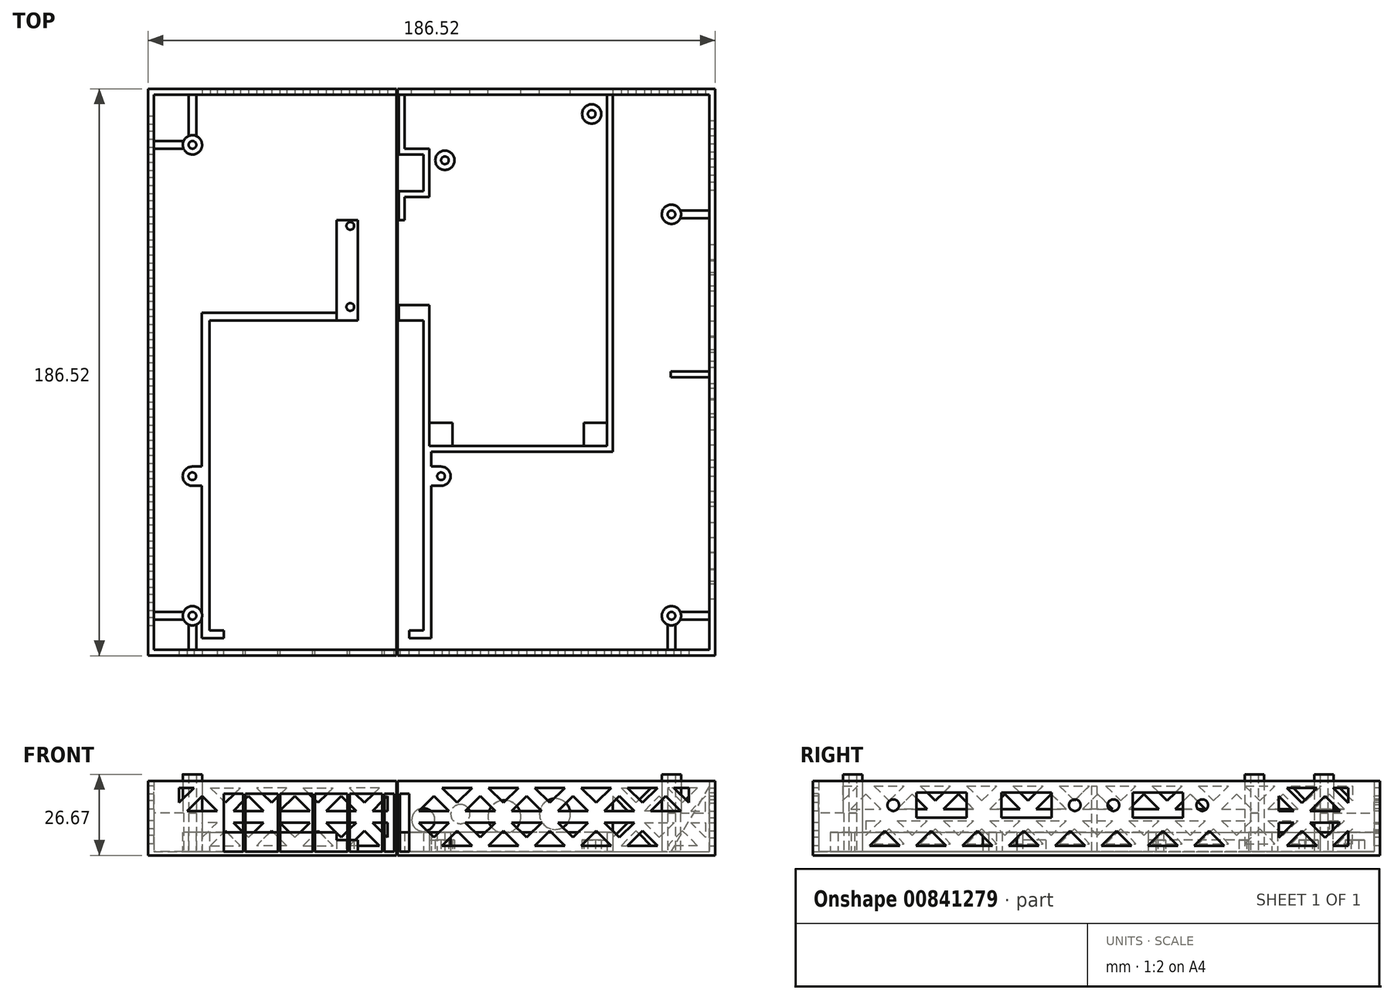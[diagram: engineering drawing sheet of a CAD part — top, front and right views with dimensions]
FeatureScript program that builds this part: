
annotation { "Feature Type Name" : "Feature", "Feature Type Description" : "" }
export const myFeature = defineFeature(function(context is Context, id is Id, definition is map)
    precondition{}
    {
        {
            var Q0;
            Q0=qCreatedBy(makeId("Top.planeOp"),FACE);
            var sketch = newSketch(context, id + "F0", { "sketchPlane" : qUnion([Q0])});
            skLineSegment(sketch, "E0.bottom", {"start": v(-6.35, 10.16) * mm, "end": v(163.65, 10.16) * mm});
            skLineSegment(sketch, "E0.top", {"start": v(-6.35, -159.84) * mm, "end": v(163.65, -159.84) * mm});
            skLineSegment(sketch, "E0.left", {"start": v(-6.35, 10.16) * mm, "end": v(-6.35, -159.84) * mm});
            skLineSegment(sketch, "E0.right", {"start": v(163.65, 10.16) * mm, "end": v(163.65, -159.84) * mm});
            skPoint(sketch, "E1", {"position": v(0, -154.94) * mm});
            skPoint(sketch, "E2", {"position": v(157.48, -22.86) * mm});
            skPoint(sketch, "E3", {"position": v(157.48, -154.94) * mm});
            skCircle(sketch, "E4", {"center": v(0, -154.94) * mm, "radius": 3.18 * mm});
            skCircle(sketch, "E5", {"center": v(0, 0) * mm, "radius": 3.18 * mm});
            skCircle(sketch, "E6", {"center": v(157.48, -22.86) * mm, "radius": 3.18 * mm});
            skCircle(sketch, "E7", {"center": v(157.48, -154.94) * mm, "radius": 3.18 * mm});
            skSolve(sketch);
        }
        {
            var Q0;
            Q0=qCreatedBy(makeId("Top.planeOp"),FACE);
            var sketch = newSketch(context, id + "F1", { "sketchPlane" : qUnion([Q0])});
            skLineSegment(sketch, "E8.0", {"start": v(-12.7, 16.51) * mm, "end": v(170, 16.51) * mm});
            skLineSegment(sketch, "E8.1", {"start": v(-12.7, 16.51) * mm, "end": v(-12.7, -166.2) * mm});
            skLineSegment(sketch, "E8.2", {"start": v(-12.7, -166.2) * mm, "end": v(170, -166.2) * mm});
            skLineSegment(sketch, "E8.3", {"start": v(170, 16.51) * mm, "end": v(170, -166.2) * mm});
            skLineSegment(sketch, "E9.0", {"start": v(-14.6, 18.42) * mm, "end": v(171.9, 18.42) * mm});
            skLineSegment(sketch, "E9.1", {"start": v(-14.6, 18.42) * mm, "end": v(-14.6, -168.1) * mm});
            skLineSegment(sketch, "E9.2", {"start": v(-14.6, -168.1) * mm, "end": v(171.9, -168.1) * mm});
            skLineSegment(sketch, "E9.3", {"start": v(171.9, 18.42) * mm, "end": v(171.9, -168.1) * mm});
            skSolve(sketch);
        }
        {
            var Q0;
            Q0 = qSketchRegion(id + "F1", true);
            extrude(context, id + "F2", {"entities" : qUnion([Q0]), "depth" : 86.36 * mm, "offsetDistance" : 25.4 * mm});
        }
        {
            var Q0;
            Q0=qCreatedBy(makeId("Top.planeOp"),FACE);
            var sketch = newSketch(context, id + "F3", { "sketchPlane" : qUnion([Q0])});
            skLineSegment(sketch, "E10.bottom", {"start": v(135.08, -97.79) * mm, "end": v(135.08, 15.24) * mm, "construction": true});
            skLineSegment(sketch, "E10.top", {"start": v(79.2, -18.41) * mm, "end": v(79.2, 0) * mm, "construction": true});
            skLineSegment(sketch, "E10.left", {"start": v(135.08, 15.24) * mm, "end": v(79.2, 15.24) * mm, "construction": true});
            skLineSegment(sketch, "E10.right", {"start": v(135.08, -97.79) * mm, "end": v(79.2, -97.79) * mm, "construction": true});
            skCircle(sketch, "E11", {"center": v(131.27, 10.16) * mm, "radius": 1.27 * mm});
            skCircle(sketch, "E12", {"center": v(131.27, 10.16) * mm, "radius": 3.18 * mm});
            skLineSegment(sketch, "E13", {"start": v(79.2, 15.24) * mm, "end": v(71.07, 15.24) * mm, "construction": true});
            skLineSegment(sketch, "E14", {"start": v(71.07, 15.24) * mm, "end": v(71.07, 0) * mm, "construction": true});
            skLineSegment(sketch, "E15", {"start": v(71.07, 0) * mm, "end": v(79.2, 0) * mm, "construction": true});
            skLineSegment(sketch, "E16", {"start": v(79.2, -18.41) * mm, "end": v(71.07, -18.41) * mm, "construction": true});
            skLineSegment(sketch, "E17", {"start": v(71.07, -18.41) * mm, "end": v(71.07, -50.16) * mm, "construction": true});
            skLineSegment(sketch, "E18", {"start": v(71.07, -50.16) * mm, "end": v(79.2, -50.16) * mm, "construction": true});
            skCircle(sketch, "E19", {"center": v(83, -5.08) * mm, "radius": 3.18 * mm});
            skCircle(sketch, "E20", {"center": v(83, -5.08) * mm, "radius": 1.27 * mm});
            skLineSegment(sketch, "E21.trimOffspring", {"start": v(79.2, -97.79) * mm, "end": v(79.2, -50.16) * mm, "construction": true});
            skLineSegment(sketch, "E22.0", {"start": v(77.93, -17.14) * mm, "end": v(77.93, -1.27) * mm});
            skLineSegment(sketch, "E22.1", {"start": v(77.93, -17.14) * mm, "end": v(69.8, -17.14) * mm});
            skLineSegment(sketch, "E22.4", {"start": v(77.93, -99.06) * mm, "end": v(77.93, -52.7) * mm});
            skLineSegment(sketch, "E22.5", {"start": v(69.8, -1.27) * mm, "end": v(77.93, -1.27) * mm});
            skLineSegment(sketch, "E22.6", {"start": v(69.8, 16.51) * mm, "end": v(69.8, -1.27) * mm});
            skLineSegment(sketch, "E22.8", {"start": v(136.35, 16.51) * mm, "end": v(69.8, 16.51) * mm});
            skLineSegment(sketch, "E22.9", {"start": v(136.35, -99.06) * mm, "end": v(136.35, 16.51) * mm});
            skLineSegment(sketch, "E22.10", {"start": v(136.35, -99.06) * mm, "end": v(77.93, -99.06) * mm});
            skLineSegment(sketch, "E23.bottom", {"start": v(77.93, -99.06) * mm, "end": v(77.93, -91.44) * mm});
            skLineSegment(sketch, "E23.top", {"start": v(85.55, -99.06) * mm, "end": v(85.55, -91.44) * mm});
            skLineSegment(sketch, "E23.left", {"start": v(77.93, -99.06) * mm, "end": v(85.55, -99.06) * mm});
            skLineSegment(sketch, "E23.right", {"start": v(77.93, -91.44) * mm, "end": v(85.55, -91.44) * mm});
            skLineSegment(sketch, "E24.bottom", {"start": v(136.35, -99.06) * mm, "end": v(136.35, -91.44) * mm});
            skLineSegment(sketch, "E24.top", {"start": v(128.73, -99.06) * mm, "end": v(128.73, -91.44) * mm});
            skLineSegment(sketch, "E24.left", {"start": v(136.35, -99.06) * mm, "end": v(128.73, -99.06) * mm});
            skLineSegment(sketch, "E24.right", {"start": v(136.35, -91.44) * mm, "end": v(128.73, -91.44) * mm});
            skLineSegment(sketch, "E25.0", {"start": v(138.25, -100.96) * mm, "end": v(76.02, -100.96) * mm});
            skLineSegment(sketch, "E25.1", {"start": v(138.25, -100.96) * mm, "end": v(138.25, 18.42) * mm});
            skLineSegment(sketch, "E25.2", {"start": v(76.02, -100.96) * mm, "end": v(76.02, -57.78) * mm});
            skLineSegment(sketch, "E25.3", {"start": v(138.25, 18.42) * mm, "end": v(67.9, 18.42) * mm});
            skLineSegment(sketch, "E25.4", {"start": v(67.9, 18.42) * mm, "end": v(67.9, -3.17) * mm});
            skLineSegment(sketch, "E25.5", {"start": v(67.9, -3.17) * mm, "end": v(76.02, -3.17) * mm});
            skLineSegment(sketch, "E25.7", {"start": v(67.9, -15.24) * mm, "end": v(67.9, -24.76) * mm});
            skLineSegment(sketch, "E25.8", {"start": v(76.02, -15.24) * mm, "end": v(67.9, -15.24) * mm});
            skLineSegment(sketch, "E25.9", {"start": v(76.02, -15.24) * mm, "end": v(76.02, -3.17) * mm});
            skLineSegment(sketch, "E26", {"start": v(76.02, -57.78) * mm, "end": v(47.45, -57.78) * mm});
            skLineSegment(sketch, "E27", {"start": v(69.8, -17.14) * mm, "end": v(69.8, -27.94) * mm});
            skCircle(sketch, "E28", {"center": v(51.9, -53.34) * mm, "radius": 1.27 * mm});
            skLineSegment(sketch, "E29", {"start": v(54.43, -52.7) * mm, "end": v(54.43, -27.94) * mm});
            skLineSegment(sketch, "E30", {"start": v(54.43, -52.7) * mm, "end": v(77.93, -52.7) * mm});
            skLineSegment(sketch, "E31", {"start": v(54.43, -27.94) * mm, "end": v(69.8, -27.94) * mm});
            skCircle(sketch, "E32", {"center": v(51.9, -26.67) * mm, "radius": 1.27 * mm});
            skLineSegment(sketch, "E33", {"start": v(47.45, -57.78) * mm, "end": v(47.45, -24.76) * mm});
            skLineSegment(sketch, "E34", {"start": v(47.45, -24.76) * mm, "end": v(67.9, -24.76) * mm});
            skLineSegment(sketch, "E35", {"start": v(54.43, -52.7) * mm, "end": v(54.43, -57.78) * mm});
            skLineSegment(sketch, "E36", {"start": v(54.43, -27.94) * mm, "end": v(54.43, -24.76) * mm});
            skLineSegment(sketch, "E37", {"start": v(136.35, 16.51) * mm, "end": v(138.25, 16.51) * mm});
            skLineSegment(sketch, "E38", {"start": v(69.8, 16.51) * mm, "end": v(67.9, 16.51) * mm});
            skLineSegment(sketch, "E39", {"start": v(67.9, -52.7) * mm, "end": v(67.9, -57.78) * mm});
            skLineSegment(sketch, "E40", {"start": v(67.9, -24.76) * mm, "end": v(69.8, -24.76) * mm});
            skSolve(sketch);
        }
        {
            var Q0;
            Q0=qCreatedBy(makeId("Top.planeOp"),FACE);
            var sketch = newSketch(context, id + "F4", { "sketchPlane" : qUnion([Q0])});
            skLineSegment(sketch, "E41.bottom", {"start": v(5.66, -57.78) * mm, "end": v(76.02, -57.78) * mm});
            skLineSegment(sketch, "E41.top", {"start": v(5.66, -159.84) * mm, "end": v(76.02, -159.84) * mm});
            skLineSegment(sketch, "E41.left", {"start": v(5.66, -57.78) * mm, "end": v(5.66, -159.84) * mm});
            skLineSegment(sketch, "E41.right", {"start": v(76.02, -57.78) * mm, "end": v(76.02, -159.84) * mm});
            skLineSegment(sketch, "E42.0", {"start": v(3.12, -55.24) * mm, "end": v(47.45, -55.24) * mm});
            skLineSegment(sketch, "E42.1", {"start": v(3.12, -55.24) * mm, "end": v(3.12, -105.86) * mm});
            skLineSegment(sketch, "E42.2", {"start": v(3.12, -162.38) * mm, "end": v(10.36, -162.38) * mm});
            skLineSegment(sketch, "E42.3", {"start": v(78.56, -100.96) * mm, "end": v(78.56, -105.86) * mm});
            skLineSegment(sketch, "E43", {"start": v(47.45, -55.24) * mm, "end": v(47.45, -57.78) * mm});
            skLineSegment(sketch, "E44", {"start": v(76.02, -100.96) * mm, "end": v(78.56, -100.96) * mm});
            skLineSegment(sketch, "E45", {"start": v(10.36, -162.38) * mm, "end": v(10.36, -159.84) * mm});
            skLineSegment(sketch, "E46", {"start": v(40.84, -162.38) * mm, "end": v(40.84, -159.84) * mm, "construction": true});
            skLineSegment(sketch, "E47.MirrorCS", {"start": v(71.32, -162.38) * mm, "end": v(71.32, -159.84) * mm});
            skLineSegment(sketch, "E48.trimOffspring", {"start": v(71.32, -162.38) * mm, "end": v(78.56, -162.38) * mm});
            skArc(sketch, "E49", {"start": v(81.74, -112.21) * mm, "mid": v(84.91, -109.04) * mm, "end": v(81.74, -105.86) * mm});
            skLineSegment(sketch, "E50", {"start": v(81.74, -105.86) * mm, "end": v(81.74, -112.21) * mm, "construction": true});
            skLineSegment(sketch, "E51", {"start": v(81.74, -112.21) * mm, "end": v(78.56, -112.21) * mm});
            skLineSegment(sketch, "E52", {"start": v(81.74, -105.86) * mm, "end": v(78.56, -105.86) * mm});
            skLineSegment(sketch, "E53.trimOffspring", {"start": v(78.56, -112.21) * mm, "end": v(78.56, -162.38) * mm});
            skLineSegment(sketch, "E54.MirrorCS", {"start": v(-0.05, -105.86) * mm, "end": v(3.12, -105.86) * mm});
            skLineSegment(sketch, "E55.MirrorCS", {"start": v(-0.05, -112.21) * mm, "end": v(3.12, -112.21) * mm});
            skArc(sketch, "E56.MirrorCS", {"start": v(-0.05, -112.21) * mm, "mid": v(-3.23, -109.04) * mm, "end": v(-0.05, -105.86) * mm});
            skLineSegment(sketch, "E57.trimOffspring", {"start": v(3.12, -112.21) * mm, "end": v(3.12, -162.38) * mm});
            skCircle(sketch, "E58", {"center": v(81.74, -109.04) * mm, "radius": 1.27 * mm});
            skCircle(sketch, "E59", {"center": v(-0.05, -109.04) * mm, "radius": 1.27 * mm});
            skSolve(sketch);
        }
        {
            var Q0;
            Q0=qCreatedBy(makeId("Top.planeOp"),FACE);
            var sketch = newSketch(context, id + "F5", { "sketchPlane" : qUnion([Q0])});
            skLineSegment(sketch, "E60.bottom", {"start": v(-14.6, 18.42) * mm, "end": v(171.9, 18.42) * mm});
            skLineSegment(sketch, "E60.top", {"start": v(-14.6, -168.1) * mm, "end": v(171.9, -168.1) * mm});
            skLineSegment(sketch, "E60.left", {"start": v(-14.6, 18.42) * mm, "end": v(-14.6, -168.1) * mm});
            skLineSegment(sketch, "E60.right", {"start": v(171.9, 18.42) * mm, "end": v(171.9, -168.1) * mm});
            skSolve(sketch);
        }
        {
            var Q0;
            Q0 = qSketchRegion(id + "F5", true);
            extrude(context, id + "F6", {"entities" : qUnion([Q0]), "operationType" : NewBodyOperationType.ADD, "oppositeDirection" : true, "depth" : 1.27 * mm, "offsetDistance" : 25.4 * mm});
        }
        {
            var Q0;
            Q0=qCreatedBy(makeId("Top.planeOp"),FACE);
            var sketch = newSketch(context, id + "F7", { "sketchPlane" : qUnion([Q0])});
            skLineSegment(sketch, "E61.bottom", {"start": v(77.93, -91.44) * mm, "end": v(85.55, -91.44) * mm});
            skLineSegment(sketch, "E61.top", {"start": v(77.93, -99.06) * mm, "end": v(85.55, -99.06) * mm});
            skLineSegment(sketch, "E61.left", {"start": v(77.93, -91.44) * mm, "end": v(77.93, -99.06) * mm});
            skLineSegment(sketch, "E61.right", {"start": v(85.55, -91.44) * mm, "end": v(85.55, -99.06) * mm});
            skLineSegment(sketch, "E62.bottom", {"start": v(128.73, -91.44) * mm, "end": v(136.35, -91.44) * mm});
            skLineSegment(sketch, "E62.top", {"start": v(128.73, -99.06) * mm, "end": v(136.35, -99.06) * mm});
            skLineSegment(sketch, "E62.left", {"start": v(128.73, -91.44) * mm, "end": v(128.73, -99.06) * mm});
            skLineSegment(sketch, "E62.right", {"start": v(136.35, -91.44) * mm, "end": v(136.35, -99.06) * mm});
            skCircle(sketch, "E63.0", {"center": v(83, -5.08) * mm, "radius": 3.18 * mm});
            skCircle(sketch, "E63.1", {"center": v(131.27, 10.16) * mm, "radius": 3.18 * mm});
            skCircle(sketch, "E64.0", {"center": v(83, -5.08) * mm, "radius": 1.27 * mm});
            skCircle(sketch, "E64.1", {"center": v(131.27, 10.16) * mm, "radius": 1.27 * mm});
            skLineSegment(sketch, "E65.bottom", {"start": v(47.45, -24.76) * mm, "end": v(54.43, -24.76) * mm});
            skLineSegment(sketch, "E65.top", {"start": v(47.45, -57.78) * mm, "end": v(54.43, -57.78) * mm});
            skLineSegment(sketch, "E65.left", {"start": v(47.45, -24.76) * mm, "end": v(47.45, -57.78) * mm});
            skLineSegment(sketch, "E65.right", {"start": v(54.43, -24.76) * mm, "end": v(54.43, -57.78) * mm});
            skCircle(sketch, "E66.1", {"center": v(51.9, -26.67) * mm, "radius": 1.27 * mm});
            skCircle(sketch, "E66.2", {"center": v(51.9, -53.34) * mm, "radius": 1.27 * mm});
            skSolve(sketch);
        }
        {
            var Q0;
            Q0 = qSketchRegion(id + "F7", true);
            extrude(context, id + "F8", {"entities" : qUnion([Q0]), "operationType" : NewBodyOperationType.ADD, "depth" : 3.8 * mm, "offsetDistance" : 25.4 * mm});
        }
        {
            var Q0;
            Q0=qCreatedBy(makeId("Top.planeOp"),FACE);
            var sketch = newSketch(context, id + "F9", { "sketchPlane" : qUnion([Q0])});
            skLineSegment(sketch, "E67.0", {"start": v(67.9, -15.24) * mm, "end": v(67.9, -24.76) * mm});
            skLineSegment(sketch, "E67.1", {"start": v(67.9, -24.76) * mm, "end": v(69.8, -24.76) * mm});
            skLineSegment(sketch, "E67.2", {"start": v(69.8, -17.14) * mm, "end": v(69.8, -24.76) * mm});
            skLineSegment(sketch, "E67.3", {"start": v(76.02, -15.24) * mm, "end": v(67.9, -15.24) * mm});
            skLineSegment(sketch, "E67.4", {"start": v(77.93, -17.14) * mm, "end": v(69.8, -17.14) * mm});
            skLineSegment(sketch, "E67.5", {"start": v(77.93, -17.14) * mm, "end": v(77.93, -1.27) * mm});
            skLineSegment(sketch, "E67.6", {"start": v(76.02, -15.24) * mm, "end": v(76.02, -3.17) * mm});
            skLineSegment(sketch, "E67.7", {"start": v(69.8, -1.27) * mm, "end": v(77.93, -1.27) * mm});
            skLineSegment(sketch, "E67.8", {"start": v(67.9, -3.17) * mm, "end": v(76.02, -3.17) * mm});
            skLineSegment(sketch, "E67.9", {"start": v(67.9, 16.51) * mm, "end": v(67.9, -3.17) * mm});
            skLineSegment(sketch, "E67.10", {"start": v(69.8, 16.51) * mm, "end": v(69.8, -1.27) * mm});
            skLineSegment(sketch, "E67.13", {"start": v(136.35, -99.06) * mm, "end": v(136.35, 16.51) * mm});
            skLineSegment(sketch, "E67.14", {"start": v(138.25, -100.96) * mm, "end": v(138.25, 16.51) * mm});
            skLineSegment(sketch, "E67.15", {"start": v(136.35, -99.06) * mm, "end": v(77.93, -99.06) * mm});
            skLineSegment(sketch, "E67.16", {"start": v(138.25, -100.96) * mm, "end": v(78.56, -100.96) * mm});
            skLineSegment(sketch, "E67.17", {"start": v(78.56, -100.96) * mm, "end": v(78.56, -105.86) * mm});
            skLineSegment(sketch, "E67.18", {"start": v(81.74, -105.86) * mm, "end": v(78.56, -105.86) * mm});
            skArc(sketch, "E67.19", {"start": v(81.74, -112.21) * mm, "mid": v(84.91, -109.04) * mm, "end": v(81.74, -105.86) * mm});
            skLineSegment(sketch, "E67.20.1", {"start": v(76.02, -100.96) * mm, "end": v(76.02, -159.84) * mm});
            skLineSegment(sketch, "E67.20.2", {"start": v(76.02, -159.84) * mm, "end": v(71.32, -159.84) * mm});
            skLineSegment(sketch, "E67.20.3", {"start": v(71.32, -159.84) * mm, "end": v(71.32, -162.38) * mm});
            skLineSegment(sketch, "E67.20.4", {"start": v(71.32, -162.38) * mm, "end": v(78.56, -162.38) * mm});
            skLineSegment(sketch, "E67.20.5", {"start": v(78.56, -162.38) * mm, "end": v(78.56, -112.21) * mm});
            skLineSegment(sketch, "E67.20.6", {"start": v(78.56, -112.21) * mm, "end": v(81.74, -112.21) * mm});
            skArc(sketch, "E67.20.7", {"start": v(81.74, -112.21) * mm, "mid": v(84.91, -109.04) * mm, "end": v(81.74, -105.86) * mm});
            skLineSegment(sketch, "E67.20.8", {"start": v(81.74, -105.86) * mm, "end": v(78.56, -105.86) * mm});
            skLineSegment(sketch, "E67.20.9", {"start": v(78.56, -105.86) * mm, "end": v(78.56, -100.96) * mm});
            skLineSegment(sketch, "E67.21.0", {"start": v(47.45, -57.78) * mm, "end": v(47.45, -55.24) * mm});
            skLineSegment(sketch, "E67.21.1", {"start": v(47.45, -55.24) * mm, "end": v(3.12, -55.24) * mm});
            skLineSegment(sketch, "E67.21.2", {"start": v(3.12, -55.24) * mm, "end": v(3.12, -105.86) * mm});
            skLineSegment(sketch, "E67.21.3", {"start": v(3.12, -105.86) * mm, "end": v(-0.05, -105.86) * mm});
            skArc(sketch, "E67.21.4", {"start": v(-0.05, -105.86) * mm, "mid": v(-3.23, -109.04) * mm, "end": v(-0.05, -112.21) * mm});
            skLineSegment(sketch, "E67.21.5", {"start": v(-0.05, -112.21) * mm, "end": v(3.12, -112.21) * mm});
            skLineSegment(sketch, "E67.21.6", {"start": v(3.12, -112.21) * mm, "end": v(3.12, -162.38) * mm});
            skLineSegment(sketch, "E67.21.7", {"start": v(3.12, -162.38) * mm, "end": v(10.36, -162.38) * mm});
            skLineSegment(sketch, "E67.21.8", {"start": v(10.36, -162.38) * mm, "end": v(10.36, -159.84) * mm});
            skLineSegment(sketch, "E67.21.9", {"start": v(10.36, -159.84) * mm, "end": v(5.66, -159.84) * mm});
            skLineSegment(sketch, "E67.21.10", {"start": v(5.66, -159.84) * mm, "end": v(5.66, -57.78) * mm});
            skLineSegment(sketch, "E67.21.11", {"start": v(5.66, -57.78) * mm, "end": v(47.45, -57.78) * mm});
            skLineSegment(sketch, "E67.22", {"start": v(76.02, -100.96) * mm, "end": v(76.02, -57.78) * mm});
            skLineSegment(sketch, "E67.23", {"start": v(77.93, -99.06) * mm, "end": v(77.93, -52.7) * mm});
            skLineSegment(sketch, "E67.24", {"start": v(67.9, -52.7) * mm, "end": v(77.93, -52.7) * mm});
            skLineSegment(sketch, "E67.25", {"start": v(67.9, -52.7) * mm, "end": v(67.9, -57.78) * mm});
            skLineSegment(sketch, "E67.26", {"start": v(76.02, -57.78) * mm, "end": v(67.9, -57.78) * mm});
            skPoint(sketch, "E68.orphan", {"position": v(69.8, -27.94) * mm});
            skPoint(sketch, "E69.orphan", {"position": v(54.43, -52.7) * mm});
            skPoint(sketch, "E70.orphan", {"position": v(47.45, -57.78) * mm});
            skPoint(sketch, "E71.orphan", {"position": v(76.02, -100.96) * mm});
            skLineSegment(sketch, "E72.0", {"start": v(67.9, 16.51) * mm, "end": v(69.8, 16.51) * mm});
            skPoint(sketch, "E73.orphan", {"position": v(-12.7, 16.51) * mm});
            skPoint(sketch, "E74.orphan", {"position": v(170, 16.51) * mm});
            skPoint(sketch, "E75.orphan", {"position": v(138.25, 18.42) * mm});
            skPoint(sketch, "E76.orphan", {"position": v(67.9, 18.42) * mm});
            skLineSegment(sketch, "E77.trimOffspring", {"start": v(136.35, 16.51) * mm, "end": v(138.25, 16.51) * mm});
            skCircle(sketch, "E78.0", {"center": v(-0.05, -109.04) * mm, "radius": 1.27 * mm});
            skCircle(sketch, "E78.1", {"center": v(81.74, -109.04) * mm, "radius": 1.27 * mm});
            skSolve(sketch);
        }
        {
            var Q0;
            Q0 = qSketchRegion(id + "F9", true);
            extrude(context, id + "F10", {"entities" : qUnion([Q0]), "operationType" : NewBodyOperationType.ADD, "depth" : 6.35 * mm, "offsetDistance" : 25.4 * mm});
        }
        {
            var Q0;
            Q0=makeQuery(id+"F6.boolean.opBoolean","MERGE",FACE,{"derivedFrom":[makeQuery(id+"F2.opExtrude","SWEPT_FACE",FACE,{"disambiguationData":[OSD([sQuery(id+"F1.wireOp",EDGE,"E9.0")])]}),makeQuery(id+"F6.opExtrude","SWEPT_FACE",FACE,{"disambiguationData":[OSD([sQuery(id+"F5.wireOp",EDGE,"E60.bottom")])]})]});
            var sketch = newSketch(context, id + "F11", { "sketchPlane" : qUnion([Q0])});
            skCircle(sketch, "E79", {"center": v(-119.2, 12.32) * mm, "radius": 5.08 * mm});
            skCircle(sketch, "E80", {"center": v(-102.56, 11.43) * mm, "radius": 5.4 * mm});
            skCircle(sketch, "E81", {"center": v(-88.09, 12.32) * mm, "radius": 3.18 * mm});
            skCircle(sketch, "E82", {"center": v(-75.9, 10.41) * mm, "radius": 3.81 * mm});
            skLineSegment(sketch, "E83", {"start": v(-54.43, 3.81) * mm, "end": v(-135.08, 3.81) * mm, "construction": true});
            skLineSegment(sketch, "E84", {"start": v(-135.08, 3.81) * mm, "end": v(-135.08, 0) * mm, "construction": true});
            skSolve(sketch);
        }
        {
            var Q0;
            Q0 = qSketchRegion(id + "F11", true);
            extrude(context, id + "F12", {"entities" : qUnion([Q0]), "operationType" : NewBodyOperationType.REMOVE, "endBound" : BoundingType.UP_TO_NEXT, "oppositeDirection" : true, "depth" : 25.4 * mm, "offsetDistance" : 25.4 * mm});
        }
        {
            var Q0;
            Q0=makeQuery(id+"F2.opExtrude","SWEPT_FACE",FACE,{"disambiguationData":[OSD([sQuery(id+"F1.wireOp",EDGE,"E8.2")])]});
            var sketch = newSketch(context, id + "F13", { "sketchPlane" : qUnion([Q0])});
            skLineSegment(sketch, "E85.0", {"start": v(-10.36, 6.35) * mm, "end": v(-10.36, 0) * mm});
            skLineSegment(sketch, "E85.1", {"start": v(-71.32, 6.35) * mm, "end": v(-71.32, 0) * mm});
            skLineSegment(sketch, "E86", {"start": v(-10.36, 6.35) * mm, "end": v(-71.32, 6.35) * mm, "construction": true});
            skLineSegment(sketch, "E87", {"start": v(-10.36, 0) * mm, "end": v(-71.32, 0) * mm});
            skLineSegment(sketch, "E88", {"start": v(-10.36, 6.35) * mm, "end": v(-10.36, 19.05) * mm});
            skLineSegment(sketch, "E89", {"start": v(-10.36, 19.05) * mm, "end": v(-71.32, 19.05) * mm});
            skLineSegment(sketch, "E90", {"start": v(-71.32, 19.05) * mm, "end": v(-71.32, 6.35) * mm});
            skLineSegment(sketch, "E91", {"start": v(-16.71, 19.05) * mm, "end": v(-16.71, 0) * mm});
            skLineSegment(sketch, "E92", {"start": v(-17.47, 19.05) * mm, "end": v(-17.47, 0) * mm});
            skLineSegment(sketch, "E93.1.0.0", {"start": v(-28.14, 19.05) * mm, "end": v(-28.14, 0) * mm});
            skLineSegment(sketch, "E93.1.0.1", {"start": v(-28.9, 19.05) * mm, "end": v(-28.9, 0) * mm});
            skLineSegment(sketch, "E93.2.0.0", {"start": v(-39.57, 19.05) * mm, "end": v(-39.57, 0) * mm});
            skLineSegment(sketch, "E93.2.0.1", {"start": v(-40.33, 19.05) * mm, "end": v(-40.33, 0) * mm});
            skLineSegment(sketch, "E93.3.0.0", {"start": v(-51, 19.05) * mm, "end": v(-51, 0) * mm});
            skLineSegment(sketch, "E93.3.0.1", {"start": v(-51.76, 19.05) * mm, "end": v(-51.76, 0) * mm});
            skLineSegment(sketch, "E93.4.0.0", {"start": v(-62.43, 19.05) * mm, "end": v(-62.43, 0) * mm});
            skLineSegment(sketch, "E93.4.0.1", {"start": v(-63.2, 19.05) * mm, "end": v(-63.2, 0) * mm});
            skLineSegment(sketch, "E93.direction1", {"start": v(-17.47, 0) * mm, "end": v(-28.9, 0) * mm, "construction": true});
            skSolve(sketch);
        }
        {
            var Q0;
            {var subQ4=sQuery(id+"F13.wireOp",EDGE,"E85.0");Q0=makeQuery(id+"F13.imprint","IMPRINT",FACE,{"disambiguationData":[TD([[makeQuery(id+"F13.imprint","IMPRINT",EDGE,{"derivedFrom":subQ4}),-1.0]])]});}
            var Q1;
            {var subQ0=sQuery(id+"F13.wireOp",EDGE,"E92");Q1=makeQuery(id+"F13.imprint","IMPRINT",FACE,{"disambiguationData":[TD([[makeQuery(id+"F13.imprint","IMPRINT",EDGE,{"derivedFrom":subQ0}),-1.0]])]});}
            var Q2;
            {var subQ0=sQuery(id+"F13.wireOp",EDGE,"E93.1.0.1");Q2=makeQuery(id+"F13.imprint","IMPRINT",FACE,{"disambiguationData":[TD([[makeQuery(id+"F13.imprint","IMPRINT",EDGE,{"derivedFrom":subQ0}),-1.0]])]});}
            var Q3;
            {var subQ0=sQuery(id+"F13.wireOp",EDGE,"E93.2.0.1");Q3=makeQuery(id+"F13.imprint","IMPRINT",FACE,{"disambiguationData":[TD([[makeQuery(id+"F13.imprint","IMPRINT",EDGE,{"derivedFrom":subQ0}),-1.0]])]});}
            var Q4;
            {var subQ0=sQuery(id+"F13.wireOp",EDGE,"E93.3.0.1");Q4=makeQuery(id+"F13.imprint","IMPRINT",FACE,{"disambiguationData":[TD([[makeQuery(id+"F13.imprint","IMPRINT",EDGE,{"derivedFrom":subQ0}),-1.0]])]});}
            var Q5;
            {var subQ4=sQuery(id+"F13.wireOp",EDGE,"E85.1");Q5=makeQuery(id+"F13.imprint","IMPRINT",FACE,{"disambiguationData":[TD([[makeQuery(id+"F13.imprint","IMPRINT",EDGE,{"derivedFrom":subQ4}),1.0]])]});}
            extrude(context, id + "F14", {"entities" : qUnion([Q0, Q1, Q2, Q3, Q4, Q5]), "operationType" : NewBodyOperationType.REMOVE, "oppositeDirection" : true, "depth" : 2.54 * mm, "offsetDistance" : 25.4 * mm});
        }
        {
            var Q0;
            Q0=makeQuery(id+"F6.boolean.opBoolean","MERGE",FACE,{"derivedFrom":[makeQuery(id+"F2.opExtrude","SWEPT_FACE",FACE,{"disambiguationData":[OSD([sQuery(id+"F1.wireOp",EDGE,"E9.3")])]}),makeQuery(id+"F6.opExtrude","SWEPT_FACE",FACE,{"disambiguationData":[OSD([sQuery(id+"F5.wireOp",EDGE,"E60.right")])]})]});
            var sketch = newSketch(context, id + "F15", { "sketchPlane" : qUnion([Q0])});
            skLineSegment(sketch, "E94.bottom", {"start": v(-149.86, 8.9) * mm, "end": v(-25.4, 8.9) * mm, "construction": true});
            skLineSegment(sketch, "E94.top", {"start": v(-149.86, 21.59) * mm, "end": v(-25.4, 21.59) * mm, "construction": true});
            skLineSegment(sketch, "E94.left", {"start": v(-149.86, 8.9) * mm, "end": v(-149.86, 21.6) * mm, "construction": true});
            skLineSegment(sketch, "E94.right", {"start": v(-25.4, 8.9) * mm, "end": v(-25.4, 21.59) * mm, "construction": true});
            skLineSegment(sketch, "E95", {"start": v(-111.76, 21.6) * mm, "end": v(-111.76, 8.9) * mm, "construction": true});
            skLineSegment(sketch, "E96.bottom", {"start": v(-117.47, 19.37) * mm, "end": v(-133.98, 19.37) * mm});
            skLineSegment(sketch, "E96.top", {"start": v(-117.47, 11.11) * mm, "end": v(-133.98, 11.11) * mm});
            skLineSegment(sketch, "E96.left", {"start": v(-117.47, 19.37) * mm, "end": v(-117.47, 11.11) * mm});
            skLineSegment(sketch, "E96.right", {"start": v(-133.98, 19.37) * mm, "end": v(-133.98, 11.11) * mm});
            skPoint(sketch, "E96.middle", {"position": v(-125.73, 15.24) * mm});
            skPoint(sketch, "E97", {"position": v(-111.76, 15.24) * mm});
            skCircle(sketch, "E98", {"center": v(-141.6, 15.24) * mm, "radius": 1.9 * mm});
            skPoint(sketch, "E98.centerSnap0", {"position": v(-133.98, 15.24) * mm});
            skLineSegment(sketch, "E99.MirrorCS", {"start": v(-106.04, 19.37) * mm, "end": v(-106.04, 11.11) * mm});
            skLineSegment(sketch, "E100.MirrorCS", {"start": v(-106.04, 19.37) * mm, "end": v(-89.53, 19.37) * mm});
            skLineSegment(sketch, "E101.MirrorCS", {"start": v(-89.53, 19.37) * mm, "end": v(-89.53, 11.11) * mm});
            skPoint(sketch, "E102.MirrorP", {"position": v(-89.53, 15.24) * mm});
            skCircle(sketch, "E103.MirrorC", {"center": v(-81.91, 15.24) * mm, "radius": 1.9 * mm});
            skPoint(sketch, "E104.MirrorP", {"position": v(-97.79, 15.24) * mm});
            skLineSegment(sketch, "E105.MirrorCS", {"start": v(-106.04, 11.11) * mm, "end": v(-89.53, 11.11) * mm});
            skLineSegment(sketch, "E106", {"start": v(-54.6, 21.6) * mm, "end": v(-54.6, 8.9) * mm, "construction": true});
            skLineSegment(sketch, "E107.bottom", {"start": v(-46.35, 19.37) * mm, "end": v(-62.86, 19.37) * mm});
            skLineSegment(sketch, "E107.top", {"start": v(-46.35, 11.11) * mm, "end": v(-62.86, 11.11) * mm});
            skLineSegment(sketch, "E107.left", {"start": v(-46.35, 19.37) * mm, "end": v(-46.35, 11.11) * mm});
            skLineSegment(sketch, "E107.right", {"start": v(-62.86, 19.37) * mm, "end": v(-62.86, 11.11) * mm});
            skPoint(sketch, "E107.middle", {"position": v(-54.6, 15.24) * mm});
            skCircle(sketch, "E108", {"center": v(-69.22, 15.24) * mm, "radius": 1.9 * mm});
            skCircle(sketch, "E109.MirrorC", {"center": v(-40, 15.24) * mm, "radius": 1.9 * mm});
            skLineSegment(sketch, "E110", {"start": v(-75.56, 21.59) * mm, "end": v(-75.56, 8.9) * mm, "construction": true});
            skSolve(sketch);
        }
        {
            var Q0;
            Q0 = qSketchRegion(id + "F15", true);
            extrude(context, id + "F16", {"entities" : qUnion([Q0]), "operationType" : NewBodyOperationType.REMOVE, "endBound" : BoundingType.UP_TO_NEXT, "oppositeDirection" : true, "depth" : 25.4 * mm, "offsetDistance" : 25.4 * mm});
        }
        {
            var Q0;
            Q0=sQuery(id+"F15.wireOp",EDGE,"E110");
            cPoint(context, id + "F17", {"entities" : qUnion([Q0]), "parameter" : 0.5});
        }
        {
            var Q0;
            Q0=qCreatedBy(makeId("Front.planeOp"),FACE);
            var Q1;
            Q1 = qCreatedBy(id + "F17" ,VERTEX);
            cPlane(context, id + "F18", {"entities" : qUnion([Q0, Q1]), "cplaneType" : CPlaneType.PLANE_POINT, "offset" : 25.4 * mm, "width" : 152.4 * mm, "height" : 152.4 * mm});
        }
        {
            var Q0;
            Q0=qCreatedBy(id+"F18.planeOp",FACE);
            var sketch = newSketch(context, id + "F19", { "sketchPlane" : qUnion([Q0])});
            skLineSegment(sketch, "E111", {"start": v(170, 21.6) * mm, "end": v(157.3, 0) * mm});
            skLineSegment(sketch, "E112", {"start": v(157.3, 0) * mm, "end": v(170, 0) * mm});
            skLineSegment(sketch, "E113", {"start": v(170, 0) * mm, "end": v(170, 21.59) * mm});
            skSolve(sketch);
        }
        {
            var Q0;
            Q0 = qSketchRegion(id + "F19", true);
            extrude(context, id + "F20", {"entities" : qUnion([Q0]), "operationType" : NewBodyOperationType.ADD, "endBound" : BoundingType.SYMMETRIC, "depth" : 1.9 * mm, "offsetDistance" : 25.4 * mm});
        }
        {
            var Q0;
            Q0=qCreatedBy(makeId("Top.planeOp"),FACE);
            var sketch = newSketch(context, id + "F21", { "sketchPlane" : qUnion([Q0])});
            skCircle(sketch, "E114.0", {"center": v(0, 0) * mm, "radius": 3.18 * mm});
            skCircle(sketch, "E114.1", {"center": v(157.48, -22.86) * mm, "radius": 3.18 * mm});
            skCircle(sketch, "E114.2", {"center": v(157.48, -154.94) * mm, "radius": 3.18 * mm});
            skCircle(sketch, "E114.3", {"center": v(0, -154.94) * mm, "radius": 3.18 * mm});
            skCircle(sketch, "E115", {"center": v(0, 0) * mm, "radius": 1.27 * mm});
            skCircle(sketch, "E116", {"center": v(157.48, -22.86) * mm, "radius": 1.27 * mm});
            skCircle(sketch, "E117", {"center": v(157.48, -154.94) * mm, "radius": 1.27 * mm});
            skCircle(sketch, "E118", {"center": v(0, -154.94) * mm, "radius": 1.27 * mm});
            skLineSegment(sketch, "E119", {"start": v(160.39, -153.67) * mm, "end": v(170, -153.67) * mm});
            skLineSegment(sketch, "E120.0", {"start": v(170, -21.59) * mm, "end": v(170, -24.13) * mm});
            skLineSegment(sketch, "E120.1", {"start": v(-1.27, -166.2) * mm, "end": v(1.27, -166.2) * mm});
            skLineSegment(sketch, "E120.2", {"start": v(-1.27, 16.51) * mm, "end": v(1.27, 16.51) * mm});
            skLineSegment(sketch, "E120.3", {"start": v(-12.7, 1.27) * mm, "end": v(-12.7, -1.27) * mm});
            skLineSegment(sketch, "E121", {"start": v(156.21, -157.85) * mm, "end": v(156.21, -166.2) * mm});
            skLineSegment(sketch, "E122", {"start": v(158.75, -157.85) * mm, "end": v(158.75, -166.2) * mm});
            skPoint(sketch, "E123.orphan", {"position": v(157.48, -153.67) * mm});
            skLineSegment(sketch, "E124.trimOffspring", {"start": v(160.39, -156.2) * mm, "end": v(170, -156.2) * mm});
            skPoint(sketch, "E125.start.orphan", {"position": v(157.48, -156.2) * mm});
            skPoint(sketch, "E126.orphan", {"position": v(158.75, -154.94) * mm});
            skPoint(sketch, "E127.orphan", {"position": v(156.21, -154.94) * mm});
            skLineSegment(sketch, "E128", {"start": v(-2.9, -153.67) * mm, "end": v(-12.7, -153.67) * mm});
            skLineSegment(sketch, "E129", {"start": v(1.27, -157.85) * mm, "end": v(1.27, -166.2) * mm});
            skPoint(sketch, "E130.orphan", {"position": v(0, -153.67) * mm});
            skLineSegment(sketch, "E131.trimOffspring", {"start": v(-2.9, -156.2) * mm, "end": v(-12.7, -156.2) * mm});
            skLineSegment(sketch, "E132.trimOffspring", {"start": v(-1.27, -157.85) * mm, "end": v(-1.27, -166.2) * mm});
            skPoint(sketch, "E133.start.orphan", {"position": v(0, -156.2) * mm});
            skPoint(sketch, "E134.start.orphan", {"position": v(-1.27, -154.94) * mm});
            skPoint(sketch, "E135.orphan", {"position": v(1.27, -154.94) * mm});
            skLineSegment(sketch, "E136", {"start": v(1.27, 2.9) * mm, "end": v(1.27, 16.51) * mm});
            skLineSegment(sketch, "E137", {"start": v(-1.27, 2.9) * mm, "end": v(-1.27, 16.51) * mm});
            skLineSegment(sketch, "E138", {"start": v(-2.9, -1.27) * mm, "end": v(-12.7, -1.27) * mm});
            skLineSegment(sketch, "E139", {"start": v(-2.9, 1.27) * mm, "end": v(-12.7, 1.27) * mm});
            skPoint(sketch, "E140.orphan", {"position": v(0, 1.27) * mm});
            skPoint(sketch, "E141.orphan", {"position": v(-1.27, 0) * mm});
            skPoint(sketch, "E142.orphan", {"position": v(1.27, 0) * mm});
            skPoint(sketch, "E143.orphan", {"position": v(0, -1.27) * mm});
            skLineSegment(sketch, "E144", {"start": v(160.39, -21.59) * mm, "end": v(170, -21.59) * mm});
            skLineSegment(sketch, "E145", {"start": v(160.39, -24.13) * mm, "end": v(170, -24.13) * mm});
            skPoint(sketch, "E146.orphan", {"position": v(157.48, -21.59) * mm});
            skPoint(sketch, "E147.orphan", {"position": v(157.48, -24.13) * mm});
            skPoint(sketch, "E148.orphan", {"position": v(-12.7, 16.51) * mm});
            skLineSegment(sketch, "E149.trimOffspring", {"start": v(-12.7, -153.67) * mm, "end": v(-12.7, -156.2) * mm});
            skPoint(sketch, "E150.orphan", {"position": v(-12.7, -166.2) * mm});
            skLineSegment(sketch, "E151.trimOffspring", {"start": v(156.21, -166.2) * mm, "end": v(158.75, -166.2) * mm});
            skPoint(sketch, "E152.orphan", {"position": v(170, -166.2) * mm});
            skLineSegment(sketch, "E153.trimOffspring", {"start": v(170, -153.67) * mm, "end": v(170, -156.2) * mm});
            skPoint(sketch, "E154.orphan", {"position": v(170, 16.51) * mm});
            skSolve(sketch);
        }
        {
            var Q0;
            Q0=makeQuery(id+"F21.imprint","IMPRINT",FACE,{"disambiguationData":[TD([[makeQuery(id+"F21.imprint","IMPRINT",EDGE,{"derivedFrom":sQuery(id+"F21.wireOp",EDGE,"E120.2")}),-1.0]])]});
            var Q1;
            Q1=makeQuery(id+"F21.imprint","IMPRINT",FACE,{"disambiguationData":[TD([[makeQuery(id+"F21.imprint","IMPRINT",EDGE,{"derivedFrom":sQuery(id+"F21.wireOp",EDGE,"E120.3")}),1.0]])]});
            var Q2;
            Q2=makeQuery(id+"F21.imprint","IMPRINT",FACE,{"disambiguationData":[TD([[makeQuery(id+"F21.imprint","IMPRINT",EDGE,{"derivedFrom":sQuery(id+"F21.wireOp",EDGE,"E115")}),1.0]])]});
            var Q3;
            Q3=makeQuery(id+"F21.imprint","IMPRINT",FACE,{"disambiguationData":[TD([[makeQuery(id+"F21.imprint","IMPRINT",EDGE,{"derivedFrom":sQuery(id+"F21.wireOp",EDGE,"E116")}),1.0]])]});
            var Q4;
            Q4=makeQuery(id+"F21.imprint","IMPRINT",FACE,{"disambiguationData":[TD([[makeQuery(id+"F21.imprint","IMPRINT",EDGE,{"derivedFrom":sQuery(id+"F21.wireOp",EDGE,"E120.0")}),-1.0]])]});
            var Q5;
            Q5=makeQuery(id+"F21.imprint","IMPRINT",FACE,{"disambiguationData":[TD([[makeQuery(id+"F21.imprint","IMPRINT",EDGE,{"derivedFrom":sQuery(id+"F21.wireOp",EDGE,"E117")}),1.0]])]});
            var Q6;
            {var subQ0=sQuery(id+"F21.wireOp",EDGE,"E119");Q6=makeQuery(id+"F21.imprint","IMPRINT",FACE,{"disambiguationData":[TD([[makeQuery(id+"F21.imprint","IMPRINT",EDGE,{"derivedFrom":subQ0}),-1.0]])]});}
            var Q7;
            {var subQ0=sQuery(id+"F21.wireOp",EDGE,"E121");Q7=makeQuery(id+"F21.imprint","IMPRINT",FACE,{"disambiguationData":[TD([[makeQuery(id+"F21.imprint","IMPRINT",EDGE,{"derivedFrom":subQ0}),1.0]])]});}
            var Q8;
            {var subQ0=sQuery(id+"F21.wireOp",EDGE,"E128");Q8=makeQuery(id+"F21.imprint","IMPRINT",FACE,{"disambiguationData":[TD([[makeQuery(id+"F21.imprint","IMPRINT",EDGE,{"derivedFrom":subQ0}),1.0]])]});}
            var Q9;
            Q9=makeQuery(id+"F21.imprint","IMPRINT",FACE,{"disambiguationData":[TD([[makeQuery(id+"F21.imprint","IMPRINT",EDGE,{"derivedFrom":sQuery(id+"F21.wireOp",EDGE,"E118")}),1.0]])]});
            var Q10;
            Q10=makeQuery(id+"F21.imprint","IMPRINT",FACE,{"disambiguationData":[TD([[makeQuery(id+"F21.imprint","IMPRINT",EDGE,{"derivedFrom":sQuery(id+"F21.wireOp",EDGE,"E120.1")}),1.0]])]});
            extrude(context, id + "F22", {"entities" : qUnion([Q0, Q1, Q2, Q3, Q4, Q5, Q6, Q7, Q8, Q9, Q10]), "operationType" : NewBodyOperationType.ADD, "depth" : 12.7 * mm, "offsetDistance" : 25.4 * mm});
        }
        {
            var Q0;
            Q0=makeQuery(id+"F21.imprint","IMPRINT",FACE,{"disambiguationData":[TD([[makeQuery(id+"F21.imprint","IMPRINT",EDGE,{"derivedFrom":sQuery(id+"F21.wireOp",EDGE,"E115")}),-1.0]])]});
            var Q1;
            Q1=makeQuery(id+"F21.imprint","IMPRINT",FACE,{"disambiguationData":[TD([[makeQuery(id+"F21.imprint","IMPRINT",EDGE,{"derivedFrom":sQuery(id+"F21.wireOp",EDGE,"E116")}),-1.0]])]});
            var Q2;
            Q2=makeQuery(id+"F21.imprint","IMPRINT",FACE,{"disambiguationData":[TD([[makeQuery(id+"F21.imprint","IMPRINT",EDGE,{"derivedFrom":sQuery(id+"F21.wireOp",EDGE,"E118")}),-1.0]])]});
            var Q3;
            Q3=makeQuery(id+"F21.imprint","IMPRINT",FACE,{"disambiguationData":[TD([[makeQuery(id+"F21.imprint","IMPRINT",EDGE,{"derivedFrom":sQuery(id+"F21.wireOp",EDGE,"E117")}),-1.0]])]});
            extrude(context, id + "F23", {"entities" : qUnion([Q0, Q1, Q2, Q3]), "operationType" : NewBodyOperationType.ADD, "depth" : 25.4 * mm, "offsetDistance" : 25.4 * mm});
        }
        {
            var Q0;
            Q0=qCreatedBy(makeId("Front.planeOp"),FACE);
            var sketch = newSketch(context, id + "F24", { "sketchPlane" : qUnion([Q0])});
            skLineSegment(sketch, "E155.bottom", {"start": v(166.9, 68.25) * mm, "end": v(7.52, 68.25) * mm});
            skLineSegment(sketch, "E155.top", {"start": v(166.9, 23.16) * mm, "end": v(7.52, 23.16) * mm});
            skLineSegment(sketch, "E155.left", {"start": v(166.9, 68.25) * mm, "end": v(166.9, 23.16) * mm});
            skLineSegment(sketch, "E155.right", {"start": v(7.52, 68.25) * mm, "end": v(7.52, 23.16) * mm});
            skLineSegment(sketch, "E156", {"start": v(156.74, 68.25) * mm, "end": v(156.74, 23.16) * mm});
            skLineSegment(sketch, "E157", {"start": v(155.98, 68.25) * mm, "end": v(155.98, 23.16) * mm});
            skLineSegment(sketch, "E158.1.0.0", {"start": v(144.04, 68.25) * mm, "end": v(144.04, 23.16) * mm});
            skLineSegment(sketch, "E158.1.0.1", {"start": v(143.28, 68.25) * mm, "end": v(143.28, 23.16) * mm});
            skLineSegment(sketch, "E158.2.0.0", {"start": v(131.34, 68.25) * mm, "end": v(131.34, 23.16) * mm});
            skLineSegment(sketch, "E158.2.0.1", {"start": v(130.58, 68.25) * mm, "end": v(130.58, 23.16) * mm});
            skLineSegment(sketch, "E158.3.0.0", {"start": v(118.64, 68.25) * mm, "end": v(118.64, 23.16) * mm});
            skLineSegment(sketch, "E158.3.0.1", {"start": v(117.88, 68.25) * mm, "end": v(117.88, 23.16) * mm});
            skLineSegment(sketch, "E158.4.0.0", {"start": v(105.94, 68.25) * mm, "end": v(105.94, 23.16) * mm});
            skLineSegment(sketch, "E158.4.0.1", {"start": v(105.18, 68.25) * mm, "end": v(105.18, 23.16) * mm});
            skLineSegment(sketch, "E158.5.0.0", {"start": v(93.24, 68.25) * mm, "end": v(93.24, 23.16) * mm});
            skLineSegment(sketch, "E158.5.0.1", {"start": v(92.48, 68.25) * mm, "end": v(92.48, 23.16) * mm});
            skLineSegment(sketch, "E158.6.0.0", {"start": v(80.54, 68.25) * mm, "end": v(80.54, 23.16) * mm});
            skLineSegment(sketch, "E158.6.0.1", {"start": v(79.78, 68.25) * mm, "end": v(79.78, 23.16) * mm});
            skLineSegment(sketch, "E158.7.0.0", {"start": v(67.84, 68.25) * mm, "end": v(67.84, 23.16) * mm});
            skLineSegment(sketch, "E158.7.0.1", {"start": v(67.08, 68.25) * mm, "end": v(67.08, 23.16) * mm});
            skLineSegment(sketch, "E158.8.0.0", {"start": v(55.14, 68.25) * mm, "end": v(55.14, 23.16) * mm});
            skLineSegment(sketch, "E158.8.0.1", {"start": v(54.38, 68.25) * mm, "end": v(54.38, 23.16) * mm});
            skLineSegment(sketch, "E158.9.0.0", {"start": v(42.44, 68.25) * mm, "end": v(42.44, 23.16) * mm});
            skLineSegment(sketch, "E158.9.0.1", {"start": v(41.68, 68.25) * mm, "end": v(41.68, 23.16) * mm});
            skLineSegment(sketch, "E158.10.0.0", {"start": v(29.74, 68.25) * mm, "end": v(29.74, 23.16) * mm});
            skLineSegment(sketch, "E158.10.0.1", {"start": v(28.98, 68.25) * mm, "end": v(28.98, 23.16) * mm});
            skLineSegment(sketch, "E158.11.0.0", {"start": v(17.04, 68.25) * mm, "end": v(17.04, 23.16) * mm});
            skLineSegment(sketch, "E158.11.0.1", {"start": v(16.28, 68.25) * mm, "end": v(16.28, 23.16) * mm});
            skLineSegment(sketch, "E158.direction1", {"start": v(156.74, 23.16) * mm, "end": v(144.04, 23.16) * mm, "construction": true});
            skSolve(sketch);
        }
        {
            var Q0;
            {var subQ0=sQuery(id+"F24.wireOp",EDGE,"E155.right");Q0=makeQuery(id+"F24.imprint","IMPRINT",FACE,{"disambiguationData":[TD([[makeQuery(id+"F24.imprint","IMPRINT",EDGE,{"derivedFrom":subQ0}),1.0]])]});}
            var Q1;
            {var subQ0=sQuery(id+"F24.wireOp",EDGE,"E158.10.0.1");Q1=makeQuery(id+"F24.imprint","IMPRINT",FACE,{"disambiguationData":[TD([[makeQuery(id+"F24.imprint","IMPRINT",EDGE,{"derivedFrom":subQ0}),-1.0]])]});}
            var Q2;
            {var subQ0=sQuery(id+"F24.wireOp",EDGE,"E158.9.0.1");Q2=makeQuery(id+"F24.imprint","IMPRINT",FACE,{"disambiguationData":[TD([[makeQuery(id+"F24.imprint","IMPRINT",EDGE,{"derivedFrom":subQ0}),-1.0]])]});}
            var Q3;
            {var subQ0=sQuery(id+"F24.wireOp",EDGE,"E158.8.0.1");Q3=makeQuery(id+"F24.imprint","IMPRINT",FACE,{"disambiguationData":[TD([[makeQuery(id+"F24.imprint","IMPRINT",EDGE,{"derivedFrom":subQ0}),-1.0]])]});}
            var Q4;
            {var subQ0=sQuery(id+"F24.wireOp",EDGE,"E158.7.0.1");Q4=makeQuery(id+"F24.imprint","IMPRINT",FACE,{"disambiguationData":[TD([[makeQuery(id+"F24.imprint","IMPRINT",EDGE,{"derivedFrom":subQ0}),-1.0]])]});}
            var Q5;
            {var subQ0=sQuery(id+"F24.wireOp",EDGE,"E158.6.0.1");Q5=makeQuery(id+"F24.imprint","IMPRINT",FACE,{"disambiguationData":[TD([[makeQuery(id+"F24.imprint","IMPRINT",EDGE,{"derivedFrom":subQ0}),-1.0]])]});}
            var Q6;
            {var subQ0=sQuery(id+"F24.wireOp",EDGE,"E158.5.0.1");Q6=makeQuery(id+"F24.imprint","IMPRINT",FACE,{"disambiguationData":[TD([[makeQuery(id+"F24.imprint","IMPRINT",EDGE,{"derivedFrom":subQ0}),-1.0]])]});}
            var Q7;
            {var subQ0=sQuery(id+"F24.wireOp",EDGE,"E158.4.0.1");Q7=makeQuery(id+"F24.imprint","IMPRINT",FACE,{"disambiguationData":[TD([[makeQuery(id+"F24.imprint","IMPRINT",EDGE,{"derivedFrom":subQ0}),-1.0]])]});}
            var Q8;
            {var subQ0=sQuery(id+"F24.wireOp",EDGE,"E158.3.0.1");Q8=makeQuery(id+"F24.imprint","IMPRINT",FACE,{"disambiguationData":[TD([[makeQuery(id+"F24.imprint","IMPRINT",EDGE,{"derivedFrom":subQ0}),-1.0]])]});}
            var Q9;
            {var subQ0=sQuery(id+"F24.wireOp",EDGE,"E158.2.0.1");Q9=makeQuery(id+"F24.imprint","IMPRINT",FACE,{"disambiguationData":[TD([[makeQuery(id+"F24.imprint","IMPRINT",EDGE,{"derivedFrom":subQ0}),-1.0]])]});}
            var Q10;
            {var subQ0=sQuery(id+"F24.wireOp",EDGE,"E158.1.0.1");Q10=makeQuery(id+"F24.imprint","IMPRINT",FACE,{"disambiguationData":[TD([[makeQuery(id+"F24.imprint","IMPRINT",EDGE,{"derivedFrom":subQ0}),-1.0]])]});}
            var Q11;
            {var subQ0=sQuery(id+"F24.wireOp",EDGE,"E157");Q11=makeQuery(id+"F24.imprint","IMPRINT",FACE,{"disambiguationData":[TD([[makeQuery(id+"F24.imprint","IMPRINT",EDGE,{"derivedFrom":subQ0}),-1.0]])]});}
            var Q12;
            {var subQ0=sQuery(id+"F24.wireOp",EDGE,"E155.left");Q12=makeQuery(id+"F24.imprint","IMPRINT",FACE,{"disambiguationData":[TD([[makeQuery(id+"F24.imprint","IMPRINT",EDGE,{"derivedFrom":subQ0}),-1.0]])]});}
            extrude(context, id + "F25", {"entities" : qUnion([Q0, Q1, Q2, Q3, Q4, Q5, Q6, Q7, Q8, Q9, Q10, Q11, Q12]), "operationType" : NewBodyOperationType.REMOVE, "oppositeDirection" : true, "depth" : 25.4 * mm, "offsetDistance" : 25.4 * mm});
        }
        {
            var Q0;
            Q0=makeQuery(id+"F2.opExtrude","SWEPT_FACE",FACE,{"disambiguationData":[OSD([sQuery(id+"F1.wireOp",EDGE,"E8.0")])]});
            var sketch = newSketch(context, id + "F26", { "sketchPlane" : qUnion([Q0])});
            skLineSegment(sketch, "E159", {"start": v(3.18, 1.9) * mm, "end": v(3.18, 9.52) * mm, "construction": true});
            skLineSegment(sketch, "E160", {"start": v(18.42, 9.52) * mm, "end": v(13.49, 9.52) * mm});
            skLineSegment(sketch, "E161", {"start": v(3.17, 1.9) * mm, "end": v(10.8, 9.53) * mm, "construction": true});
            skLineSegment(sketch, "E162", {"start": v(10.8, 9.52) * mm, "end": v(18.42, 1.9) * mm, "construction": true});
            skLineSegment(sketch, "E163", {"start": v(3.18, 1.9) * mm, "end": v(18.42, 1.9) * mm, "construction": true});
            skLineSegment(sketch, "E164.0", {"start": v(10.8, 6.83) * mm, "end": v(15.72, 1.9) * mm});
            skLineSegment(sketch, "E164.1", {"start": v(5.87, 1.9) * mm, "end": v(10.8, 6.83) * mm});
            skLineSegment(sketch, "E165.0", {"start": v(13.49, 9.53) * mm, "end": v(18.42, 4.6) * mm});
            skLineSegment(sketch, "E165.1", {"start": v(3.18, 4.6) * mm, "end": v(8.1, 9.53) * mm});
            skLineSegment(sketch, "E166.trimOffspring", {"start": v(8.1, 9.52) * mm, "end": v(3.17, 9.52) * mm});
            skLineSegment(sketch, "E167", {"start": v(8.1, 9.52) * mm, "end": v(13.49, 9.53) * mm, "construction": true});
            skLineSegment(sketch, "E168", {"start": v(18.42, 1.9) * mm, "end": v(18.42, 4.6) * mm, "construction": true});
            skLineSegment(sketch, "E169", {"start": v(18.42, 4.6) * mm, "end": v(18.42, 9.52) * mm, "construction": true});
            skLineSegment(sketch, "E170", {"start": v(10.8, 9.52) * mm, "end": v(10.8, 1.9) * mm, "construction": true});
            skLineSegment(sketch, "E171", {"start": v(3.17, 11.43) * mm, "end": v(18.42, 11.43) * mm, "construction": true});
            skLineSegment(sketch, "E172", {"start": v(3.18, 0) * mm, "end": v(18.42, 0) * mm, "construction": true});
            skLineSegment(sketch, "E173", {"start": v(18.42, 11.43) * mm, "end": v(18.42, 9.52) * mm, "construction": true});
            skLineSegment(sketch, "E174", {"start": v(18.42, 0) * mm, "end": v(18.42, 1.9) * mm, "construction": true});
            skLineSegment(sketch, "E175", {"start": v(13.26, 4.37) * mm, "end": v(14.6, 5.71) * mm, "construction": true});
            skLineSegment(sketch, "E176", {"start": v(5.87, 1.9) * mm, "end": v(15.72, 1.9) * mm});
            skLineSegment(sketch, "E177", {"start": v(3.18, 4.6) * mm, "end": v(3.18, 9.52) * mm});
            skLineSegment(sketch, "E178.MirrorCS", {"start": v(33.66, 4.6) * mm, "end": v(33.66, 9.52) * mm, "construction": true});
            skLineSegment(sketch, "E179.MirrorCS", {"start": v(28.73, 9.52) * mm, "end": v(33.66, 9.52) * mm});
            skLineSegment(sketch, "E180.MirrorCS", {"start": v(33.66, 4.6) * mm, "end": v(28.73, 9.53) * mm});
            skLineSegment(sketch, "E181.MirrorCS", {"start": v(30.96, 1.9) * mm, "end": v(21.1, 1.9) * mm});
            skLineSegment(sketch, "E182.MirrorCS", {"start": v(30.96, 1.9) * mm, "end": v(26.04, 6.83) * mm});
            skLineSegment(sketch, "E183.MirrorCS", {"start": v(26.04, 6.83) * mm, "end": v(21.1, 1.9) * mm});
            skLineSegment(sketch, "E184.MirrorCS", {"start": v(18.42, 9.52) * mm, "end": v(23.34, 9.52) * mm});
            skLineSegment(sketch, "E185.MirrorCS", {"start": v(23.34, 9.53) * mm, "end": v(18.41, 4.6) * mm});
            skLineSegment(sketch, "E186.MirrorCS", {"start": v(38.58, 9.53) * mm, "end": v(33.66, 9.52) * mm});
            skLineSegment(sketch, "E187.MirrorCS", {"start": v(33.65, 4.6) * mm, "end": v(38.58, 9.53) * mm});
            skLineSegment(sketch, "E188.MirrorCS", {"start": v(36.35, 1.9) * mm, "end": v(46.2, 1.9) * mm});
            skLineSegment(sketch, "E189.MirrorCS", {"start": v(36.35, 1.9) * mm, "end": v(41.27, 6.83) * mm});
            skLineSegment(sketch, "E190.MirrorCS", {"start": v(41.28, 6.83) * mm, "end": v(46.2, 1.9) * mm});
            skLineSegment(sketch, "E191.MirrorCS", {"start": v(43.97, 9.53) * mm, "end": v(48.9, 4.6) * mm});
            skLineSegment(sketch, "E192.MirrorCS", {"start": v(48.9, 9.53) * mm, "end": v(43.97, 9.53) * mm});
            skLineSegment(sketch, "E193", {"start": v(48.9, 9.53) * mm, "end": v(48.9, 4.6) * mm, "construction": true});
            skLineSegment(sketch, "E194.MirrorCS", {"start": v(3.18, 18.26) * mm, "end": v(3.18, 13.34) * mm});
            skLineSegment(sketch, "E195.MirrorCS", {"start": v(8.1, 13.34) * mm, "end": v(3.17, 13.34) * mm});
            skLineSegment(sketch, "E196.MirrorCS", {"start": v(3.17, 18.26) * mm, "end": v(8.1, 13.33) * mm});
            skLineSegment(sketch, "E197.MirrorCS", {"start": v(5.87, 20.95) * mm, "end": v(10.8, 16.03) * mm});
            skLineSegment(sketch, "E198.MirrorCS", {"start": v(10.8, 16.03) * mm, "end": v(15.72, 20.96) * mm});
            skLineSegment(sketch, "E199.MirrorCS", {"start": v(5.87, 20.95) * mm, "end": v(15.72, 20.96) * mm});
            skLineSegment(sketch, "E200.MirrorCS", {"start": v(13.49, 13.33) * mm, "end": v(18.41, 18.26) * mm});
            skLineSegment(sketch, "E201.MirrorCS", {"start": v(18.41, 13.34) * mm, "end": v(13.49, 13.34) * mm});
            skLineSegment(sketch, "E202.MirrorCS", {"start": v(18.41, 13.34) * mm, "end": v(23.34, 13.34) * mm});
            skLineSegment(sketch, "E203.MirrorCS", {"start": v(23.34, 13.33) * mm, "end": v(18.41, 18.26) * mm});
            skLineSegment(sketch, "E204.MirrorCS", {"start": v(26.04, 16.03) * mm, "end": v(21.1, 20.95) * mm});
            skLineSegment(sketch, "E205.MirrorCS", {"start": v(30.96, 20.96) * mm, "end": v(21.1, 20.96) * mm});
            skLineSegment(sketch, "E206.MirrorCS", {"start": v(30.96, 20.95) * mm, "end": v(26.04, 16.03) * mm});
            skLineSegment(sketch, "E207.MirrorCS", {"start": v(33.66, 18.26) * mm, "end": v(28.73, 13.33) * mm});
            skLineSegment(sketch, "E208.MirrorCS", {"start": v(28.73, 13.34) * mm, "end": v(33.66, 13.34) * mm});
            skLineSegment(sketch, "E209.MirrorCS", {"start": v(38.58, 13.34) * mm, "end": v(33.66, 13.34) * mm});
            skLineSegment(sketch, "E210.MirrorCS", {"start": v(33.65, 18.26) * mm, "end": v(38.58, 13.33) * mm});
            skLineSegment(sketch, "E211.MirrorCS", {"start": v(41.28, 16.03) * mm, "end": v(46.2, 20.95) * mm});
            skLineSegment(sketch, "E212.MirrorCS", {"start": v(36.35, 20.95) * mm, "end": v(41.27, 16.03) * mm});
            skLineSegment(sketch, "E213.MirrorCS", {"start": v(36.35, 20.96) * mm, "end": v(46.2, 20.96) * mm});
            skLineSegment(sketch, "E214.MirrorCS", {"start": v(43.97, 13.33) * mm, "end": v(48.9, 18.26) * mm});
            skLineSegment(sketch, "E215.MirrorCS", {"start": v(48.9, 13.34) * mm, "end": v(43.97, 13.34) * mm});
            skLineSegment(sketch, "E216.MirrorCS", {"start": v(48.9, 13.33) * mm, "end": v(48.9, 18.26) * mm, "construction": true});
            skLineSegment(sketch, "E217.MirrorCS", {"start": v(53.82, 9.53) * mm, "end": v(48.9, 4.6) * mm});
            skLineSegment(sketch, "E218.MirrorCS", {"start": v(48.9, 9.53) * mm, "end": v(53.82, 9.53) * mm});
            skLineSegment(sketch, "E219.MirrorCS", {"start": v(48.9, 13.34) * mm, "end": v(53.82, 13.34) * mm});
            skLineSegment(sketch, "E220.MirrorCS", {"start": v(53.82, 13.33) * mm, "end": v(48.9, 18.26) * mm});
            skLineSegment(sketch, "E221.MirrorCS", {"start": v(56.52, 16.03) * mm, "end": v(51.59, 20.96) * mm});
            skLineSegment(sketch, "E222.MirrorCS", {"start": v(61.44, 20.96) * mm, "end": v(51.59, 20.96) * mm});
            skLineSegment(sketch, "E223.MirrorCS", {"start": v(61.44, 20.95) * mm, "end": v(56.52, 16.03) * mm});
            skLineSegment(sketch, "E224.MirrorCS", {"start": v(64.14, 18.26) * mm, "end": v(59.2, 13.33) * mm});
            skLineSegment(sketch, "E225.MirrorCS", {"start": v(59.2, 13.34) * mm, "end": v(64.14, 13.34) * mm});
            skLineSegment(sketch, "E226.MirrorCS", {"start": v(59.2, 9.53) * mm, "end": v(64.14, 9.53) * mm});
            skLineSegment(sketch, "E227.MirrorCS", {"start": v(64.14, 4.6) * mm, "end": v(59.2, 9.53) * mm});
            skLineSegment(sketch, "E228.MirrorCS", {"start": v(56.52, 6.83) * mm, "end": v(51.59, 1.9) * mm});
            skLineSegment(sketch, "E229.MirrorCS", {"start": v(61.44, 1.9) * mm, "end": v(56.52, 6.83) * mm});
            skLineSegment(sketch, "E230.MirrorCS", {"start": v(61.44, 1.9) * mm, "end": v(51.59, 1.9) * mm});
            skLineSegment(sketch, "E231", {"start": v(64.14, 18.26) * mm, "end": v(64.14, 13.34) * mm});
            skLineSegment(sketch, "E232", {"start": v(64.14, 9.53) * mm, "end": v(64.14, 4.6) * mm});
            skLineSegment(sketch, "E233", {"start": v(101.2, 0) * mm, "end": v(101.2, 18.7) * mm, "construction": true});
            skLineSegment(sketch, "E234.MirrorCS", {"start": v(153.5, 9.52) * mm, "end": v(153.5, 4.6) * mm, "construction": true});
            skLineSegment(sketch, "E235.MirrorCS", {"start": v(153.5, 13.34) * mm, "end": v(153.5, 18.26) * mm, "construction": true});
            skLineSegment(sketch, "E236.MirrorCS", {"start": v(168.73, 4.6) * mm, "end": v(168.73, 9.53) * mm, "construction": true});
            skLineSegment(sketch, "E237.MirrorCS", {"start": v(138.25, 4.6) * mm, "end": v(143.18, 9.53) * mm});
            skLineSegment(sketch, "E238.MirrorCS", {"start": v(145.87, 16.03) * mm, "end": v(150.8, 20.95) * mm});
            skLineSegment(sketch, "E239.MirrorCS", {"start": v(138.25, 18.26) * mm, "end": v(138.25, 13.33) * mm});
            skLineSegment(sketch, "E240.MirrorCS", {"start": v(168.73, 18.26) * mm, "end": v(163.8, 13.34) * mm});
            skLineSegment(sketch, "E241.MirrorCS", {"start": v(143.18, 9.53) * mm, "end": v(138.25, 9.53) * mm});
            skLineSegment(sketch, "E242.MirrorCS", {"start": v(153.5, 9.53) * mm, "end": v(148.56, 9.53) * mm});
            skLineSegment(sketch, "E243.MirrorCS", {"start": v(153.5, 13.34) * mm, "end": v(148.56, 13.34) * mm});
            skLineSegment(sketch, "E244.MirrorCS", {"start": v(138.25, 9.53) * mm, "end": v(138.25, 4.6) * mm});
            skLineSegment(sketch, "E245.MirrorCS", {"start": v(158.42, 13.34) * mm, "end": v(153.5, 18.26) * mm});
            skLineSegment(sketch, "E246.MirrorCS", {"start": v(148.56, 9.53) * mm, "end": v(153.5, 4.6) * mm});
            skLineSegment(sketch, "E247.MirrorCS", {"start": v(163.8, 9.53) * mm, "end": v(168.73, 9.53) * mm});
            skLineSegment(sketch, "E248.MirrorCS", {"start": v(163.8, 13.34) * mm, "end": v(168.73, 13.34) * mm});
            skLineSegment(sketch, "E249.MirrorCS", {"start": v(138.25, 18.26) * mm, "end": v(143.18, 13.34) * mm});
            skLineSegment(sketch, "E250.MirrorCS", {"start": v(143.18, 13.34) * mm, "end": v(138.25, 13.34) * mm});
            skLineSegment(sketch, "E251.MirrorCS", {"start": v(148.56, 13.34) * mm, "end": v(153.5, 18.26) * mm});
            skLineSegment(sketch, "E252.MirrorCS", {"start": v(153.5, 9.53) * mm, "end": v(158.42, 9.53) * mm});
            skLineSegment(sketch, "E253.MirrorCS", {"start": v(153.5, 13.34) * mm, "end": v(158.42, 13.34) * mm});
            skLineSegment(sketch, "E254.MirrorCS", {"start": v(140.94, 20.96) * mm, "end": v(145.87, 16.03) * mm});
            skLineSegment(sketch, "E255.MirrorCS", {"start": v(161.11, 16.03) * mm, "end": v(156.18, 20.96) * mm});
            skLineSegment(sketch, "E256.MirrorCS", {"start": v(161.11, 6.83) * mm, "end": v(156.18, 1.9) * mm});
            skLineSegment(sketch, "E257.MirrorCS", {"start": v(145.87, 6.83) * mm, "end": v(150.8, 1.9) * mm});
            skLineSegment(sketch, "E258.MirrorCS", {"start": v(166.04, 1.9) * mm, "end": v(156.18, 1.9) * mm});
            skLineSegment(sketch, "E259.MirrorCS", {"start": v(140.94, 1.9) * mm, "end": v(145.87, 6.83) * mm});
            skLineSegment(sketch, "E260.MirrorCS", {"start": v(140.94, 20.96) * mm, "end": v(150.8, 20.96) * mm});
            skLineSegment(sketch, "E261.MirrorCS", {"start": v(158.42, 9.53) * mm, "end": v(153.5, 4.6) * mm});
            skLineSegment(sketch, "E262.MirrorCS", {"start": v(166.04, 20.96) * mm, "end": v(156.18, 20.96) * mm});
            skLineSegment(sketch, "E263.MirrorCS", {"start": v(168.73, 4.6) * mm, "end": v(163.8, 9.53) * mm});
            skLineSegment(sketch, "E264.MirrorCS", {"start": v(140.94, 1.9) * mm, "end": v(150.8, 1.9) * mm});
            skLineSegment(sketch, "E265.MirrorCS", {"start": v(166.04, 1.9) * mm, "end": v(161.11, 6.83) * mm});
            skLineSegment(sketch, "E266.MirrorCS", {"start": v(166.04, 20.96) * mm, "end": v(161.11, 16.03) * mm});
            skLineSegment(sketch, "E267", {"start": v(161.11, 16.03) * mm, "end": v(161.11, 20.96) * mm});
            skLineSegment(sketch, "E268", {"start": v(168.73, 9.53) * mm, "end": v(168.73, 4.6) * mm});
            skLineSegment(sketch, "E269", {"start": v(168.73, 13.33) * mm, "end": v(168.73, 18.26) * mm});
            skPoint(sketch, "E270.MirrorCS.end.orphan", {"position": v(173.66, 13.33) * mm});
            skPoint(sketch, "E270.MirrorCS.start.orphan", {"position": v(168.73, 18.26) * mm});
            skPoint(sketch, "E271.MirrorCS.end.orphan", {"position": v(168.73, 9.53) * mm});
            skPoint(sketch, "E272.MirrorCS.end.orphan", {"position": v(173.66, 9.53) * mm});
            skLineSegment(sketch, "E273", {"start": v(161.11, 6.83) * mm, "end": v(161.11, 1.9) * mm});
            skSolve(sketch);
        }
        {
            var Q0;
            Q0 = qSketchRegion(id + "F26", true);
            extrude(context, id + "F27", {"entities" : qUnion([Q0]), "operationType" : NewBodyOperationType.REMOVE, "endBound" : BoundingType.UP_TO_NEXT, "oppositeDirection" : true, "depth" : 25.4 * mm, "offsetDistance" : 25.4 * mm});
        }
        {
            var Q0;
            Q0=makeQuery(id+"F6.boolean.opBoolean","MERGE",FACE,{"derivedFrom":[makeQuery(id+"F2.opExtrude","SWEPT_FACE",FACE,{"disambiguationData":[OSD([sQuery(id+"F1.wireOp",EDGE,"E9.2")])]}),makeQuery(id+"F6.opExtrude","SWEPT_FACE",FACE,{"disambiguationData":[OSD([sQuery(id+"F5.wireOp",EDGE,"E60.top")])]})]});
            var sketch = newSketch(context, id + "F28", { "sketchPlane" : qUnion([Q0])});
            skLineSegment(sketch, "E274.3", {"start": v(3.17, 18.26) * mm, "end": v(8.1, 13.33) * mm});
            skLineSegment(sketch, "E274.4", {"start": v(3.18, 18.26) * mm, "end": v(3.18, 13.33) * mm, "construction": true});
            skLineSegment(sketch, "E274.5", {"start": v(8.1, 13.34) * mm, "end": v(3.18, 13.34) * mm});
            skLineSegment(sketch, "E274.12", {"start": v(5.87, 1.9) * mm, "end": v(15.72, 1.9) * mm});
            skLineSegment(sketch, "E275.MirrorCS", {"start": v(0.48, 20.95) * mm, "end": v(-4.44, 16.03) * mm});
            skLineSegment(sketch, "E276.MirrorCS", {"start": v(-1.75, 13.34) * mm, "end": v(3.17, 13.34) * mm});
            skLineSegment(sketch, "E277.MirrorCS", {"start": v(3.18, 18.26) * mm, "end": v(-1.75, 13.33) * mm});
            skLineSegment(sketch, "E278", {"start": v(-4.44, 16.03) * mm, "end": v(-4.44, 20.95) * mm});
            skLineSegment(sketch, "E279", {"start": v(-4.44, 20.95) * mm, "end": v(0.48, 20.95) * mm});
            skLineSegment(sketch, "E280.0.1.0", {"start": v(3.17, 41.12) * mm, "end": v(8.1, 36.2) * mm});
            skLineSegment(sketch, "E280.0.1.1", {"start": v(8.1, 36.2) * mm, "end": v(3.18, 36.2) * mm});
            skLineSegment(sketch, "E280.0.1.2", {"start": v(3.18, 41.12) * mm, "end": v(-1.75, 36.2) * mm});
            skLineSegment(sketch, "E280.0.1.3", {"start": v(-1.75, 36.2) * mm, "end": v(3.18, 36.2) * mm});
            skLineSegment(sketch, "E280.0.1.4", {"start": v(-1.75, 32.38) * mm, "end": v(3.17, 32.38) * mm});
            skLineSegment(sketch, "E280.0.1.5", {"start": v(3.18, 27.46) * mm, "end": v(-1.75, 32.39) * mm});
            skLineSegment(sketch, "E280.0.1.6", {"start": v(8.1, 32.38) * mm, "end": v(3.17, 32.38) * mm});
            skLineSegment(sketch, "E280.0.1.7", {"start": v(3.18, 27.46) * mm, "end": v(8.1, 32.39) * mm});
            skLineSegment(sketch, "E280.0.1.8", {"start": v(5.87, 24.77) * mm, "end": v(10.8, 29.7) * mm});
            skLineSegment(sketch, "E280.0.1.9", {"start": v(10.8, 29.7) * mm, "end": v(15.72, 24.76) * mm});
            skLineSegment(sketch, "E280.0.1.10", {"start": v(5.87, 24.76) * mm, "end": v(15.72, 24.76) * mm});
            skLineSegment(sketch, "E280.0.1.11", {"start": v(5.87, 43.81) * mm, "end": v(10.8, 38.89) * mm});
            skLineSegment(sketch, "E280.0.1.12", {"start": v(5.87, 43.81) * mm, "end": v(15.72, 43.81) * mm});
            skLineSegment(sketch, "E280.0.1.13", {"start": v(10.8, 38.89) * mm, "end": v(15.72, 43.81) * mm});
            skLineSegment(sketch, "E280.0.2.0", {"start": v(3.17, 63.98) * mm, "end": v(8.1, 59.05) * mm});
            skLineSegment(sketch, "E280.0.2.1", {"start": v(8.1, 59.05) * mm, "end": v(3.18, 59.05) * mm});
            skLineSegment(sketch, "E280.0.2.2", {"start": v(3.17, 63.98) * mm, "end": v(-1.75, 59.05) * mm});
            skLineSegment(sketch, "E280.0.2.3", {"start": v(-1.75, 59.05) * mm, "end": v(3.18, 59.05) * mm});
            skLineSegment(sketch, "E280.0.2.4", {"start": v(-1.75, 55.24) * mm, "end": v(3.17, 55.24) * mm});
            skLineSegment(sketch, "E280.0.2.5", {"start": v(3.18, 50.32) * mm, "end": v(-1.75, 55.24) * mm});
            skLineSegment(sketch, "E280.0.2.6", {"start": v(8.1, 55.24) * mm, "end": v(3.17, 55.24) * mm});
            skLineSegment(sketch, "E280.0.2.7", {"start": v(3.18, 50.32) * mm, "end": v(8.1, 55.25) * mm});
            skLineSegment(sketch, "E280.0.2.8", {"start": v(5.87, 47.62) * mm, "end": v(10.8, 52.55) * mm});
            skLineSegment(sketch, "E280.0.2.9", {"start": v(10.8, 52.55) * mm, "end": v(15.72, 47.62) * mm});
            skLineSegment(sketch, "E280.0.2.10", {"start": v(5.87, 47.62) * mm, "end": v(15.72, 47.62) * mm});
            skLineSegment(sketch, "E280.0.2.11", {"start": v(5.87, 66.67) * mm, "end": v(10.8, 61.75) * mm});
            skLineSegment(sketch, "E280.0.2.12", {"start": v(5.87, 66.67) * mm, "end": v(15.72, 66.67) * mm});
            skLineSegment(sketch, "E280.0.2.13", {"start": v(10.8, 61.75) * mm, "end": v(15.72, 66.67) * mm});
            skLineSegment(sketch, "E280.1.1.0", {"start": v(18.41, 41.12) * mm, "end": v(23.34, 36.2) * mm});
            skLineSegment(sketch, "E280.1.1.1", {"start": v(23.34, 36.2) * mm, "end": v(18.41, 36.2) * mm});
            skLineSegment(sketch, "E280.1.1.2", {"start": v(18.41, 41.12) * mm, "end": v(13.49, 36.2) * mm});
            skLineSegment(sketch, "E280.1.1.3", {"start": v(13.49, 36.2) * mm, "end": v(18.41, 36.2) * mm});
            skLineSegment(sketch, "E280.1.1.4", {"start": v(13.49, 32.38) * mm, "end": v(18.41, 32.38) * mm});
            skLineSegment(sketch, "E280.1.1.5", {"start": v(18.41, 27.46) * mm, "end": v(13.49, 32.39) * mm});
            skLineSegment(sketch, "E280.1.1.6", {"start": v(23.34, 32.38) * mm, "end": v(18.41, 32.38) * mm});
            skLineSegment(sketch, "E280.1.1.7", {"start": v(18.41, 27.46) * mm, "end": v(23.34, 32.39) * mm});
            skLineSegment(sketch, "E280.1.1.8", {"start": v(21.1, 24.77) * mm, "end": v(26.03, 29.7) * mm});
            skLineSegment(sketch, "E280.1.1.9", {"start": v(26.03, 29.7) * mm, "end": v(30.96, 24.76) * mm});
            skLineSegment(sketch, "E280.1.1.10", {"start": v(21.1, 24.76) * mm, "end": v(30.96, 24.76) * mm});
            skLineSegment(sketch, "E280.1.1.11", {"start": v(21.1, 43.81) * mm, "end": v(26.03, 38.89) * mm});
            skLineSegment(sketch, "E280.1.1.12", {"start": v(21.1, 43.81) * mm, "end": v(30.96, 43.81) * mm});
            skLineSegment(sketch, "E280.1.1.13", {"start": v(26.03, 38.89) * mm, "end": v(30.96, 43.81) * mm});
            skLineSegment(sketch, "E280.1.2.0", {"start": v(18.41, 63.98) * mm, "end": v(23.34, 59.05) * mm});
            skLineSegment(sketch, "E280.1.2.1", {"start": v(23.34, 59.05) * mm, "end": v(18.41, 59.05) * mm});
            skLineSegment(sketch, "E280.1.2.2", {"start": v(18.41, 63.98) * mm, "end": v(13.49, 59.05) * mm});
            skLineSegment(sketch, "E280.1.2.3", {"start": v(13.49, 59.05) * mm, "end": v(18.41, 59.05) * mm});
            skLineSegment(sketch, "E280.1.2.4", {"start": v(13.49, 55.24) * mm, "end": v(18.41, 55.24) * mm});
            skLineSegment(sketch, "E280.1.2.5", {"start": v(18.41, 50.32) * mm, "end": v(13.49, 55.24) * mm});
            skLineSegment(sketch, "E280.1.2.6", {"start": v(23.34, 55.24) * mm, "end": v(18.41, 55.24) * mm});
            skLineSegment(sketch, "E280.1.2.7", {"start": v(18.41, 50.32) * mm, "end": v(23.34, 55.25) * mm});
            skLineSegment(sketch, "E280.1.2.8", {"start": v(21.1, 47.62) * mm, "end": v(26.03, 52.55) * mm});
            skLineSegment(sketch, "E280.1.2.9", {"start": v(26.03, 52.55) * mm, "end": v(30.96, 47.62) * mm});
            skLineSegment(sketch, "E280.1.2.10", {"start": v(21.1, 47.62) * mm, "end": v(30.96, 47.62) * mm});
            skLineSegment(sketch, "E280.1.2.11", {"start": v(21.1, 66.67) * mm, "end": v(26.03, 61.75) * mm});
            skLineSegment(sketch, "E280.1.2.12", {"start": v(21.1, 66.67) * mm, "end": v(30.96, 66.67) * mm});
            skLineSegment(sketch, "E280.1.2.13", {"start": v(26.03, 61.75) * mm, "end": v(30.96, 66.67) * mm});
            skLineSegment(sketch, "E280.2.1.0", {"start": v(33.65, 41.12) * mm, "end": v(38.58, 36.2) * mm});
            skLineSegment(sketch, "E280.2.1.1", {"start": v(38.58, 36.2) * mm, "end": v(33.65, 36.2) * mm});
            skLineSegment(sketch, "E280.2.1.2", {"start": v(33.65, 41.12) * mm, "end": v(28.73, 36.2) * mm});
            skLineSegment(sketch, "E280.2.1.3", {"start": v(28.73, 36.2) * mm, "end": v(33.65, 36.2) * mm});
            skLineSegment(sketch, "E280.2.1.4", {"start": v(28.73, 32.38) * mm, "end": v(33.65, 32.38) * mm});
            skLineSegment(sketch, "E280.2.1.5", {"start": v(33.65, 27.46) * mm, "end": v(28.73, 32.39) * mm});
            skLineSegment(sketch, "E280.2.1.6", {"start": v(38.58, 32.38) * mm, "end": v(33.65, 32.38) * mm});
            skLineSegment(sketch, "E280.2.1.7", {"start": v(33.65, 27.46) * mm, "end": v(38.58, 32.39) * mm});
            skLineSegment(sketch, "E280.2.1.8", {"start": v(36.35, 24.77) * mm, "end": v(41.27, 29.7) * mm});
            skLineSegment(sketch, "E280.2.1.9", {"start": v(41.27, 29.7) * mm, "end": v(46.2, 24.76) * mm});
            skLineSegment(sketch, "E280.2.1.10", {"start": v(36.35, 24.76) * mm, "end": v(46.2, 24.76) * mm});
            skLineSegment(sketch, "E280.2.1.11", {"start": v(36.35, 43.81) * mm, "end": v(41.27, 38.89) * mm});
            skLineSegment(sketch, "E280.2.1.12", {"start": v(36.35, 43.81) * mm, "end": v(46.2, 43.81) * mm});
            skLineSegment(sketch, "E280.2.1.13", {"start": v(41.27, 38.89) * mm, "end": v(46.2, 43.81) * mm});
            skLineSegment(sketch, "E280.2.2.0", {"start": v(33.65, 63.98) * mm, "end": v(38.58, 59.05) * mm});
            skLineSegment(sketch, "E280.2.2.1", {"start": v(38.58, 59.05) * mm, "end": v(33.65, 59.05) * mm});
            skLineSegment(sketch, "E280.2.2.2", {"start": v(33.65, 63.98) * mm, "end": v(28.73, 59.05) * mm});
            skLineSegment(sketch, "E280.2.2.3", {"start": v(28.73, 59.05) * mm, "end": v(33.65, 59.05) * mm});
            skLineSegment(sketch, "E280.2.2.4", {"start": v(28.73, 55.24) * mm, "end": v(33.65, 55.24) * mm});
            skLineSegment(sketch, "E280.2.2.5", {"start": v(33.65, 50.32) * mm, "end": v(28.73, 55.24) * mm});
            skLineSegment(sketch, "E280.2.2.6", {"start": v(38.58, 55.24) * mm, "end": v(33.65, 55.24) * mm});
            skLineSegment(sketch, "E280.2.2.7", {"start": v(33.65, 50.32) * mm, "end": v(38.58, 55.25) * mm});
            skLineSegment(sketch, "E280.2.2.8", {"start": v(36.35, 47.62) * mm, "end": v(41.27, 52.55) * mm});
            skLineSegment(sketch, "E280.2.2.9", {"start": v(41.27, 52.55) * mm, "end": v(46.2, 47.62) * mm});
            skLineSegment(sketch, "E280.2.2.10", {"start": v(36.35, 47.62) * mm, "end": v(46.2, 47.62) * mm});
            skLineSegment(sketch, "E280.2.2.11", {"start": v(36.35, 66.67) * mm, "end": v(41.27, 61.75) * mm});
            skLineSegment(sketch, "E280.2.2.12", {"start": v(36.35, 66.67) * mm, "end": v(46.2, 66.67) * mm});
            skLineSegment(sketch, "E280.2.2.13", {"start": v(41.27, 61.75) * mm, "end": v(46.2, 66.67) * mm});
            skLineSegment(sketch, "E280.3.1.0", {"start": v(48.9, 41.12) * mm, "end": v(53.82, 36.2) * mm});
            skLineSegment(sketch, "E280.3.1.1", {"start": v(53.82, 36.2) * mm, "end": v(48.9, 36.2) * mm});
            skLineSegment(sketch, "E280.3.1.2", {"start": v(48.9, 41.12) * mm, "end": v(43.97, 36.2) * mm});
            skLineSegment(sketch, "E280.3.1.3", {"start": v(43.97, 36.2) * mm, "end": v(48.9, 36.2) * mm});
            skLineSegment(sketch, "E280.3.1.4", {"start": v(43.97, 32.38) * mm, "end": v(48.9, 32.38) * mm});
            skLineSegment(sketch, "E280.3.1.5", {"start": v(48.9, 27.46) * mm, "end": v(43.97, 32.39) * mm});
            skLineSegment(sketch, "E280.3.1.6", {"start": v(53.82, 32.38) * mm, "end": v(48.9, 32.38) * mm});
            skLineSegment(sketch, "E280.3.1.7", {"start": v(48.9, 27.46) * mm, "end": v(53.82, 32.39) * mm});
            skLineSegment(sketch, "E280.3.1.8", {"start": v(51.59, 24.77) * mm, "end": v(56.51, 29.7) * mm});
            skLineSegment(sketch, "E280.3.1.9", {"start": v(56.51, 29.7) * mm, "end": v(61.44, 24.76) * mm});
            skLineSegment(sketch, "E280.3.1.10", {"start": v(51.59, 24.76) * mm, "end": v(61.44, 24.76) * mm});
            skLineSegment(sketch, "E280.3.1.11", {"start": v(51.59, 43.81) * mm, "end": v(56.51, 38.89) * mm});
            skLineSegment(sketch, "E280.3.1.12", {"start": v(51.59, 43.81) * mm, "end": v(61.44, 43.81) * mm});
            skLineSegment(sketch, "E280.3.1.13", {"start": v(56.51, 38.89) * mm, "end": v(61.44, 43.81) * mm});
            skLineSegment(sketch, "E280.3.2.0", {"start": v(48.9, 63.98) * mm, "end": v(53.82, 59.05) * mm});
            skLineSegment(sketch, "E280.3.2.1", {"start": v(53.82, 59.05) * mm, "end": v(48.9, 59.05) * mm});
            skLineSegment(sketch, "E280.3.2.2", {"start": v(48.9, 63.98) * mm, "end": v(43.97, 59.05) * mm});
            skLineSegment(sketch, "E280.3.2.3", {"start": v(43.97, 59.05) * mm, "end": v(48.9, 59.05) * mm});
            skLineSegment(sketch, "E280.3.2.4", {"start": v(43.97, 55.24) * mm, "end": v(48.9, 55.24) * mm});
            skLineSegment(sketch, "E280.3.2.5", {"start": v(48.9, 50.32) * mm, "end": v(43.97, 55.24) * mm});
            skLineSegment(sketch, "E280.3.2.6", {"start": v(53.82, 55.24) * mm, "end": v(48.9, 55.24) * mm});
            skLineSegment(sketch, "E280.3.2.7", {"start": v(48.9, 50.32) * mm, "end": v(53.82, 55.24) * mm});
            skLineSegment(sketch, "E280.3.2.8", {"start": v(51.59, 47.62) * mm, "end": v(56.51, 52.55) * mm});
            skLineSegment(sketch, "E280.3.2.9", {"start": v(56.51, 52.55) * mm, "end": v(61.44, 47.62) * mm});
            skLineSegment(sketch, "E280.3.2.10", {"start": v(51.59, 47.62) * mm, "end": v(61.44, 47.62) * mm});
            skLineSegment(sketch, "E280.3.2.11", {"start": v(51.59, 66.67) * mm, "end": v(56.51, 61.75) * mm});
            skLineSegment(sketch, "E280.3.2.12", {"start": v(51.59, 66.67) * mm, "end": v(61.44, 66.67) * mm});
            skLineSegment(sketch, "E280.3.2.13", {"start": v(56.51, 61.75) * mm, "end": v(61.44, 66.67) * mm});
            skLineSegment(sketch, "E280.4.1.0", {"start": v(64.13, 41.12) * mm, "end": v(69.06, 36.2) * mm});
            skLineSegment(sketch, "E280.4.1.1", {"start": v(69.06, 36.2) * mm, "end": v(64.13, 36.2) * mm});
            skLineSegment(sketch, "E280.4.1.2", {"start": v(64.13, 41.12) * mm, "end": v(59.2, 36.2) * mm});
            skLineSegment(sketch, "E280.4.1.3", {"start": v(59.2, 36.2) * mm, "end": v(64.13, 36.2) * mm});
            skLineSegment(sketch, "E280.4.1.4", {"start": v(59.2, 32.38) * mm, "end": v(64.13, 32.38) * mm});
            skLineSegment(sketch, "E280.4.1.5", {"start": v(64.13, 27.46) * mm, "end": v(59.2, 32.39) * mm});
            skLineSegment(sketch, "E280.4.1.6", {"start": v(69.06, 32.38) * mm, "end": v(64.13, 32.38) * mm});
            skLineSegment(sketch, "E280.4.1.7", {"start": v(64.13, 27.46) * mm, "end": v(69.06, 32.39) * mm});
            skLineSegment(sketch, "E280.4.1.8", {"start": v(66.83, 24.77) * mm, "end": v(71.75, 29.7) * mm});
            skLineSegment(sketch, "E280.4.1.9", {"start": v(71.75, 29.7) * mm, "end": v(76.68, 24.76) * mm});
            skLineSegment(sketch, "E280.4.1.10", {"start": v(66.83, 24.76) * mm, "end": v(76.68, 24.76) * mm});
            skLineSegment(sketch, "E280.4.1.11", {"start": v(66.83, 43.81) * mm, "end": v(71.75, 38.89) * mm});
            skLineSegment(sketch, "E280.4.1.12", {"start": v(66.83, 43.81) * mm, "end": v(76.68, 43.81) * mm});
            skLineSegment(sketch, "E280.4.1.13", {"start": v(71.75, 38.89) * mm, "end": v(76.68, 43.81) * mm});
            skLineSegment(sketch, "E280.4.2.0", {"start": v(64.13, 63.98) * mm, "end": v(69.06, 59.05) * mm});
            skLineSegment(sketch, "E280.4.2.1", {"start": v(69.06, 59.05) * mm, "end": v(64.13, 59.05) * mm});
            skLineSegment(sketch, "E280.4.2.2", {"start": v(64.13, 63.98) * mm, "end": v(59.2, 59.05) * mm});
            skLineSegment(sketch, "E280.4.2.3", {"start": v(59.2, 59.05) * mm, "end": v(64.13, 59.05) * mm});
            skLineSegment(sketch, "E280.4.2.4", {"start": v(59.2, 55.24) * mm, "end": v(64.13, 55.24) * mm});
            skLineSegment(sketch, "E280.4.2.5", {"start": v(64.13, 50.32) * mm, "end": v(59.2, 55.24) * mm});
            skLineSegment(sketch, "E280.4.2.6", {"start": v(69.06, 55.24) * mm, "end": v(64.13, 55.24) * mm});
            skLineSegment(sketch, "E280.4.2.7", {"start": v(64.13, 50.32) * mm, "end": v(69.06, 55.25) * mm});
            skLineSegment(sketch, "E280.4.2.8", {"start": v(66.83, 47.62) * mm, "end": v(71.75, 52.55) * mm});
            skLineSegment(sketch, "E280.4.2.9", {"start": v(71.75, 52.55) * mm, "end": v(76.68, 47.62) * mm});
            skLineSegment(sketch, "E280.4.2.10", {"start": v(66.83, 47.62) * mm, "end": v(76.68, 47.62) * mm});
            skLineSegment(sketch, "E280.4.2.11", {"start": v(66.83, 66.67) * mm, "end": v(71.75, 61.75) * mm});
            skLineSegment(sketch, "E280.4.2.12", {"start": v(66.83, 66.67) * mm, "end": v(76.68, 66.67) * mm});
            skLineSegment(sketch, "E280.4.2.13", {"start": v(71.75, 61.75) * mm, "end": v(76.68, 66.67) * mm});
            skLineSegment(sketch, "E280.5.0.0", {"start": v(79.37, 18.26) * mm, "end": v(84.3, 13.33) * mm});
            skLineSegment(sketch, "E280.5.0.1", {"start": v(84.3, 13.34) * mm, "end": v(79.38, 13.34) * mm});
            skLineSegment(sketch, "E280.5.0.2", {"start": v(79.38, 18.26) * mm, "end": v(74.45, 13.33) * mm});
            skLineSegment(sketch, "E280.5.0.3", {"start": v(74.45, 13.34) * mm, "end": v(79.38, 13.34) * mm});
            skLineSegment(sketch, "E280.5.0.4", {"start": v(74.45, 9.52) * mm, "end": v(79.38, 9.52) * mm});
            skLineSegment(sketch, "E280.5.0.5", {"start": v(79.37, 4.6) * mm, "end": v(74.45, 9.53) * mm});
            skLineSegment(sketch, "E280.5.0.6", {"start": v(84.3, 9.52) * mm, "end": v(79.38, 9.52) * mm});
            skLineSegment(sketch, "E280.5.0.7", {"start": v(79.38, 4.6) * mm, "end": v(84.3, 9.53) * mm});
            skLineSegment(sketch, "E280.5.0.8", {"start": v(82.07, 1.9) * mm, "end": v(87, 6.83) * mm});
            skLineSegment(sketch, "E280.5.0.9", {"start": v(87, 6.83) * mm, "end": v(91.92, 1.9) * mm});
            skLineSegment(sketch, "E280.5.0.10", {"start": v(82.07, 1.9) * mm, "end": v(91.92, 1.9) * mm});
            skLineSegment(sketch, "E280.5.0.11", {"start": v(82.07, 20.95) * mm, "end": v(87, 16.03) * mm});
            skLineSegment(sketch, "E280.5.0.12", {"start": v(82.07, 20.95) * mm, "end": v(91.92, 20.96) * mm});
            skLineSegment(sketch, "E280.5.0.13", {"start": v(87, 16.03) * mm, "end": v(91.92, 20.96) * mm});
            skLineSegment(sketch, "E280.5.1.0", {"start": v(79.37, 41.12) * mm, "end": v(84.3, 36.2) * mm});
            skLineSegment(sketch, "E280.5.1.1", {"start": v(84.3, 36.2) * mm, "end": v(79.37, 36.2) * mm});
            skLineSegment(sketch, "E280.5.1.2", {"start": v(79.37, 41.12) * mm, "end": v(74.45, 36.2) * mm});
            skLineSegment(sketch, "E280.5.1.3", {"start": v(74.45, 36.2) * mm, "end": v(79.37, 36.2) * mm});
            skLineSegment(sketch, "E280.5.1.4", {"start": v(74.45, 32.38) * mm, "end": v(79.37, 32.38) * mm});
            skLineSegment(sketch, "E280.5.1.5", {"start": v(79.37, 27.46) * mm, "end": v(74.45, 32.39) * mm});
            skLineSegment(sketch, "E280.5.1.6", {"start": v(84.3, 32.38) * mm, "end": v(79.37, 32.38) * mm});
            skLineSegment(sketch, "E280.5.1.7", {"start": v(79.37, 27.46) * mm, "end": v(84.3, 32.39) * mm});
            skLineSegment(sketch, "E280.5.1.8", {"start": v(82.07, 24.77) * mm, "end": v(87, 29.7) * mm});
            skLineSegment(sketch, "E280.5.1.9", {"start": v(87, 29.7) * mm, "end": v(91.92, 24.76) * mm});
            skLineSegment(sketch, "E280.5.1.10", {"start": v(82.07, 24.76) * mm, "end": v(91.92, 24.76) * mm});
            skLineSegment(sketch, "E280.5.1.11", {"start": v(82.07, 43.81) * mm, "end": v(87, 38.89) * mm});
            skLineSegment(sketch, "E280.5.1.12", {"start": v(82.07, 43.81) * mm, "end": v(91.92, 43.81) * mm});
            skLineSegment(sketch, "E280.5.1.13", {"start": v(87, 38.89) * mm, "end": v(91.92, 43.81) * mm});
            skLineSegment(sketch, "E280.5.2.0", {"start": v(79.37, 63.98) * mm, "end": v(84.3, 59.05) * mm});
            skLineSegment(sketch, "E280.5.2.1", {"start": v(84.3, 59.05) * mm, "end": v(79.37, 59.05) * mm});
            skLineSegment(sketch, "E280.5.2.2", {"start": v(79.37, 63.98) * mm, "end": v(74.45, 59.05) * mm});
            skLineSegment(sketch, "E280.5.2.3", {"start": v(74.45, 59.05) * mm, "end": v(79.37, 59.05) * mm});
            skLineSegment(sketch, "E280.5.2.4", {"start": v(74.45, 55.24) * mm, "end": v(79.37, 55.24) * mm});
            skLineSegment(sketch, "E280.5.2.5", {"start": v(79.37, 50.32) * mm, "end": v(74.45, 55.24) * mm});
            skLineSegment(sketch, "E280.5.2.6", {"start": v(84.3, 55.24) * mm, "end": v(79.37, 55.24) * mm});
            skLineSegment(sketch, "E280.5.2.7", {"start": v(79.37, 50.32) * mm, "end": v(84.3, 55.25) * mm});
            skLineSegment(sketch, "E280.5.2.8", {"start": v(82.07, 47.62) * mm, "end": v(87, 52.55) * mm});
            skLineSegment(sketch, "E280.5.2.9", {"start": v(87, 52.55) * mm, "end": v(91.92, 47.62) * mm});
            skLineSegment(sketch, "E280.5.2.10", {"start": v(82.07, 47.62) * mm, "end": v(91.92, 47.62) * mm});
            skLineSegment(sketch, "E280.5.2.11", {"start": v(82.07, 66.67) * mm, "end": v(87, 61.75) * mm});
            skLineSegment(sketch, "E280.5.2.12", {"start": v(82.07, 66.67) * mm, "end": v(91.92, 66.67) * mm});
            skLineSegment(sketch, "E280.5.2.13", {"start": v(87, 61.75) * mm, "end": v(91.92, 66.67) * mm});
            skLineSegment(sketch, "E280.6.0.0", {"start": v(94.61, 18.26) * mm, "end": v(99.54, 13.33) * mm});
            skLineSegment(sketch, "E280.6.0.1", {"start": v(99.54, 13.34) * mm, "end": v(94.61, 13.34) * mm});
            skLineSegment(sketch, "E280.6.0.2", {"start": v(94.62, 18.26) * mm, "end": v(89.69, 13.33) * mm});
            skLineSegment(sketch, "E280.6.0.3", {"start": v(89.69, 13.34) * mm, "end": v(94.61, 13.34) * mm});
            skLineSegment(sketch, "E280.6.0.4", {"start": v(89.69, 9.52) * mm, "end": v(94.61, 9.52) * mm});
            skLineSegment(sketch, "E280.6.0.5", {"start": v(94.61, 4.6) * mm, "end": v(89.69, 9.53) * mm});
            skLineSegment(sketch, "E280.6.0.6", {"start": v(99.54, 9.52) * mm, "end": v(94.61, 9.52) * mm});
            skLineSegment(sketch, "E280.6.0.7", {"start": v(94.62, 4.6) * mm, "end": v(99.54, 9.53) * mm});
            skLineSegment(sketch, "E280.6.0.8", {"start": v(97.3, 1.9) * mm, "end": v(102.23, 6.83) * mm});
            skLineSegment(sketch, "E280.6.0.9", {"start": v(102.23, 6.83) * mm, "end": v(107.16, 1.9) * mm});
            skLineSegment(sketch, "E280.6.0.10", {"start": v(97.3, 1.9) * mm, "end": v(107.16, 1.9) * mm});
            skLineSegment(sketch, "E280.6.0.11", {"start": v(97.3, 20.95) * mm, "end": v(102.23, 16.03) * mm});
            skLineSegment(sketch, "E280.6.0.12", {"start": v(97.3, 20.95) * mm, "end": v(107.16, 20.96) * mm});
            skLineSegment(sketch, "E280.6.0.13", {"start": v(102.23, 16.03) * mm, "end": v(107.16, 20.96) * mm});
            skLineSegment(sketch, "E280.6.1.0", {"start": v(94.61, 41.12) * mm, "end": v(99.54, 36.2) * mm});
            skLineSegment(sketch, "E280.6.1.1", {"start": v(99.54, 36.2) * mm, "end": v(94.61, 36.2) * mm});
            skLineSegment(sketch, "E280.6.1.2", {"start": v(94.61, 41.12) * mm, "end": v(89.69, 36.2) * mm});
            skLineSegment(sketch, "E280.6.1.3", {"start": v(89.69, 36.2) * mm, "end": v(94.61, 36.2) * mm});
            skLineSegment(sketch, "E280.6.1.4", {"start": v(89.69, 32.38) * mm, "end": v(94.61, 32.38) * mm});
            skLineSegment(sketch, "E280.6.1.5", {"start": v(94.61, 27.46) * mm, "end": v(89.69, 32.38) * mm});
            skLineSegment(sketch, "E280.6.1.6", {"start": v(99.54, 32.38) * mm, "end": v(94.61, 32.38) * mm});
            skLineSegment(sketch, "E280.6.1.7", {"start": v(94.61, 27.46) * mm, "end": v(99.54, 32.39) * mm});
            skLineSegment(sketch, "E280.6.1.8", {"start": v(97.3, 24.77) * mm, "end": v(102.23, 29.7) * mm});
            skLineSegment(sketch, "E280.6.1.9", {"start": v(102.23, 29.7) * mm, "end": v(107.16, 24.76) * mm});
            skLineSegment(sketch, "E280.6.1.10", {"start": v(97.3, 24.76) * mm, "end": v(107.16, 24.76) * mm});
            skLineSegment(sketch, "E280.6.1.11", {"start": v(97.3, 43.81) * mm, "end": v(102.23, 38.89) * mm});
            skLineSegment(sketch, "E280.6.1.12", {"start": v(97.3, 43.81) * mm, "end": v(107.16, 43.81) * mm});
            skLineSegment(sketch, "E280.6.1.13", {"start": v(102.23, 38.89) * mm, "end": v(107.16, 43.81) * mm});
            skLineSegment(sketch, "E280.6.2.0", {"start": v(94.61, 63.98) * mm, "end": v(99.54, 59.05) * mm});
            skLineSegment(sketch, "E280.6.2.1", {"start": v(99.54, 59.05) * mm, "end": v(94.61, 59.05) * mm});
            skLineSegment(sketch, "E280.6.2.2", {"start": v(94.61, 63.98) * mm, "end": v(89.69, 59.05) * mm});
            skLineSegment(sketch, "E280.6.2.3", {"start": v(89.69, 59.05) * mm, "end": v(94.61, 59.05) * mm});
            skLineSegment(sketch, "E280.6.2.4", {"start": v(89.69, 55.24) * mm, "end": v(94.61, 55.24) * mm});
            skLineSegment(sketch, "E280.6.2.5", {"start": v(94.61, 50.32) * mm, "end": v(89.69, 55.24) * mm});
            skLineSegment(sketch, "E280.6.2.6", {"start": v(99.54, 55.24) * mm, "end": v(94.61, 55.24) * mm});
            skLineSegment(sketch, "E280.6.2.7", {"start": v(94.61, 50.32) * mm, "end": v(99.54, 55.25) * mm});
            skLineSegment(sketch, "E280.6.2.8", {"start": v(97.3, 47.62) * mm, "end": v(102.23, 52.55) * mm});
            skLineSegment(sketch, "E280.6.2.9", {"start": v(102.23, 52.55) * mm, "end": v(107.16, 47.62) * mm});
            skLineSegment(sketch, "E280.6.2.10", {"start": v(97.3, 47.62) * mm, "end": v(107.16, 47.62) * mm});
            skLineSegment(sketch, "E280.6.2.11", {"start": v(97.3, 66.67) * mm, "end": v(102.23, 61.75) * mm});
            skLineSegment(sketch, "E280.6.2.12", {"start": v(97.3, 66.67) * mm, "end": v(107.16, 66.67) * mm});
            skLineSegment(sketch, "E280.6.2.13", {"start": v(102.23, 61.75) * mm, "end": v(107.16, 66.67) * mm});
            skLineSegment(sketch, "E280.7.0.0", {"start": v(109.85, 18.26) * mm, "end": v(114.78, 13.33) * mm});
            skLineSegment(sketch, "E280.7.0.1", {"start": v(114.78, 13.34) * mm, "end": v(109.85, 13.34) * mm});
            skLineSegment(sketch, "E280.7.0.2", {"start": v(109.86, 18.26) * mm, "end": v(104.93, 13.33) * mm});
            skLineSegment(sketch, "E280.7.0.3", {"start": v(104.93, 13.34) * mm, "end": v(109.85, 13.34) * mm});
            skLineSegment(sketch, "E280.7.0.4", {"start": v(104.93, 9.52) * mm, "end": v(109.85, 9.52) * mm});
            skLineSegment(sketch, "E280.7.0.5", {"start": v(109.85, 4.6) * mm, "end": v(104.93, 9.53) * mm});
            skLineSegment(sketch, "E280.7.0.6", {"start": v(114.78, 9.52) * mm, "end": v(109.85, 9.52) * mm});
            skLineSegment(sketch, "E280.7.0.7", {"start": v(109.86, 4.6) * mm, "end": v(114.78, 9.53) * mm});
            skLineSegment(sketch, "E280.7.0.8", {"start": v(112.55, 1.9) * mm, "end": v(117.48, 6.83) * mm});
            skLineSegment(sketch, "E280.7.0.9", {"start": v(117.47, 6.83) * mm, "end": v(122.4, 1.9) * mm});
            skLineSegment(sketch, "E280.7.0.10", {"start": v(112.55, 1.9) * mm, "end": v(122.4, 1.9) * mm});
            skLineSegment(sketch, "E280.7.0.11", {"start": v(112.55, 20.95) * mm, "end": v(117.47, 16.03) * mm});
            skLineSegment(sketch, "E280.7.0.12", {"start": v(112.55, 20.95) * mm, "end": v(122.4, 20.96) * mm});
            skLineSegment(sketch, "E280.7.0.13", {"start": v(117.47, 16.03) * mm, "end": v(122.4, 20.96) * mm});
            skLineSegment(sketch, "E280.7.1.0", {"start": v(109.85, 41.12) * mm, "end": v(114.78, 36.2) * mm});
            skLineSegment(sketch, "E280.7.1.1", {"start": v(114.78, 36.2) * mm, "end": v(109.85, 36.2) * mm});
            skLineSegment(sketch, "E280.7.1.2", {"start": v(109.85, 41.12) * mm, "end": v(104.93, 36.2) * mm});
            skLineSegment(sketch, "E280.7.1.3", {"start": v(104.93, 36.2) * mm, "end": v(109.85, 36.2) * mm});
            skLineSegment(sketch, "E280.7.1.4", {"start": v(104.93, 32.38) * mm, "end": v(109.85, 32.38) * mm});
            skLineSegment(sketch, "E280.7.1.5", {"start": v(109.85, 27.46) * mm, "end": v(104.93, 32.39) * mm});
            skLineSegment(sketch, "E280.7.1.6", {"start": v(114.78, 32.38) * mm, "end": v(109.85, 32.38) * mm});
            skLineSegment(sketch, "E280.7.1.7", {"start": v(109.85, 27.46) * mm, "end": v(114.78, 32.39) * mm});
            skLineSegment(sketch, "E280.7.1.8", {"start": v(112.55, 24.77) * mm, "end": v(117.47, 29.7) * mm});
            skLineSegment(sketch, "E280.7.1.9", {"start": v(117.47, 29.7) * mm, "end": v(122.4, 24.76) * mm});
            skLineSegment(sketch, "E280.7.1.10", {"start": v(112.55, 24.76) * mm, "end": v(122.4, 24.76) * mm});
            skLineSegment(sketch, "E280.7.1.11", {"start": v(112.55, 43.81) * mm, "end": v(117.47, 38.89) * mm});
            skLineSegment(sketch, "E280.7.1.12", {"start": v(112.55, 43.81) * mm, "end": v(122.4, 43.81) * mm});
            skLineSegment(sketch, "E280.7.1.13", {"start": v(117.47, 38.89) * mm, "end": v(122.4, 43.81) * mm});
            skLineSegment(sketch, "E280.7.2.0", {"start": v(109.85, 63.98) * mm, "end": v(114.78, 59.05) * mm});
            skLineSegment(sketch, "E280.7.2.1", {"start": v(114.78, 59.05) * mm, "end": v(109.85, 59.05) * mm});
            skLineSegment(sketch, "E280.7.2.2", {"start": v(109.85, 63.98) * mm, "end": v(104.93, 59.05) * mm});
            skLineSegment(sketch, "E280.7.2.3", {"start": v(104.93, 59.05) * mm, "end": v(109.85, 59.05) * mm});
            skLineSegment(sketch, "E280.7.2.4", {"start": v(104.93, 55.24) * mm, "end": v(109.85, 55.24) * mm});
            skLineSegment(sketch, "E280.7.2.5", {"start": v(109.85, 50.32) * mm, "end": v(104.93, 55.24) * mm});
            skLineSegment(sketch, "E280.7.2.6", {"start": v(114.78, 55.24) * mm, "end": v(109.85, 55.24) * mm});
            skLineSegment(sketch, "E280.7.2.7", {"start": v(109.85, 50.32) * mm, "end": v(114.78, 55.24) * mm});
            skLineSegment(sketch, "E280.7.2.8", {"start": v(112.55, 47.62) * mm, "end": v(117.47, 52.55) * mm});
            skLineSegment(sketch, "E280.7.2.9", {"start": v(117.47, 52.55) * mm, "end": v(122.4, 47.62) * mm});
            skLineSegment(sketch, "E280.7.2.10", {"start": v(112.55, 47.62) * mm, "end": v(122.4, 47.62) * mm});
            skLineSegment(sketch, "E280.7.2.11", {"start": v(112.55, 66.67) * mm, "end": v(117.47, 61.75) * mm});
            skLineSegment(sketch, "E280.7.2.12", {"start": v(112.55, 66.67) * mm, "end": v(122.4, 66.67) * mm});
            skLineSegment(sketch, "E280.7.2.13", {"start": v(117.47, 61.75) * mm, "end": v(122.4, 66.67) * mm});
            skLineSegment(sketch, "E280.8.0.0", {"start": v(125.1, 18.26) * mm, "end": v(130.02, 13.33) * mm});
            skLineSegment(sketch, "E280.8.0.1", {"start": v(130.02, 13.34) * mm, "end": v(125.1, 13.34) * mm});
            skLineSegment(sketch, "E280.8.0.2", {"start": v(125.1, 18.26) * mm, "end": v(120.17, 13.33) * mm});
            skLineSegment(sketch, "E280.8.0.3", {"start": v(120.17, 13.34) * mm, "end": v(125.1, 13.34) * mm});
            skLineSegment(sketch, "E280.8.0.4", {"start": v(120.17, 9.52) * mm, "end": v(125.1, 9.52) * mm});
            skLineSegment(sketch, "E280.8.0.5", {"start": v(125.1, 4.6) * mm, "end": v(120.17, 9.53) * mm});
            skLineSegment(sketch, "E280.8.0.6", {"start": v(130.02, 9.52) * mm, "end": v(125.1, 9.52) * mm});
            skLineSegment(sketch, "E280.8.0.7", {"start": v(125.1, 4.6) * mm, "end": v(130.02, 9.53) * mm});
            skLineSegment(sketch, "E280.8.0.8", {"start": v(127.79, 1.9) * mm, "end": v(132.72, 6.83) * mm});
            skLineSegment(sketch, "E280.8.0.9", {"start": v(132.72, 6.83) * mm, "end": v(137.64, 1.9) * mm});
            skLineSegment(sketch, "E280.8.0.10", {"start": v(127.79, 1.9) * mm, "end": v(137.64, 1.9) * mm});
            skLineSegment(sketch, "E280.8.0.11", {"start": v(127.79, 20.95) * mm, "end": v(132.71, 16.03) * mm});
            skLineSegment(sketch, "E280.8.0.12", {"start": v(127.79, 20.95) * mm, "end": v(137.64, 20.96) * mm});
            skLineSegment(sketch, "E280.8.0.13", {"start": v(132.71, 16.03) * mm, "end": v(137.64, 20.96) * mm});
            skLineSegment(sketch, "E280.8.1.0", {"start": v(125.1, 41.12) * mm, "end": v(130.02, 36.2) * mm});
            skLineSegment(sketch, "E280.8.1.1", {"start": v(130.02, 36.2) * mm, "end": v(125.1, 36.2) * mm});
            skLineSegment(sketch, "E280.8.1.2", {"start": v(125.1, 41.12) * mm, "end": v(120.17, 36.2) * mm});
            skLineSegment(sketch, "E280.8.1.3", {"start": v(120.17, 36.2) * mm, "end": v(125.1, 36.2) * mm});
            skLineSegment(sketch, "E280.8.1.4", {"start": v(120.17, 32.38) * mm, "end": v(125.1, 32.38) * mm});
            skLineSegment(sketch, "E280.8.1.5", {"start": v(125.1, 27.46) * mm, "end": v(120.17, 32.39) * mm});
            skLineSegment(sketch, "E280.8.1.6", {"start": v(130.02, 32.38) * mm, "end": v(125.1, 32.38) * mm});
            skLineSegment(sketch, "E280.8.1.7", {"start": v(125.1, 27.46) * mm, "end": v(130.02, 32.39) * mm});
            skLineSegment(sketch, "E280.8.1.8", {"start": v(127.79, 24.77) * mm, "end": v(132.71, 29.7) * mm});
            skLineSegment(sketch, "E280.8.1.9", {"start": v(132.71, 29.7) * mm, "end": v(137.64, 24.76) * mm});
            skLineSegment(sketch, "E280.8.1.10", {"start": v(127.79, 24.76) * mm, "end": v(137.64, 24.76) * mm});
            skLineSegment(sketch, "E280.8.1.11", {"start": v(127.79, 43.81) * mm, "end": v(132.71, 38.89) * mm});
            skLineSegment(sketch, "E280.8.1.12", {"start": v(127.79, 43.81) * mm, "end": v(137.64, 43.81) * mm});
            skLineSegment(sketch, "E280.8.1.13", {"start": v(132.71, 38.89) * mm, "end": v(137.64, 43.82) * mm});
            skLineSegment(sketch, "E280.8.2.0", {"start": v(125.1, 63.98) * mm, "end": v(130.02, 59.05) * mm});
            skLineSegment(sketch, "E280.8.2.1", {"start": v(130.02, 59.05) * mm, "end": v(125.1, 59.05) * mm});
            skLineSegment(sketch, "E280.8.2.2", {"start": v(125.1, 63.98) * mm, "end": v(120.17, 59.05) * mm});
            skLineSegment(sketch, "E280.8.2.3", {"start": v(120.17, 59.05) * mm, "end": v(125.1, 59.05) * mm});
            skLineSegment(sketch, "E280.8.2.4", {"start": v(120.17, 55.24) * mm, "end": v(125.1, 55.24) * mm});
            skLineSegment(sketch, "E280.8.2.5", {"start": v(125.1, 50.32) * mm, "end": v(120.17, 55.25) * mm});
            skLineSegment(sketch, "E280.8.2.6", {"start": v(130.02, 55.24) * mm, "end": v(125.1, 55.24) * mm});
            skLineSegment(sketch, "E280.8.2.7", {"start": v(125.1, 50.32) * mm, "end": v(130.02, 55.24) * mm});
            skLineSegment(sketch, "E280.8.2.8", {"start": v(127.79, 47.62) * mm, "end": v(132.71, 52.55) * mm});
            skLineSegment(sketch, "E280.8.2.9", {"start": v(132.71, 52.55) * mm, "end": v(137.64, 47.62) * mm});
            skLineSegment(sketch, "E280.8.2.10", {"start": v(127.79, 47.62) * mm, "end": v(137.64, 47.62) * mm});
            skLineSegment(sketch, "E280.8.2.11", {"start": v(127.79, 66.67) * mm, "end": v(132.71, 61.75) * mm});
            skLineSegment(sketch, "E280.8.2.12", {"start": v(127.79, 66.67) * mm, "end": v(137.64, 66.67) * mm});
            skLineSegment(sketch, "E280.8.2.13", {"start": v(132.71, 61.75) * mm, "end": v(137.64, 66.67) * mm});
            skLineSegment(sketch, "E280.9.0.0", {"start": v(140.33, 18.26) * mm, "end": v(145.26, 13.33) * mm});
            skLineSegment(sketch, "E280.9.0.1", {"start": v(145.26, 13.34) * mm, "end": v(140.34, 13.34) * mm});
            skLineSegment(sketch, "E280.9.0.2", {"start": v(140.34, 18.26) * mm, "end": v(135.4, 13.33) * mm});
            skLineSegment(sketch, "E280.9.0.3", {"start": v(135.4, 13.34) * mm, "end": v(140.34, 13.34) * mm});
            skLineSegment(sketch, "E280.9.0.4", {"start": v(135.4, 9.52) * mm, "end": v(140.34, 9.52) * mm});
            skLineSegment(sketch, "E280.9.0.5", {"start": v(140.33, 4.6) * mm, "end": v(135.4, 9.53) * mm});
            skLineSegment(sketch, "E280.9.0.6", {"start": v(145.26, 9.52) * mm, "end": v(140.34, 9.52) * mm});
            skLineSegment(sketch, "E280.9.0.7", {"start": v(140.34, 4.6) * mm, "end": v(145.26, 9.53) * mm});
            skLineSegment(sketch, "E280.9.0.8", {"start": v(143.03, 1.9) * mm, "end": v(147.96, 6.83) * mm});
            skLineSegment(sketch, "E280.9.0.9", {"start": v(147.96, 6.83) * mm, "end": v(152.88, 1.9) * mm});
            skLineSegment(sketch, "E280.9.0.10", {"start": v(143.03, 1.9) * mm, "end": v(152.88, 1.9) * mm});
            skLineSegment(sketch, "E280.9.0.11", {"start": v(143.03, 20.95) * mm, "end": v(147.95, 16.03) * mm});
            skLineSegment(sketch, "E280.9.0.12", {"start": v(143.03, 20.95) * mm, "end": v(152.88, 20.96) * mm});
            skLineSegment(sketch, "E280.9.0.13", {"start": v(147.95, 16.03) * mm, "end": v(152.88, 20.96) * mm});
            skLineSegment(sketch, "E280.9.1.0", {"start": v(140.33, 41.12) * mm, "end": v(145.26, 36.2) * mm});
            skLineSegment(sketch, "E280.9.1.1", {"start": v(145.26, 36.2) * mm, "end": v(140.33, 36.2) * mm});
            skLineSegment(sketch, "E280.9.1.2", {"start": v(140.33, 41.12) * mm, "end": v(135.4, 36.2) * mm});
            skLineSegment(sketch, "E280.9.1.3", {"start": v(135.4, 36.2) * mm, "end": v(140.33, 36.2) * mm});
            skLineSegment(sketch, "E280.9.1.4", {"start": v(135.4, 32.38) * mm, "end": v(140.33, 32.38) * mm});
            skLineSegment(sketch, "E280.9.1.5", {"start": v(140.33, 27.46) * mm, "end": v(135.4, 32.39) * mm});
            skLineSegment(sketch, "E280.9.1.6", {"start": v(145.26, 32.38) * mm, "end": v(140.33, 32.38) * mm});
            skLineSegment(sketch, "E280.9.1.7", {"start": v(140.33, 27.46) * mm, "end": v(145.26, 32.38) * mm});
            skLineSegment(sketch, "E280.9.1.8", {"start": v(143.03, 24.77) * mm, "end": v(147.95, 29.7) * mm});
            skLineSegment(sketch, "E280.9.1.9", {"start": v(147.95, 29.7) * mm, "end": v(152.88, 24.76) * mm});
            skLineSegment(sketch, "E280.9.1.10", {"start": v(143.03, 24.76) * mm, "end": v(152.88, 24.76) * mm});
            skLineSegment(sketch, "E280.9.1.11", {"start": v(143.03, 43.81) * mm, "end": v(147.95, 38.89) * mm});
            skLineSegment(sketch, "E280.9.1.12", {"start": v(143.03, 43.81) * mm, "end": v(152.88, 43.81) * mm});
            skLineSegment(sketch, "E280.9.1.13", {"start": v(147.95, 38.89) * mm, "end": v(152.88, 43.81) * mm});
            skLineSegment(sketch, "E280.9.2.0", {"start": v(140.33, 63.98) * mm, "end": v(145.26, 59.05) * mm});
            skLineSegment(sketch, "E280.9.2.1", {"start": v(145.26, 59.05) * mm, "end": v(140.33, 59.05) * mm});
            skLineSegment(sketch, "E280.9.2.2", {"start": v(140.33, 63.98) * mm, "end": v(135.4, 59.05) * mm});
            skLineSegment(sketch, "E280.9.2.3", {"start": v(135.4, 59.05) * mm, "end": v(140.33, 59.05) * mm});
            skLineSegment(sketch, "E280.9.2.4", {"start": v(135.4, 55.24) * mm, "end": v(140.33, 55.24) * mm});
            skLineSegment(sketch, "E280.9.2.5", {"start": v(140.33, 50.32) * mm, "end": v(135.4, 55.25) * mm});
            skLineSegment(sketch, "E280.9.2.6", {"start": v(145.26, 55.24) * mm, "end": v(140.33, 55.24) * mm});
            skLineSegment(sketch, "E280.9.2.7", {"start": v(140.33, 50.32) * mm, "end": v(145.26, 55.24) * mm});
            skLineSegment(sketch, "E280.9.2.8", {"start": v(143.03, 47.62) * mm, "end": v(147.95, 52.55) * mm});
            skLineSegment(sketch, "E280.9.2.9", {"start": v(147.95, 52.55) * mm, "end": v(152.88, 47.62) * mm});
            skLineSegment(sketch, "E280.9.2.10", {"start": v(143.03, 47.62) * mm, "end": v(152.88, 47.62) * mm});
            skLineSegment(sketch, "E280.9.2.11", {"start": v(143.03, 66.67) * mm, "end": v(147.95, 61.75) * mm});
            skLineSegment(sketch, "E280.9.2.12", {"start": v(143.03, 66.67) * mm, "end": v(152.88, 66.67) * mm});
            skLineSegment(sketch, "E280.9.2.13", {"start": v(147.95, 61.75) * mm, "end": v(152.88, 66.67) * mm});
            skLineSegment(sketch, "E280.10.0.0", {"start": v(155.57, 18.26) * mm, "end": v(160.5, 13.33) * mm});
            skLineSegment(sketch, "E280.10.0.1", {"start": v(160.5, 13.34) * mm, "end": v(155.58, 13.34) * mm});
            skLineSegment(sketch, "E280.10.0.2", {"start": v(155.58, 18.26) * mm, "end": v(150.65, 13.33) * mm});
            skLineSegment(sketch, "E280.10.0.3", {"start": v(150.65, 13.34) * mm, "end": v(155.58, 13.34) * mm});
            skLineSegment(sketch, "E280.10.0.11", {"start": v(158.27, 20.95) * mm, "end": v(163.2, 16.03) * mm});
            skLineSegment(sketch, "E280.10.1.0", {"start": v(155.57, 41.12) * mm, "end": v(160.5, 36.2) * mm});
            skLineSegment(sketch, "E280.10.1.1", {"start": v(160.5, 36.2) * mm, "end": v(155.57, 36.2) * mm});
            skLineSegment(sketch, "E280.10.1.2", {"start": v(155.57, 41.12) * mm, "end": v(150.65, 36.2) * mm});
            skLineSegment(sketch, "E280.10.1.3", {"start": v(150.65, 36.2) * mm, "end": v(155.57, 36.2) * mm});
            skLineSegment(sketch, "E280.10.1.4", {"start": v(150.65, 32.38) * mm, "end": v(155.57, 32.38) * mm});
            skLineSegment(sketch, "E280.10.1.5", {"start": v(155.57, 27.46) * mm, "end": v(150.65, 32.39) * mm});
            skLineSegment(sketch, "E280.10.1.6", {"start": v(160.5, 32.38) * mm, "end": v(155.57, 32.38) * mm});
            skLineSegment(sketch, "E280.10.1.7", {"start": v(155.57, 27.46) * mm, "end": v(160.5, 32.39) * mm});
            skLineSegment(sketch, "E280.10.1.8", {"start": v(158.27, 24.77) * mm, "end": v(163.2, 29.7) * mm});
            skLineSegment(sketch, "E280.10.1.11", {"start": v(158.27, 43.81) * mm, "end": v(163.2, 38.89) * mm});
            skLineSegment(sketch, "E280.10.1.12", {"start": v(158.27, 43.81) * mm, "end": v(163.2, 43.81) * mm});
            skLineSegment(sketch, "E280.10.2.0", {"start": v(155.57, 63.98) * mm, "end": v(160.5, 59.05) * mm});
            skLineSegment(sketch, "E280.10.2.1", {"start": v(160.5, 59.05) * mm, "end": v(155.57, 59.05) * mm});
            skLineSegment(sketch, "E280.10.2.2", {"start": v(155.57, 63.98) * mm, "end": v(150.65, 59.05) * mm});
            skLineSegment(sketch, "E280.10.2.3", {"start": v(150.65, 59.05) * mm, "end": v(155.57, 59.05) * mm});
            skLineSegment(sketch, "E280.10.2.4", {"start": v(150.65, 55.24) * mm, "end": v(155.57, 55.24) * mm});
            skLineSegment(sketch, "E280.10.2.5", {"start": v(155.57, 50.32) * mm, "end": v(150.65, 55.25) * mm});
            skLineSegment(sketch, "E280.10.2.6", {"start": v(160.5, 55.24) * mm, "end": v(155.57, 55.24) * mm});
            skLineSegment(sketch, "E280.10.2.7", {"start": v(155.57, 50.32) * mm, "end": v(160.5, 55.24) * mm});
            skLineSegment(sketch, "E280.10.2.8", {"start": v(158.27, 47.63) * mm, "end": v(163.2, 52.55) * mm});
            skLineSegment(sketch, "E280.10.2.11", {"start": v(158.27, 66.67) * mm, "end": v(163.2, 61.75) * mm});
            skLineSegment(sketch, "E280.10.2.12", {"start": v(158.27, 66.67) * mm, "end": v(163.2, 66.67) * mm});
            skLineSegment(sketch, "E280.direction2", {"start": v(5.87, 1.9) * mm, "end": v(5.87, 24.77) * mm, "construction": true});
            skLineSegment(sketch, "E281", {"start": v(163.2, 52.55) * mm, "end": v(163.2, 47.62) * mm});
            skLineSegment(sketch, "E282", {"start": v(163.2, 43.81) * mm, "end": v(163.2, 38.89) * mm});
            skLineSegment(sketch, "E283", {"start": v(163.2, 61.75) * mm, "end": v(163.2, 66.67) * mm});
            skLineSegment(sketch, "E284", {"start": v(158.27, 47.62) * mm, "end": v(163.2, 47.62) * mm});
            skLineSegment(sketch, "E285", {"start": v(158.27, 24.77) * mm, "end": v(163.2, 24.77) * mm});
            skLineSegment(sketch, "E286", {"start": v(163.2, 24.77) * mm, "end": v(163.2, 29.7) * mm});
            skLineSegment(sketch, "E287", {"start": v(158.27, 20.95) * mm, "end": v(163.2, 20.95) * mm});
            skLineSegment(sketch, "E288", {"start": v(163.2, 20.95) * mm, "end": v(163.2, 16.03) * mm});
            skLineSegment(sketch, "E289.0.1.0", {"start": v(-4.44, 38.89) * mm, "end": v(-4.44, 43.81) * mm});
            skLineSegment(sketch, "E289.0.1.1", {"start": v(-4.44, 43.81) * mm, "end": v(0.48, 43.81) * mm});
            skLineSegment(sketch, "E289.0.1.2", {"start": v(0.48, 43.81) * mm, "end": v(-4.44, 38.89) * mm});
            skLineSegment(sketch, "E289.0.1.3", {"start": v(-4.44, 29.7) * mm, "end": v(-4.44, 24.77) * mm});
            skLineSegment(sketch, "E289.0.1.4", {"start": v(-4.45, 29.7) * mm, "end": v(0.48, 24.77) * mm});
            skLineSegment(sketch, "E289.0.1.5", {"start": v(0.48, 24.77) * mm, "end": v(-4.44, 24.77) * mm});
            skLineSegment(sketch, "E289.0.2.0", {"start": v(-4.44, 61.75) * mm, "end": v(-4.44, 66.67) * mm});
            skLineSegment(sketch, "E289.0.2.1", {"start": v(-4.44, 66.67) * mm, "end": v(0.48, 66.67) * mm});
            skLineSegment(sketch, "E289.0.2.2", {"start": v(0.48, 66.67) * mm, "end": v(-4.44, 61.75) * mm});
            skLineSegment(sketch, "E289.0.2.3", {"start": v(-4.44, 52.55) * mm, "end": v(-4.44, 47.63) * mm});
            skLineSegment(sketch, "E289.0.2.4", {"start": v(-4.45, 52.55) * mm, "end": v(0.48, 47.62) * mm});
            skLineSegment(sketch, "E289.0.2.5", {"start": v(0.48, 47.62) * mm, "end": v(-4.44, 47.62) * mm});
            skSolve(sketch);
        }
        {
            var Q0;
            Q0 = qSketchRegion(id + "F28", true);
            extrude(context, id + "F29", {"entities" : qUnion([Q0]), "operationType" : NewBodyOperationType.REMOVE, "oppositeDirection" : true, "depth" : 2.54 * mm, "offsetDistance" : 25.4 * mm});
        }
        {
            var Q0;
            Q0=makeQuery(id+"F6.boolean.opBoolean","MERGE",FACE,{"derivedFrom":[makeQuery(id+"F2.opExtrude","SWEPT_FACE",FACE,{"disambiguationData":[OSD([sQuery(id+"F1.wireOp",EDGE,"E9.3")])]}),makeQuery(id+"F6.opExtrude","SWEPT_FACE",FACE,{"disambiguationData":[OSD([sQuery(id+"F5.wireOp",EDGE,"E60.right")])]})]});
            var sketch = newSketch(context, id + "F30", { "sketchPlane" : qUnion([Q0])});
            skLineSegment(sketch, "E290.0.2.0", {"start": v(-152.04, 63.9) * mm, "end": v(-147.1, 58.98) * mm});
            skLineSegment(sketch, "E290.0.2.2", {"start": v(-152.04, 63.9) * mm, "end": v(-156.96, 58.98) * mm});
            skLineSegment(sketch, "E290.0.2.3", {"start": v(-156.96, 58.98) * mm, "end": v(-147.1, 58.98) * mm});
            skLineSegment(sketch, "E290.0.2.4", {"start": v(-156.96, 55.17) * mm, "end": v(-147.1, 55.17) * mm});
            skLineSegment(sketch, "E290.0.2.5", {"start": v(-152.04, 50.24) * mm, "end": v(-156.96, 55.17) * mm});
            skLineSegment(sketch, "E290.0.2.7", {"start": v(-152.04, 50.24) * mm, "end": v(-147.1, 55.17) * mm});
            skLineSegment(sketch, "E290.0.2.8", {"start": v(-149.34, 47.55) * mm, "end": v(-144.42, 52.48) * mm});
            skLineSegment(sketch, "E290.0.2.9", {"start": v(-144.42, 52.48) * mm, "end": v(-139.49, 47.55) * mm});
            skLineSegment(sketch, "E290.0.2.10", {"start": v(-149.34, 47.55) * mm, "end": v(-139.49, 47.55) * mm});
            skLineSegment(sketch, "E290.0.2.11", {"start": v(-149.34, 66.6) * mm, "end": v(-144.42, 61.67) * mm});
            skLineSegment(sketch, "E290.0.2.12", {"start": v(-149.34, 66.6) * mm, "end": v(-139.49, 66.6) * mm});
            skLineSegment(sketch, "E290.0.2.13", {"start": v(-144.42, 61.67) * mm, "end": v(-139.49, 66.6) * mm});
            skLineSegment(sketch, "E290.1.2.0", {"start": v(-136.8, 63.9) * mm, "end": v(-131.87, 58.98) * mm});
            skLineSegment(sketch, "E290.1.2.2", {"start": v(-136.8, 63.9) * mm, "end": v(-141.72, 58.98) * mm});
            skLineSegment(sketch, "E290.1.2.3", {"start": v(-141.72, 58.98) * mm, "end": v(-131.87, 58.98) * mm});
            skLineSegment(sketch, "E290.1.2.4", {"start": v(-141.72, 55.17) * mm, "end": v(-131.87, 55.17) * mm});
            skLineSegment(sketch, "E290.1.2.5", {"start": v(-136.8, 50.24) * mm, "end": v(-141.72, 55.17) * mm});
            skLineSegment(sketch, "E290.1.2.7", {"start": v(-136.8, 50.24) * mm, "end": v(-131.87, 55.17) * mm});
            skLineSegment(sketch, "E290.1.2.8", {"start": v(-134.1, 47.55) * mm, "end": v(-129.18, 52.48) * mm});
            skLineSegment(sketch, "E290.1.2.9", {"start": v(-129.18, 52.48) * mm, "end": v(-124.25, 47.55) * mm});
            skLineSegment(sketch, "E290.1.2.10", {"start": v(-134.1, 47.55) * mm, "end": v(-124.25, 47.55) * mm});
            skLineSegment(sketch, "E290.1.2.11", {"start": v(-134.1, 66.6) * mm, "end": v(-129.18, 61.67) * mm});
            skLineSegment(sketch, "E290.1.2.12", {"start": v(-134.1, 66.6) * mm, "end": v(-124.25, 66.6) * mm});
            skLineSegment(sketch, "E290.1.2.13", {"start": v(-129.18, 61.67) * mm, "end": v(-124.25, 66.6) * mm});
            skLineSegment(sketch, "E290.2.2.0", {"start": v(-121.56, 63.9) * mm, "end": v(-116.63, 58.98) * mm});
            skLineSegment(sketch, "E290.2.2.2", {"start": v(-121.56, 63.9) * mm, "end": v(-126.48, 58.98) * mm});
            skLineSegment(sketch, "E290.2.2.3", {"start": v(-126.48, 58.98) * mm, "end": v(-116.63, 58.98) * mm});
            skLineSegment(sketch, "E290.2.2.4", {"start": v(-126.48, 55.17) * mm, "end": v(-116.63, 55.17) * mm});
            skLineSegment(sketch, "E290.2.2.5", {"start": v(-121.56, 50.24) * mm, "end": v(-126.48, 55.17) * mm});
            skLineSegment(sketch, "E290.2.2.7", {"start": v(-121.56, 50.24) * mm, "end": v(-116.63, 55.17) * mm});
            skLineSegment(sketch, "E290.2.2.8", {"start": v(-118.86, 47.55) * mm, "end": v(-113.94, 52.48) * mm});
            skLineSegment(sketch, "E290.2.2.9", {"start": v(-113.94, 52.48) * mm, "end": v(-109, 47.55) * mm});
            skLineSegment(sketch, "E290.2.2.10", {"start": v(-118.86, 47.55) * mm, "end": v(-109, 47.55) * mm});
            skLineSegment(sketch, "E290.2.2.11", {"start": v(-118.86, 66.6) * mm, "end": v(-113.94, 61.67) * mm});
            skLineSegment(sketch, "E290.2.2.12", {"start": v(-118.86, 66.6) * mm, "end": v(-109, 66.6) * mm});
            skLineSegment(sketch, "E290.2.2.13", {"start": v(-113.94, 61.67) * mm, "end": v(-109, 66.6) * mm});
            skLineSegment(sketch, "E290.3.2.0", {"start": v(-106.32, 63.9) * mm, "end": v(-101.39, 58.98) * mm});
            skLineSegment(sketch, "E290.3.2.2", {"start": v(-106.32, 63.9) * mm, "end": v(-111.24, 58.98) * mm});
            skLineSegment(sketch, "E290.3.2.3", {"start": v(-111.24, 58.98) * mm, "end": v(-101.39, 58.98) * mm});
            skLineSegment(sketch, "E290.3.2.4", {"start": v(-111.24, 55.17) * mm, "end": v(-101.39, 55.17) * mm});
            skLineSegment(sketch, "E290.3.2.5", {"start": v(-106.32, 50.24) * mm, "end": v(-111.24, 55.17) * mm});
            skLineSegment(sketch, "E290.3.2.7", {"start": v(-106.32, 50.24) * mm, "end": v(-101.39, 55.17) * mm});
            skLineSegment(sketch, "E290.3.2.8", {"start": v(-103.62, 47.55) * mm, "end": v(-98.7, 52.48) * mm});
            skLineSegment(sketch, "E290.3.2.9", {"start": v(-98.7, 52.48) * mm, "end": v(-93.77, 47.55) * mm});
            skLineSegment(sketch, "E290.3.2.10", {"start": v(-103.62, 47.55) * mm, "end": v(-93.77, 47.55) * mm});
            skLineSegment(sketch, "E290.3.2.11", {"start": v(-103.62, 66.6) * mm, "end": v(-98.7, 61.67) * mm});
            skLineSegment(sketch, "E290.3.2.12", {"start": v(-103.62, 66.6) * mm, "end": v(-93.77, 66.6) * mm});
            skLineSegment(sketch, "E290.3.2.13", {"start": v(-98.7, 61.67) * mm, "end": v(-93.77, 66.6) * mm});
            skLineSegment(sketch, "E290.4.2.0", {"start": v(-91.08, 63.9) * mm, "end": v(-86.15, 58.98) * mm});
            skLineSegment(sketch, "E290.4.2.2", {"start": v(-91.08, 63.9) * mm, "end": v(-96, 58.98) * mm});
            skLineSegment(sketch, "E290.4.2.3", {"start": v(-96, 58.98) * mm, "end": v(-86.15, 58.98) * mm});
            skLineSegment(sketch, "E290.4.2.4", {"start": v(-96, 55.17) * mm, "end": v(-86.15, 55.17) * mm});
            skLineSegment(sketch, "E290.4.2.5", {"start": v(-91.08, 50.24) * mm, "end": v(-96, 55.17) * mm});
            skLineSegment(sketch, "E290.4.2.7", {"start": v(-91.08, 50.24) * mm, "end": v(-86.15, 55.17) * mm});
            skLineSegment(sketch, "E290.4.2.8", {"start": v(-88.38, 47.55) * mm, "end": v(-83.46, 52.48) * mm});
            skLineSegment(sketch, "E290.4.2.9", {"start": v(-83.46, 52.48) * mm, "end": v(-78.53, 47.55) * mm});
            skLineSegment(sketch, "E290.4.2.10", {"start": v(-88.38, 47.55) * mm, "end": v(-78.53, 47.55) * mm});
            skLineSegment(sketch, "E290.4.2.11", {"start": v(-88.38, 66.6) * mm, "end": v(-83.46, 61.67) * mm});
            skLineSegment(sketch, "E290.4.2.12", {"start": v(-88.38, 66.6) * mm, "end": v(-78.53, 66.6) * mm});
            skLineSegment(sketch, "E290.4.2.13", {"start": v(-83.46, 61.67) * mm, "end": v(-78.53, 66.6) * mm});
            skLineSegment(sketch, "E290.5.2.0", {"start": v(-75.84, 63.9) * mm, "end": v(-70.9, 58.98) * mm});
            skLineSegment(sketch, "E290.5.2.2", {"start": v(-75.84, 63.9) * mm, "end": v(-80.76, 58.98) * mm});
            skLineSegment(sketch, "E290.5.2.3", {"start": v(-80.76, 58.98) * mm, "end": v(-70.9, 58.98) * mm});
            skLineSegment(sketch, "E290.5.2.4", {"start": v(-80.76, 55.17) * mm, "end": v(-70.9, 55.17) * mm});
            skLineSegment(sketch, "E290.5.2.5", {"start": v(-75.84, 50.24) * mm, "end": v(-80.76, 55.17) * mm});
            skLineSegment(sketch, "E290.5.2.7", {"start": v(-75.84, 50.24) * mm, "end": v(-70.9, 55.17) * mm});
            skLineSegment(sketch, "E290.5.2.8", {"start": v(-73.14, 47.55) * mm, "end": v(-68.22, 52.48) * mm});
            skLineSegment(sketch, "E290.5.2.9", {"start": v(-68.22, 52.48) * mm, "end": v(-63.29, 47.55) * mm});
            skLineSegment(sketch, "E290.5.2.10", {"start": v(-73.14, 47.55) * mm, "end": v(-63.29, 47.55) * mm});
            skLineSegment(sketch, "E290.5.2.11", {"start": v(-73.14, 66.6) * mm, "end": v(-68.22, 61.67) * mm});
            skLineSegment(sketch, "E290.5.2.12", {"start": v(-73.14, 66.6) * mm, "end": v(-63.29, 66.6) * mm});
            skLineSegment(sketch, "E290.5.2.13", {"start": v(-68.22, 61.67) * mm, "end": v(-63.29, 66.6) * mm});
            skLineSegment(sketch, "E290.6.2.0", {"start": v(-60.6, 63.9) * mm, "end": v(-55.67, 58.98) * mm});
            skLineSegment(sketch, "E290.6.2.2", {"start": v(-60.6, 63.9) * mm, "end": v(-65.52, 58.98) * mm});
            skLineSegment(sketch, "E290.6.2.3", {"start": v(-65.52, 58.98) * mm, "end": v(-55.67, 58.98) * mm});
            skLineSegment(sketch, "E290.6.2.4", {"start": v(-65.52, 55.17) * mm, "end": v(-55.67, 55.17) * mm});
            skLineSegment(sketch, "E290.6.2.5", {"start": v(-60.6, 50.24) * mm, "end": v(-65.52, 55.17) * mm});
            skLineSegment(sketch, "E290.6.2.7", {"start": v(-60.6, 50.24) * mm, "end": v(-55.67, 55.17) * mm});
            skLineSegment(sketch, "E290.6.2.8", {"start": v(-57.9, 47.55) * mm, "end": v(-52.98, 52.48) * mm});
            skLineSegment(sketch, "E290.6.2.9", {"start": v(-52.98, 52.48) * mm, "end": v(-48.05, 47.55) * mm});
            skLineSegment(sketch, "E290.6.2.10", {"start": v(-57.9, 47.55) * mm, "end": v(-48.05, 47.55) * mm});
            skLineSegment(sketch, "E290.6.2.11", {"start": v(-57.9, 66.6) * mm, "end": v(-52.98, 61.67) * mm});
            skLineSegment(sketch, "E290.6.2.12", {"start": v(-57.9, 66.6) * mm, "end": v(-48.05, 66.6) * mm});
            skLineSegment(sketch, "E290.6.2.13", {"start": v(-52.98, 61.67) * mm, "end": v(-48.05, 66.6) * mm});
            skLineSegment(sketch, "E290.7.2.0", {"start": v(-45.36, 63.9) * mm, "end": v(-40.43, 58.98) * mm});
            skLineSegment(sketch, "E290.7.2.2", {"start": v(-45.36, 63.9) * mm, "end": v(-50.28, 58.98) * mm});
            skLineSegment(sketch, "E290.7.2.3", {"start": v(-50.28, 58.98) * mm, "end": v(-40.43, 58.98) * mm});
            skLineSegment(sketch, "E290.7.2.4", {"start": v(-50.28, 55.17) * mm, "end": v(-40.43, 55.17) * mm});
            skLineSegment(sketch, "E290.7.2.5", {"start": v(-45.36, 50.24) * mm, "end": v(-50.28, 55.17) * mm});
            skLineSegment(sketch, "E290.7.2.7", {"start": v(-45.36, 50.24) * mm, "end": v(-40.43, 55.17) * mm});
            skLineSegment(sketch, "E290.7.2.8", {"start": v(-42.66, 47.55) * mm, "end": v(-37.74, 52.48) * mm});
            skLineSegment(sketch, "E290.7.2.9", {"start": v(-37.74, 52.48) * mm, "end": v(-32.8, 47.55) * mm});
            skLineSegment(sketch, "E290.7.2.10", {"start": v(-42.66, 47.55) * mm, "end": v(-32.8, 47.55) * mm});
            skLineSegment(sketch, "E290.7.2.11", {"start": v(-42.66, 66.6) * mm, "end": v(-37.74, 61.67) * mm});
            skLineSegment(sketch, "E290.7.2.12", {"start": v(-42.66, 66.6) * mm, "end": v(-32.8, 66.6) * mm});
            skLineSegment(sketch, "E290.7.2.13", {"start": v(-37.74, 61.67) * mm, "end": v(-32.8, 66.6) * mm});
            skLineSegment(sketch, "E290.8.2.0", {"start": v(-30.12, 63.9) * mm, "end": v(-25.19, 58.98) * mm});
            skLineSegment(sketch, "E290.8.2.2", {"start": v(-30.12, 63.9) * mm, "end": v(-35.04, 58.98) * mm});
            skLineSegment(sketch, "E290.8.2.3", {"start": v(-35.04, 58.98) * mm, "end": v(-25.19, 58.98) * mm});
            skLineSegment(sketch, "E290.8.2.4", {"start": v(-35.04, 55.17) * mm, "end": v(-25.19, 55.17) * mm});
            skLineSegment(sketch, "E290.8.2.5", {"start": v(-30.12, 50.24) * mm, "end": v(-35.04, 55.17) * mm});
            skLineSegment(sketch, "E290.8.2.7", {"start": v(-30.12, 50.24) * mm, "end": v(-25.19, 55.17) * mm});
            skLineSegment(sketch, "E290.8.2.8", {"start": v(-27.42, 47.55) * mm, "end": v(-22.5, 52.48) * mm});
            skLineSegment(sketch, "E290.8.2.9", {"start": v(-22.5, 52.48) * mm, "end": v(-17.57, 47.55) * mm});
            skLineSegment(sketch, "E290.8.2.10", {"start": v(-27.42, 47.55) * mm, "end": v(-17.57, 47.55) * mm});
            skLineSegment(sketch, "E290.8.2.11", {"start": v(-27.42, 66.6) * mm, "end": v(-22.5, 61.67) * mm});
            skLineSegment(sketch, "E290.8.2.12", {"start": v(-27.42, 66.6) * mm, "end": v(-17.57, 66.6) * mm});
            skLineSegment(sketch, "E290.8.2.13", {"start": v(-22.5, 61.67) * mm, "end": v(-17.57, 66.6) * mm});
            skLineSegment(sketch, "E290.9.2.0", {"start": v(-14.88, 63.9) * mm, "end": v(-9.95, 58.98) * mm});
            skLineSegment(sketch, "E290.9.2.2", {"start": v(-14.88, 63.9) * mm, "end": v(-19.8, 58.98) * mm});
            skLineSegment(sketch, "E290.9.2.3", {"start": v(-19.8, 58.98) * mm, "end": v(-9.95, 58.98) * mm});
            skLineSegment(sketch, "E290.9.2.4", {"start": v(-19.8, 55.17) * mm, "end": v(-9.95, 55.17) * mm});
            skLineSegment(sketch, "E290.9.2.5", {"start": v(-14.88, 50.24) * mm, "end": v(-19.8, 55.17) * mm});
            skLineSegment(sketch, "E290.9.2.7", {"start": v(-14.88, 50.24) * mm, "end": v(-9.95, 55.17) * mm});
            skLineSegment(sketch, "E290.9.2.8", {"start": v(-12.18, 47.55) * mm, "end": v(-7.26, 52.48) * mm});
            skLineSegment(sketch, "E290.9.2.9", {"start": v(-7.26, 52.48) * mm, "end": v(-2.33, 47.55) * mm});
            skLineSegment(sketch, "E290.9.2.10", {"start": v(-12.18, 47.55) * mm, "end": v(-2.33, 47.55) * mm});
            skLineSegment(sketch, "E290.9.2.11", {"start": v(-12.18, 66.6) * mm, "end": v(-7.26, 61.67) * mm});
            skLineSegment(sketch, "E290.9.2.12", {"start": v(-12.18, 66.6) * mm, "end": v(-2.33, 66.6) * mm});
            skLineSegment(sketch, "E290.9.2.13", {"start": v(-7.26, 61.67) * mm, "end": v(-2.33, 66.6) * mm});
            skLineSegment(sketch, "E290.10.2.0", {"start": v(0.36, 63.9) * mm, "end": v(5.3, 58.98) * mm});
            skLineSegment(sketch, "E290.10.2.2", {"start": v(0.36, 63.9) * mm, "end": v(-4.56, 58.98) * mm});
            skLineSegment(sketch, "E290.10.2.3", {"start": v(-4.56, 58.98) * mm, "end": v(5.3, 58.98) * mm});
            skLineSegment(sketch, "E290.10.2.4", {"start": v(-4.56, 55.17) * mm, "end": v(5.3, 55.17) * mm});
            skLineSegment(sketch, "E290.10.2.5", {"start": v(0.36, 50.24) * mm, "end": v(-4.56, 55.17) * mm});
            skLineSegment(sketch, "E290.10.2.7", {"start": v(0.36, 50.24) * mm, "end": v(5.3, 55.17) * mm});
            skLineSegment(sketch, "E290.10.2.8", {"start": v(3.06, 47.55) * mm, "end": v(7.98, 52.48) * mm});
            skLineSegment(sketch, "E290.10.2.11", {"start": v(3.06, 66.6) * mm, "end": v(7.98, 61.67) * mm});
            skLineSegment(sketch, "E290.10.2.12", {"start": v(3.06, 66.6) * mm, "end": v(7.98, 66.6) * mm});
            skLineSegment(sketch, "E291", {"start": v(7.98, 52.48) * mm, "end": v(7.98, 47.55) * mm});
            skLineSegment(sketch, "E292", {"start": v(7.98, 61.67) * mm, "end": v(7.98, 66.6) * mm});
            skLineSegment(sketch, "E293", {"start": v(3.06, 47.55) * mm, "end": v(7.98, 47.55) * mm});
            skLineSegment(sketch, "E294.0.2.0", {"start": v(-159.66, 61.67) * mm, "end": v(-159.66, 66.6) * mm});
            skLineSegment(sketch, "E294.0.2.1", {"start": v(-159.66, 66.6) * mm, "end": v(-154.73, 66.6) * mm});
            skLineSegment(sketch, "E294.0.2.2", {"start": v(-154.73, 66.6) * mm, "end": v(-159.66, 61.67) * mm});
            skLineSegment(sketch, "E294.0.2.3", {"start": v(-159.66, 52.48) * mm, "end": v(-159.66, 47.55) * mm});
            skLineSegment(sketch, "E294.0.2.4", {"start": v(-159.66, 52.48) * mm, "end": v(-154.73, 47.55) * mm});
            skLineSegment(sketch, "E294.0.2.5", {"start": v(-154.73, 47.55) * mm, "end": v(-159.66, 47.55) * mm});
            skLineSegment(sketch, "E295.0.1.0", {"start": v(-126.48, 36.12) * mm, "end": v(-116.63, 36.12) * mm});
            skLineSegment(sketch, "E295.0.1.1", {"start": v(-113.94, 29.62) * mm, "end": v(-109, 24.7) * mm});
            skLineSegment(sketch, "E295.0.1.2", {"start": v(3.06, 43.74) * mm, "end": v(7.98, 38.81) * mm});
            skLineSegment(sketch, "E295.0.1.3", {"start": v(-121.56, 27.38) * mm, "end": v(-116.63, 32.31) * mm});
            skLineSegment(sketch, "E295.0.1.4", {"start": v(-73.14, 43.74) * mm, "end": v(-63.29, 43.74) * mm});
            skLineSegment(sketch, "E295.0.1.5", {"start": v(-103.62, 24.7) * mm, "end": v(-93.77, 24.7) * mm});
            skLineSegment(sketch, "E295.0.1.6", {"start": v(-30.12, 27.38) * mm, "end": v(-25.19, 32.31) * mm});
            skLineSegment(sketch, "E295.0.1.7", {"start": v(-118.86, 24.7) * mm, "end": v(-113.94, 29.62) * mm});
            skLineSegment(sketch, "E295.0.1.8", {"start": v(-42.66, 43.74) * mm, "end": v(-32.8, 43.74) * mm});
            skLineSegment(sketch, "E295.0.1.9", {"start": v(-129.18, 29.62) * mm, "end": v(-124.25, 24.7) * mm});
            skLineSegment(sketch, "E295.0.1.10", {"start": v(0.36, 27.38) * mm, "end": v(5.3, 32.31) * mm});
            skLineSegment(sketch, "E295.0.1.11", {"start": v(-57.9, 43.74) * mm, "end": v(-52.98, 38.81) * mm});
            skLineSegment(sketch, "E295.0.1.12", {"start": v(-14.88, 27.38) * mm, "end": v(-9.95, 32.31) * mm});
            skLineSegment(sketch, "E295.0.1.13", {"start": v(-88.38, 43.74) * mm, "end": v(-78.53, 43.74) * mm});
            skLineSegment(sketch, "E295.0.1.14", {"start": v(-106.32, 41.05) * mm, "end": v(-101.39, 36.12) * mm});
            skLineSegment(sketch, "E295.0.1.15", {"start": v(-60.6, 41.05) * mm, "end": v(-65.52, 36.12) * mm});
            skLineSegment(sketch, "E295.0.1.16", {"start": v(-156.96, 36.12) * mm, "end": v(-147.1, 36.12) * mm});
            skLineSegment(sketch, "E295.0.1.17", {"start": v(-156.96, 32.31) * mm, "end": v(-147.1, 32.31) * mm});
            skLineSegment(sketch, "E295.0.1.18", {"start": v(-134.1, 24.7) * mm, "end": v(-124.25, 24.7) * mm});
            skLineSegment(sketch, "E295.0.1.19", {"start": v(-144.42, 29.62) * mm, "end": v(-139.49, 24.7) * mm});
            skLineSegment(sketch, "E295.0.1.20", {"start": v(-45.36, 27.38) * mm, "end": v(-40.43, 32.31) * mm});
            skLineSegment(sketch, "E295.0.1.21", {"start": v(-134.1, 43.74) * mm, "end": v(-124.25, 43.74) * mm});
            skLineSegment(sketch, "E295.0.1.22", {"start": v(-45.36, 41.05) * mm, "end": v(-50.28, 36.12) * mm});
            skLineSegment(sketch, "E295.0.1.23", {"start": v(0.36, 27.38) * mm, "end": v(-4.56, 32.31) * mm});
            skLineSegment(sketch, "E295.0.1.24", {"start": v(-103.62, 24.7) * mm, "end": v(-98.7, 29.62) * mm});
            skLineSegment(sketch, "E295.0.1.25", {"start": v(-121.56, 41.05) * mm, "end": v(-126.48, 36.12) * mm});
            skLineSegment(sketch, "E295.0.1.26", {"start": v(-106.32, 27.38) * mm, "end": v(-101.39, 32.31) * mm});
            skLineSegment(sketch, "E295.0.1.27", {"start": v(-35.04, 36.12) * mm, "end": v(-25.19, 36.12) * mm});
            skLineSegment(sketch, "E295.0.1.28", {"start": v(-22.5, 38.81) * mm, "end": v(-17.57, 43.74) * mm});
            skLineSegment(sketch, "E295.0.1.29", {"start": v(-60.6, 27.38) * mm, "end": v(-65.52, 32.31) * mm});
            skLineSegment(sketch, "E295.0.1.30", {"start": v(-30.12, 41.05) * mm, "end": v(-25.19, 36.12) * mm});
            skLineSegment(sketch, "E295.0.1.31", {"start": v(-118.86, 24.7) * mm, "end": v(-109, 24.7) * mm});
            skLineSegment(sketch, "E295.0.1.32", {"start": v(-88.38, 43.74) * mm, "end": v(-83.46, 38.81) * mm});
            skLineSegment(sketch, "E295.0.1.33", {"start": v(-19.8, 36.12) * mm, "end": v(-9.95, 36.12) * mm});
            skLineSegment(sketch, "E295.0.1.34", {"start": v(-106.32, 41.05) * mm, "end": v(-111.24, 36.12) * mm});
            skLineSegment(sketch, "E295.0.1.35", {"start": v(-134.1, 43.74) * mm, "end": v(-129.18, 38.81) * mm});
            skLineSegment(sketch, "E295.0.1.36", {"start": v(-91.08, 27.38) * mm, "end": v(-96, 32.31) * mm});
            skLineSegment(sketch, "E295.0.1.37", {"start": v(-103.62, 43.74) * mm, "end": v(-93.77, 43.74) * mm});
            skLineSegment(sketch, "E295.0.1.38", {"start": v(-75.84, 41.05) * mm, "end": v(-80.76, 36.12) * mm});
            skLineSegment(sketch, "E295.0.1.39", {"start": v(-111.24, 32.31) * mm, "end": v(-101.39, 32.31) * mm});
            skLineSegment(sketch, "E295.0.1.40", {"start": v(-65.52, 36.12) * mm, "end": v(-55.67, 36.12) * mm});
            skLineSegment(sketch, "E295.0.1.41", {"start": v(0.36, 41.05) * mm, "end": v(5.3, 36.12) * mm});
            skLineSegment(sketch, "E295.0.1.42", {"start": v(-19.8, 32.31) * mm, "end": v(-9.95, 32.31) * mm});
            skLineSegment(sketch, "E295.0.1.43", {"start": v(-45.36, 27.38) * mm, "end": v(-50.28, 32.31) * mm});
            skLineSegment(sketch, "E295.0.1.44", {"start": v(-27.42, 24.7) * mm, "end": v(-17.57, 24.7) * mm});
            skLineSegment(sketch, "E295.0.1.45", {"start": v(-57.9, 43.74) * mm, "end": v(-48.05, 43.74) * mm});
            skLineSegment(sketch, "E295.0.1.46", {"start": v(-52.98, 29.62) * mm, "end": v(-48.05, 24.7) * mm});
            skLineSegment(sketch, "E295.0.1.47", {"start": v(-80.76, 32.31) * mm, "end": v(-70.9, 32.31) * mm});
            skLineSegment(sketch, "E295.0.1.48", {"start": v(-14.88, 27.38) * mm, "end": v(-19.8, 32.31) * mm});
            skLineSegment(sketch, "E295.0.1.49", {"start": v(-12.18, 24.7) * mm, "end": v(-2.33, 24.7) * mm});
            skLineSegment(sketch, "E295.0.1.50", {"start": v(0.36, 41.05) * mm, "end": v(-4.56, 36.12) * mm});
            skLineSegment(sketch, "E295.0.1.51", {"start": v(-149.34, 43.74) * mm, "end": v(-144.42, 38.81) * mm});
            skLineSegment(sketch, "E295.0.1.52", {"start": v(-12.18, 43.74) * mm, "end": v(-7.26, 38.81) * mm});
            skLineSegment(sketch, "E295.0.1.53", {"start": v(-30.12, 27.38) * mm, "end": v(-35.04, 32.31) * mm});
            skLineSegment(sketch, "E295.0.1.54", {"start": v(-96, 36.12) * mm, "end": v(-86.15, 36.12) * mm});
            skLineSegment(sketch, "E295.0.1.55", {"start": v(-75.84, 27.38) * mm, "end": v(-70.9, 32.31) * mm});
            skLineSegment(sketch, "E295.0.1.56", {"start": v(-50.28, 32.31) * mm, "end": v(-40.43, 32.31) * mm});
            skLineSegment(sketch, "E295.0.1.57", {"start": v(-7.26, 29.62) * mm, "end": v(-2.33, 24.7) * mm});
            skLineSegment(sketch, "E295.0.1.58", {"start": v(-106.32, 27.38) * mm, "end": v(-111.24, 32.31) * mm});
            skLineSegment(sketch, "E295.0.1.59", {"start": v(-57.9, 24.7) * mm, "end": v(-48.05, 24.7) * mm});
            skLineSegment(sketch, "E295.0.1.60", {"start": v(-52.98, 38.81) * mm, "end": v(-48.05, 43.74) * mm});
            skLineSegment(sketch, "E295.0.1.61", {"start": v(-42.66, 24.7) * mm, "end": v(-32.8, 24.7) * mm});
            skLineSegment(sketch, "E295.0.1.62", {"start": v(-35.04, 32.31) * mm, "end": v(-25.19, 32.31) * mm});
            skLineSegment(sketch, "E295.0.1.63", {"start": v(-12.18, 43.74) * mm, "end": v(-2.33, 43.74) * mm});
            skLineSegment(sketch, "E295.0.1.64", {"start": v(-121.56, 41.05) * mm, "end": v(-116.63, 36.12) * mm});
            skLineSegment(sketch, "E295.0.1.65", {"start": v(-27.42, 24.7) * mm, "end": v(-22.5, 29.62) * mm});
            skLineSegment(sketch, "E295.0.1.66", {"start": v(-73.14, 24.7) * mm, "end": v(-68.22, 29.62) * mm});
            skLineSegment(sketch, "E295.0.1.67", {"start": v(-4.56, 36.12) * mm, "end": v(5.3, 36.12) * mm});
            skLineSegment(sketch, "E295.0.1.68", {"start": v(-83.46, 29.62) * mm, "end": v(-78.53, 24.7) * mm});
            skLineSegment(sketch, "E295.0.1.69", {"start": v(-73.14, 24.7) * mm, "end": v(-63.29, 24.7) * mm});
            skLineSegment(sketch, "E295.0.1.70", {"start": v(-42.66, 24.7) * mm, "end": v(-37.74, 29.62) * mm});
            skLineSegment(sketch, "E295.0.1.71", {"start": v(-27.42, 43.74) * mm, "end": v(-22.5, 38.81) * mm});
            skLineSegment(sketch, "E295.0.1.72", {"start": v(-30.12, 41.05) * mm, "end": v(-35.04, 36.12) * mm});
            skLineSegment(sketch, "E295.0.1.73", {"start": v(-45.36, 41.05) * mm, "end": v(-40.43, 36.12) * mm});
            skLineSegment(sketch, "E295.0.1.74", {"start": v(-91.08, 41.05) * mm, "end": v(-86.15, 36.12) * mm});
            skLineSegment(sketch, "E295.0.1.75", {"start": v(-149.34, 24.7) * mm, "end": v(-139.49, 24.7) * mm});
            skLineSegment(sketch, "E295.0.1.76", {"start": v(-14.88, 41.05) * mm, "end": v(-19.8, 36.12) * mm});
            skLineSegment(sketch, "E295.0.1.77", {"start": v(-98.7, 38.81) * mm, "end": v(-93.77, 43.74) * mm});
            skLineSegment(sketch, "E295.0.1.78", {"start": v(-88.38, 24.7) * mm, "end": v(-78.53, 24.7) * mm});
            skLineSegment(sketch, "E295.0.1.79", {"start": v(3.06, 24.7) * mm, "end": v(7.98, 29.62) * mm});
            skLineSegment(sketch, "E295.0.1.80", {"start": v(-73.14, 43.74) * mm, "end": v(-68.22, 38.81) * mm});
            skLineSegment(sketch, "E295.0.1.81", {"start": v(-152.04, 27.38) * mm, "end": v(-156.96, 32.31) * mm});
            skLineSegment(sketch, "E295.0.1.82", {"start": v(-149.34, 24.7) * mm, "end": v(-144.42, 29.62) * mm});
            skLineSegment(sketch, "E295.0.1.83", {"start": v(-42.66, 43.74) * mm, "end": v(-37.74, 38.81) * mm});
            skLineSegment(sketch, "E295.0.1.84", {"start": v(-118.86, 43.74) * mm, "end": v(-113.94, 38.81) * mm});
            skLineSegment(sketch, "E295.0.1.85", {"start": v(-4.56, 32.31) * mm, "end": v(5.3, 32.31) * mm});
            skLineSegment(sketch, "E295.0.1.86", {"start": v(-50.28, 36.12) * mm, "end": v(-40.43, 36.12) * mm});
            skLineSegment(sketch, "E295.0.1.87", {"start": v(-80.76, 36.12) * mm, "end": v(-70.9, 36.12) * mm});
            skLineSegment(sketch, "E295.0.1.88", {"start": v(-136.8, 41.05) * mm, "end": v(-131.87, 36.12) * mm});
            skLineSegment(sketch, "E295.0.1.89", {"start": v(-98.7, 29.62) * mm, "end": v(-93.77, 24.7) * mm});
            skLineSegment(sketch, "E295.0.1.90", {"start": v(-149.34, 43.74) * mm, "end": v(-139.49, 43.74) * mm});
            skLineSegment(sketch, "E295.0.1.91", {"start": v(-22.5, 29.62) * mm, "end": v(-17.57, 24.7) * mm});
            skLineSegment(sketch, "E295.0.1.92", {"start": v(-88.38, 24.7) * mm, "end": v(-83.46, 29.62) * mm});
            skLineSegment(sketch, "E295.0.1.93", {"start": v(-60.6, 27.38) * mm, "end": v(-55.67, 32.31) * mm});
            skLineSegment(sketch, "E295.0.1.94", {"start": v(-7.26, 38.81) * mm, "end": v(-2.33, 43.74) * mm});
            skLineSegment(sketch, "E295.0.1.95", {"start": v(-134.1, 24.7) * mm, "end": v(-129.18, 29.62) * mm});
            skLineSegment(sketch, "E295.0.1.96", {"start": v(-154.73, 43.74) * mm, "end": v(-159.66, 38.81) * mm});
            skLineSegment(sketch, "E295.0.1.97", {"start": v(-118.86, 43.74) * mm, "end": v(-109, 43.74) * mm});
            skLineSegment(sketch, "E295.0.1.98", {"start": v(-126.48, 32.31) * mm, "end": v(-116.63, 32.31) * mm});
            skLineSegment(sketch, "E295.0.1.99", {"start": v(-37.74, 29.62) * mm, "end": v(-32.8, 24.7) * mm});
            skLineSegment(sketch, "E295.0.1.100", {"start": v(-136.8, 41.05) * mm, "end": v(-141.72, 36.12) * mm});
            skLineSegment(sketch, "E295.0.1.101", {"start": v(-141.72, 36.12) * mm, "end": v(-131.87, 36.12) * mm});
            skLineSegment(sketch, "E295.0.1.102", {"start": v(-152.04, 27.38) * mm, "end": v(-147.1, 32.31) * mm});
            skLineSegment(sketch, "E295.0.1.103", {"start": v(-75.84, 41.05) * mm, "end": v(-70.9, 36.12) * mm});
            skLineSegment(sketch, "E295.0.1.104", {"start": v(-91.08, 27.38) * mm, "end": v(-86.15, 32.31) * mm});
            skLineSegment(sketch, "E295.0.1.105", {"start": v(-91.08, 41.05) * mm, "end": v(-96, 36.12) * mm});
            skLineSegment(sketch, "E295.0.1.106", {"start": v(-144.42, 38.81) * mm, "end": v(-139.49, 43.74) * mm});
            skLineSegment(sketch, "E295.0.1.107", {"start": v(-57.9, 24.7) * mm, "end": v(-52.98, 29.62) * mm});
            skLineSegment(sketch, "E295.0.1.108", {"start": v(-83.46, 38.81) * mm, "end": v(-78.53, 43.74) * mm});
            skLineSegment(sketch, "E295.0.1.109", {"start": v(-121.56, 27.38) * mm, "end": v(-126.48, 32.31) * mm});
            skLineSegment(sketch, "E295.0.1.110", {"start": v(-27.42, 43.74) * mm, "end": v(-17.57, 43.74) * mm});
            skLineSegment(sketch, "E295.0.1.111", {"start": v(-12.18, 24.7) * mm, "end": v(-7.26, 29.62) * mm});
            skLineSegment(sketch, "E295.0.1.112", {"start": v(-14.88, 41.05) * mm, "end": v(-9.95, 36.12) * mm});
            skLineSegment(sketch, "E295.0.1.113", {"start": v(-141.72, 32.31) * mm, "end": v(-131.87, 32.31) * mm});
            skLineSegment(sketch, "E295.0.1.114", {"start": v(-129.18, 38.81) * mm, "end": v(-124.25, 43.74) * mm});
            skLineSegment(sketch, "E295.0.1.115", {"start": v(-68.22, 29.62) * mm, "end": v(-63.29, 24.7) * mm});
            skLineSegment(sketch, "E295.0.1.116", {"start": v(-75.84, 27.38) * mm, "end": v(-80.76, 32.31) * mm});
            skLineSegment(sketch, "E295.0.1.117", {"start": v(-96, 32.31) * mm, "end": v(-86.15, 32.31) * mm});
            skLineSegment(sketch, "E295.0.1.118", {"start": v(-60.6, 41.05) * mm, "end": v(-55.67, 36.12) * mm});
            skLineSegment(sketch, "E295.0.1.119", {"start": v(-37.74, 38.81) * mm, "end": v(-32.8, 43.74) * mm});
            skLineSegment(sketch, "E295.0.1.120", {"start": v(-136.8, 27.38) * mm, "end": v(-141.72, 32.31) * mm});
            skLineSegment(sketch, "E295.0.1.121", {"start": v(-136.8, 27.38) * mm, "end": v(-131.87, 32.31) * mm});
            skLineSegment(sketch, "E295.0.1.122", {"start": v(-111.24, 36.12) * mm, "end": v(-101.39, 36.12) * mm});
            skLineSegment(sketch, "E295.0.1.123", {"start": v(-65.52, 32.31) * mm, "end": v(-55.67, 32.31) * mm});
            skLineSegment(sketch, "E295.0.1.124", {"start": v(-152.04, 41.05) * mm, "end": v(-147.1, 36.12) * mm});
            skLineSegment(sketch, "E295.0.1.125", {"start": v(-152.04, 41.05) * mm, "end": v(-156.96, 36.12) * mm});
            skLineSegment(sketch, "E295.0.1.126", {"start": v(-68.22, 38.81) * mm, "end": v(-63.29, 43.74) * mm});
            skLineSegment(sketch, "E295.0.1.127", {"start": v(-103.62, 43.74) * mm, "end": v(-98.7, 38.81) * mm});
            skLineSegment(sketch, "E295.0.1.128", {"start": v(-113.94, 38.81) * mm, "end": v(-109, 43.74) * mm});
            skLineSegment(sketch, "E295.0.1.129", {"start": v(-159.66, 29.62) * mm, "end": v(-154.73, 24.7) * mm});
            skLineSegment(sketch, "E295.0.1.130", {"start": v(-154.73, 24.7) * mm, "end": v(-159.66, 24.7) * mm});
            skLineSegment(sketch, "E295.0.1.131", {"start": v(7.98, 38.81) * mm, "end": v(7.98, 43.74) * mm});
            skLineSegment(sketch, "E295.0.1.132", {"start": v(7.98, 29.62) * mm, "end": v(7.98, 24.7) * mm});
            skLineSegment(sketch, "E295.0.1.133", {"start": v(3.06, 24.7) * mm, "end": v(7.98, 24.7) * mm});
            skLineSegment(sketch, "E295.0.1.134", {"start": v(-159.66, 29.62) * mm, "end": v(-159.66, 24.7) * mm});
            skLineSegment(sketch, "E295.0.1.135", {"start": v(3.06, 43.74) * mm, "end": v(7.98, 43.74) * mm});
            skLineSegment(sketch, "E295.0.1.136", {"start": v(-159.66, 43.74) * mm, "end": v(-154.73, 43.74) * mm});
            skLineSegment(sketch, "E295.0.1.137", {"start": v(-159.66, 38.81) * mm, "end": v(-159.66, 43.74) * mm});
            skLineSegment(sketch, "E295.0.2.1", {"start": v(-113.94, 6.76) * mm, "end": v(-109, 1.83) * mm});
            skLineSegment(sketch, "E295.0.2.2", {"start": v(3.06, 20.88) * mm, "end": v(7.98, 15.95) * mm});
            skLineSegment(sketch, "E295.0.2.5", {"start": v(-103.62, 1.83) * mm, "end": v(-93.77, 1.83) * mm});
            skLineSegment(sketch, "E295.0.2.7", {"start": v(-118.86, 1.83) * mm, "end": v(-113.94, 6.76) * mm});
            skLineSegment(sketch, "E295.0.2.9", {"start": v(-129.18, 6.76) * mm, "end": v(-124.25, 1.83) * mm});
            skLineSegment(sketch, "E295.0.2.10", {"start": v(0.36, 4.52) * mm, "end": v(5.3, 9.45) * mm});
            skLineSegment(sketch, "E295.0.2.12", {"start": v(-14.88, 4.52) * mm, "end": v(-9.95, 9.45) * mm});
            skLineSegment(sketch, "E295.0.2.18", {"start": v(-134.1, 1.83) * mm, "end": v(-124.25, 1.83) * mm});
            skLineSegment(sketch, "E295.0.2.19", {"start": v(-144.42, 6.76) * mm, "end": v(-139.49, 1.83) * mm});
            skLineSegment(sketch, "E295.0.2.23", {"start": v(0.36, 4.52) * mm, "end": v(-4.56, 9.45) * mm});
            skLineSegment(sketch, "E295.0.2.24", {"start": v(-103.62, 1.83) * mm, "end": v(-98.7, 6.76) * mm});
            skLineSegment(sketch, "E295.0.2.31", {"start": v(-118.86, 1.83) * mm, "end": v(-109, 1.83) * mm});
            skLineSegment(sketch, "E295.0.2.33", {"start": v(-14.88, 13.26) * mm, "end": v(-9.95, 13.26) * mm});
            skLineSegment(sketch, "E295.0.2.41", {"start": v(0.36, 18.19) * mm, "end": v(5.3, 13.26) * mm});
            skLineSegment(sketch, "E295.0.2.42", {"start": v(-14.88, 9.45) * mm, "end": v(-9.95, 9.45) * mm});
            skLineSegment(sketch, "E295.0.2.46", {"start": v(-52.98, 6.76) * mm, "end": v(-48.05, 1.83) * mm});
            skLineSegment(sketch, "E295.0.2.49", {"start": v(-12.18, 1.83) * mm, "end": v(-2.33, 1.83) * mm});
            skLineSegment(sketch, "E295.0.2.50", {"start": v(0.36, 18.19) * mm, "end": v(-4.56, 13.26) * mm});
            skLineSegment(sketch, "E295.0.2.52", {"start": v(-12.18, 20.88) * mm, "end": v(-7.26, 15.95) * mm});
            skLineSegment(sketch, "E295.0.2.57", {"start": v(-7.26, 6.76) * mm, "end": v(-2.33, 1.83) * mm});
            skLineSegment(sketch, "E295.0.2.59", {"start": v(-57.9, 1.83) * mm, "end": v(-48.05, 1.83) * mm});
            skLineSegment(sketch, "E295.0.2.61", {"start": v(-42.66, 1.83) * mm, "end": v(-32.8, 1.83) * mm});
            skLineSegment(sketch, "E295.0.2.63", {"start": v(-12.18, 20.88) * mm, "end": v(-2.33, 20.88) * mm});
            skLineSegment(sketch, "E295.0.2.66", {"start": v(-73.14, 1.83) * mm, "end": v(-68.22, 6.76) * mm});
            skLineSegment(sketch, "E295.0.2.67", {"start": v(-4.56, 13.26) * mm, "end": v(5.3, 13.26) * mm});
            skLineSegment(sketch, "E295.0.2.68", {"start": v(-83.46, 6.76) * mm, "end": v(-78.53, 1.83) * mm});
            skLineSegment(sketch, "E295.0.2.69", {"start": v(-73.14, 1.83) * mm, "end": v(-63.29, 1.83) * mm});
            skLineSegment(sketch, "E295.0.2.70", {"start": v(-42.66, 1.83) * mm, "end": v(-37.74, 6.76) * mm});
            skLineSegment(sketch, "E295.0.2.75", {"start": v(-149.34, 1.83) * mm, "end": v(-139.49, 1.83) * mm});
            skLineSegment(sketch, "E295.0.2.78", {"start": v(-88.38, 1.83) * mm, "end": v(-78.53, 1.83) * mm});
            skLineSegment(sketch, "E295.0.2.79", {"start": v(3.06, 1.83) * mm, "end": v(7.98, 6.76) * mm});
            skLineSegment(sketch, "E295.0.2.82", {"start": v(-149.34, 1.83) * mm, "end": v(-144.42, 6.76) * mm});
            skLineSegment(sketch, "E295.0.2.85", {"start": v(-4.56, 9.45) * mm, "end": v(5.3, 9.45) * mm});
            skLineSegment(sketch, "E295.0.2.89", {"start": v(-98.7, 6.76) * mm, "end": v(-93.77, 1.83) * mm});
            skLineSegment(sketch, "E295.0.2.92", {"start": v(-88.38, 1.83) * mm, "end": v(-83.46, 6.76) * mm});
            skLineSegment(sketch, "E295.0.2.94", {"start": v(-7.26, 15.95) * mm, "end": v(-2.33, 20.88) * mm});
            skLineSegment(sketch, "E295.0.2.95", {"start": v(-134.1, 1.83) * mm, "end": v(-129.18, 6.76) * mm});
            skLineSegment(sketch, "E295.0.2.99", {"start": v(-37.74, 6.76) * mm, "end": v(-32.8, 1.83) * mm});
            skLineSegment(sketch, "E295.0.2.107", {"start": v(-57.9, 1.83) * mm, "end": v(-52.98, 6.76) * mm});
            skLineSegment(sketch, "E295.0.2.111", {"start": v(-12.18, 1.83) * mm, "end": v(-7.26, 6.76) * mm});
            skLineSegment(sketch, "E295.0.2.112", {"start": v(-14.88, 18.19) * mm, "end": v(-9.95, 13.26) * mm});
            skLineSegment(sketch, "E295.0.2.115", {"start": v(-68.22, 6.76) * mm, "end": v(-63.29, 1.83) * mm});
            skLineSegment(sketch, "E295.0.2.131", {"start": v(7.98, 15.95) * mm, "end": v(7.98, 20.88) * mm});
            skLineSegment(sketch, "E295.0.2.132", {"start": v(7.98, 6.76) * mm, "end": v(7.98, 1.83) * mm});
            skLineSegment(sketch, "E295.0.2.133", {"start": v(3.06, 1.83) * mm, "end": v(7.98, 1.83) * mm});
            skLineSegment(sketch, "E295.0.2.135", {"start": v(3.06, 20.88) * mm, "end": v(7.98, 20.88) * mm});
            skLineSegment(sketch, "E295.direction1", {"start": v(-159.66, 47.55) * mm, "end": v(-134.26, 47.55) * mm, "construction": true});
            skLineSegment(sketch, "E295.direction2", {"start": v(-159.66, 47.55) * mm, "end": v(-159.66, 24.7) * mm, "construction": true});
            skLineSegment(sketch, "E296", {"start": v(-14.88, 18.19) * mm, "end": v(-14.88, 13.26) * mm});
            skLineSegment(sketch, "E297", {"start": v(-14.88, 9.45) * mm, "end": v(-14.88, 4.52) * mm});
            skSolve(sketch);
        }
        {
            var Q0;
            Q0 = qSketchRegion(id + "F30", true);
            extrude(context, id + "F31", {"entities" : qUnion([Q0]), "operationType" : NewBodyOperationType.REMOVE, "oppositeDirection" : true, "depth" : 2.54 * mm, "offsetDistance" : 25.4 * mm});
        }
        {
            var Q0;
            Q0=makeQuery(id+"F6.boolean.opBoolean","MERGE",FACE,{"derivedFrom":[makeQuery(id+"F2.opExtrude","SWEPT_FACE",FACE,{"disambiguationData":[OSD([sQuery(id+"F1.wireOp",EDGE,"E9.1")])]}),makeQuery(id+"F6.opExtrude","SWEPT_FACE",FACE,{"disambiguationData":[OSD([sQuery(id+"F5.wireOp",EDGE,"E60.left")])]})]});
            var sketch = newSketch(context, id + "F32", { "sketchPlane" : qUnion([Q0])});
            skLineSegment(sketch, "E298.0.2.0", {"start": v(-1.8, 64.62) * mm, "end": v(3.13, 59.69) * mm});
            skLineSegment(sketch, "E298.0.2.2", {"start": v(-1.8, 64.62) * mm, "end": v(-6.73, 59.69) * mm});
            skLineSegment(sketch, "E298.0.2.3", {"start": v(-6.73, 59.69) * mm, "end": v(3.13, 59.69) * mm});
            skLineSegment(sketch, "E298.0.2.4", {"start": v(-6.73, 55.88) * mm, "end": v(3.13, 55.88) * mm});
            skLineSegment(sketch, "E298.0.2.5", {"start": v(-1.8, 50.95) * mm, "end": v(-6.73, 55.88) * mm});
            skLineSegment(sketch, "E298.0.2.7", {"start": v(-1.8, 50.95) * mm, "end": v(3.13, 55.88) * mm});
            skLineSegment(sketch, "E298.0.2.8", {"start": v(0.9, 48.26) * mm, "end": v(5.82, 53.19) * mm});
            skLineSegment(sketch, "E298.0.2.9", {"start": v(5.82, 53.19) * mm, "end": v(10.75, 48.26) * mm});
            skLineSegment(sketch, "E298.0.2.10", {"start": v(0.9, 48.26) * mm, "end": v(10.75, 48.26) * mm});
            skLineSegment(sketch, "E298.0.2.11", {"start": v(0.9, 67.3) * mm, "end": v(5.82, 62.38) * mm});
            skLineSegment(sketch, "E298.0.2.12", {"start": v(0.9, 67.3) * mm, "end": v(10.75, 67.3) * mm});
            skLineSegment(sketch, "E298.0.2.13", {"start": v(5.82, 62.38) * mm, "end": v(10.75, 67.3) * mm});
            skLineSegment(sketch, "E298.1.2.0", {"start": v(13.44, 64.62) * mm, "end": v(18.37, 59.69) * mm});
            skLineSegment(sketch, "E298.1.2.2", {"start": v(13.44, 64.62) * mm, "end": v(8.51, 59.69) * mm});
            skLineSegment(sketch, "E298.1.2.3", {"start": v(8.51, 59.69) * mm, "end": v(18.37, 59.69) * mm});
            skLineSegment(sketch, "E298.1.2.4", {"start": v(8.51, 55.88) * mm, "end": v(18.37, 55.88) * mm});
            skLineSegment(sketch, "E298.1.2.5", {"start": v(13.44, 50.95) * mm, "end": v(8.51, 55.88) * mm});
            skLineSegment(sketch, "E298.1.2.7", {"start": v(13.44, 50.95) * mm, "end": v(18.37, 55.88) * mm});
            skLineSegment(sketch, "E298.1.2.8", {"start": v(16.13, 48.26) * mm, "end": v(21.06, 53.19) * mm});
            skLineSegment(sketch, "E298.1.2.9", {"start": v(21.06, 53.19) * mm, "end": v(25.99, 48.26) * mm});
            skLineSegment(sketch, "E298.1.2.10", {"start": v(16.13, 48.26) * mm, "end": v(25.99, 48.26) * mm});
            skLineSegment(sketch, "E298.1.2.11", {"start": v(16.13, 67.3) * mm, "end": v(21.06, 62.38) * mm});
            skLineSegment(sketch, "E298.1.2.12", {"start": v(16.13, 67.3) * mm, "end": v(25.99, 67.3) * mm});
            skLineSegment(sketch, "E298.1.2.13", {"start": v(21.06, 62.38) * mm, "end": v(25.99, 67.3) * mm});
            skLineSegment(sketch, "E298.2.2.0", {"start": v(28.68, 64.62) * mm, "end": v(33.6, 59.69) * mm});
            skLineSegment(sketch, "E298.2.2.2", {"start": v(28.68, 64.62) * mm, "end": v(23.75, 59.69) * mm});
            skLineSegment(sketch, "E298.2.2.3", {"start": v(23.75, 59.69) * mm, "end": v(33.6, 59.69) * mm});
            skLineSegment(sketch, "E298.2.2.4", {"start": v(23.75, 55.88) * mm, "end": v(33.6, 55.88) * mm});
            skLineSegment(sketch, "E298.2.2.5", {"start": v(28.68, 50.95) * mm, "end": v(23.75, 55.88) * mm});
            skLineSegment(sketch, "E298.2.2.7", {"start": v(28.68, 50.95) * mm, "end": v(33.6, 55.88) * mm});
            skLineSegment(sketch, "E298.2.2.8", {"start": v(31.37, 48.26) * mm, "end": v(36.3, 53.19) * mm});
            skLineSegment(sketch, "E298.2.2.9", {"start": v(36.3, 53.19) * mm, "end": v(41.23, 48.26) * mm});
            skLineSegment(sketch, "E298.2.2.10", {"start": v(31.37, 48.26) * mm, "end": v(41.23, 48.26) * mm});
            skLineSegment(sketch, "E298.2.2.11", {"start": v(31.37, 67.3) * mm, "end": v(36.3, 62.38) * mm});
            skLineSegment(sketch, "E298.2.2.12", {"start": v(31.37, 67.3) * mm, "end": v(41.23, 67.3) * mm});
            skLineSegment(sketch, "E298.2.2.13", {"start": v(36.3, 62.38) * mm, "end": v(41.23, 67.3) * mm});
            skLineSegment(sketch, "E298.3.2.0", {"start": v(43.92, 64.62) * mm, "end": v(48.85, 59.69) * mm});
            skLineSegment(sketch, "E298.3.2.2", {"start": v(43.92, 64.62) * mm, "end": v(39, 59.69) * mm});
            skLineSegment(sketch, "E298.3.2.3", {"start": v(39, 59.69) * mm, "end": v(48.85, 59.69) * mm});
            skLineSegment(sketch, "E298.3.2.4", {"start": v(39, 55.88) * mm, "end": v(48.85, 55.88) * mm});
            skLineSegment(sketch, "E298.3.2.5", {"start": v(43.92, 50.95) * mm, "end": v(39, 55.88) * mm});
            skLineSegment(sketch, "E298.3.2.7", {"start": v(43.92, 50.95) * mm, "end": v(48.85, 55.88) * mm});
            skLineSegment(sketch, "E298.3.2.8", {"start": v(46.61, 48.26) * mm, "end": v(51.54, 53.19) * mm});
            skLineSegment(sketch, "E298.3.2.9", {"start": v(51.54, 53.19) * mm, "end": v(56.47, 48.26) * mm});
            skLineSegment(sketch, "E298.3.2.10", {"start": v(46.61, 48.26) * mm, "end": v(56.47, 48.26) * mm});
            skLineSegment(sketch, "E298.3.2.11", {"start": v(46.61, 67.3) * mm, "end": v(51.54, 62.38) * mm});
            skLineSegment(sketch, "E298.3.2.12", {"start": v(46.61, 67.3) * mm, "end": v(56.47, 67.3) * mm});
            skLineSegment(sketch, "E298.3.2.13", {"start": v(51.54, 62.38) * mm, "end": v(56.47, 67.3) * mm});
            skLineSegment(sketch, "E298.4.2.0", {"start": v(59.16, 64.62) * mm, "end": v(64.09, 59.69) * mm});
            skLineSegment(sketch, "E298.4.2.2", {"start": v(59.16, 64.62) * mm, "end": v(54.23, 59.69) * mm});
            skLineSegment(sketch, "E298.4.2.3", {"start": v(54.23, 59.69) * mm, "end": v(64.09, 59.69) * mm});
            skLineSegment(sketch, "E298.4.2.4", {"start": v(54.23, 55.88) * mm, "end": v(64.09, 55.88) * mm});
            skLineSegment(sketch, "E298.4.2.5", {"start": v(59.16, 50.95) * mm, "end": v(54.23, 55.88) * mm});
            skLineSegment(sketch, "E298.4.2.7", {"start": v(59.16, 50.95) * mm, "end": v(64.09, 55.88) * mm});
            skLineSegment(sketch, "E298.4.2.8", {"start": v(61.85, 48.26) * mm, "end": v(66.78, 53.19) * mm});
            skLineSegment(sketch, "E298.4.2.9", {"start": v(66.78, 53.19) * mm, "end": v(71.7, 48.26) * mm});
            skLineSegment(sketch, "E298.4.2.10", {"start": v(61.85, 48.26) * mm, "end": v(71.7, 48.26) * mm});
            skLineSegment(sketch, "E298.4.2.11", {"start": v(61.85, 67.3) * mm, "end": v(66.78, 62.38) * mm});
            skLineSegment(sketch, "E298.4.2.12", {"start": v(61.85, 67.3) * mm, "end": v(71.7, 67.3) * mm});
            skLineSegment(sketch, "E298.4.2.13", {"start": v(66.78, 62.38) * mm, "end": v(71.7, 67.3) * mm});
            skLineSegment(sketch, "E298.5.2.0", {"start": v(74.4, 64.62) * mm, "end": v(79.33, 59.69) * mm});
            skLineSegment(sketch, "E298.5.2.2", {"start": v(74.4, 64.62) * mm, "end": v(69.47, 59.69) * mm});
            skLineSegment(sketch, "E298.5.2.3", {"start": v(69.47, 59.69) * mm, "end": v(79.33, 59.69) * mm});
            skLineSegment(sketch, "E298.5.2.4", {"start": v(69.47, 55.88) * mm, "end": v(79.33, 55.88) * mm});
            skLineSegment(sketch, "E298.5.2.5", {"start": v(74.4, 50.95) * mm, "end": v(69.47, 55.88) * mm});
            skLineSegment(sketch, "E298.5.2.7", {"start": v(74.4, 50.95) * mm, "end": v(79.33, 55.88) * mm});
            skLineSegment(sketch, "E298.5.2.8", {"start": v(77.1, 48.26) * mm, "end": v(82.02, 53.19) * mm});
            skLineSegment(sketch, "E298.5.2.9", {"start": v(82.02, 53.19) * mm, "end": v(86.95, 48.26) * mm});
            skLineSegment(sketch, "E298.5.2.10", {"start": v(77.1, 48.26) * mm, "end": v(86.95, 48.26) * mm});
            skLineSegment(sketch, "E298.5.2.11", {"start": v(77.1, 67.3) * mm, "end": v(82.02, 62.38) * mm});
            skLineSegment(sketch, "E298.5.2.12", {"start": v(77.1, 67.3) * mm, "end": v(86.95, 67.3) * mm});
            skLineSegment(sketch, "E298.5.2.13", {"start": v(82.02, 62.38) * mm, "end": v(86.95, 67.3) * mm});
            skLineSegment(sketch, "E298.6.2.0", {"start": v(89.64, 64.62) * mm, "end": v(94.57, 59.69) * mm});
            skLineSegment(sketch, "E298.6.2.2", {"start": v(89.64, 64.62) * mm, "end": v(84.71, 59.69) * mm});
            skLineSegment(sketch, "E298.6.2.3", {"start": v(84.71, 59.69) * mm, "end": v(94.57, 59.69) * mm});
            skLineSegment(sketch, "E298.6.2.4", {"start": v(84.71, 55.88) * mm, "end": v(94.57, 55.88) * mm});
            skLineSegment(sketch, "E298.6.2.5", {"start": v(89.64, 50.95) * mm, "end": v(84.71, 55.88) * mm});
            skLineSegment(sketch, "E298.6.2.7", {"start": v(89.64, 50.95) * mm, "end": v(94.57, 55.88) * mm});
            skLineSegment(sketch, "E298.6.2.8", {"start": v(92.33, 48.26) * mm, "end": v(97.26, 53.19) * mm});
            skLineSegment(sketch, "E298.6.2.9", {"start": v(97.26, 53.19) * mm, "end": v(102.19, 48.26) * mm});
            skLineSegment(sketch, "E298.6.2.10", {"start": v(92.33, 48.26) * mm, "end": v(102.19, 48.26) * mm});
            skLineSegment(sketch, "E298.6.2.11", {"start": v(92.33, 67.3) * mm, "end": v(97.26, 62.38) * mm});
            skLineSegment(sketch, "E298.6.2.12", {"start": v(92.33, 67.3) * mm, "end": v(102.19, 67.3) * mm});
            skLineSegment(sketch, "E298.6.2.13", {"start": v(97.26, 62.38) * mm, "end": v(102.19, 67.3) * mm});
            skLineSegment(sketch, "E298.7.2.0", {"start": v(104.88, 64.62) * mm, "end": v(109.8, 59.69) * mm});
            skLineSegment(sketch, "E298.7.2.2", {"start": v(104.88, 64.62) * mm, "end": v(99.95, 59.69) * mm});
            skLineSegment(sketch, "E298.7.2.3", {"start": v(99.95, 59.69) * mm, "end": v(109.8, 59.69) * mm});
            skLineSegment(sketch, "E298.7.2.4", {"start": v(99.95, 55.88) * mm, "end": v(109.8, 55.88) * mm});
            skLineSegment(sketch, "E298.7.2.5", {"start": v(104.88, 50.95) * mm, "end": v(99.95, 55.88) * mm});
            skLineSegment(sketch, "E298.7.2.7", {"start": v(104.88, 50.95) * mm, "end": v(109.8, 55.88) * mm});
            skLineSegment(sketch, "E298.7.2.8", {"start": v(107.57, 48.26) * mm, "end": v(112.5, 53.19) * mm});
            skLineSegment(sketch, "E298.7.2.9", {"start": v(112.5, 53.19) * mm, "end": v(117.43, 48.26) * mm});
            skLineSegment(sketch, "E298.7.2.10", {"start": v(107.57, 48.26) * mm, "end": v(117.43, 48.26) * mm});
            skLineSegment(sketch, "E298.7.2.11", {"start": v(107.57, 67.3) * mm, "end": v(112.5, 62.38) * mm});
            skLineSegment(sketch, "E298.7.2.12", {"start": v(107.57, 67.3) * mm, "end": v(117.43, 67.3) * mm});
            skLineSegment(sketch, "E298.7.2.13", {"start": v(112.5, 62.38) * mm, "end": v(117.43, 67.3) * mm});
            skLineSegment(sketch, "E298.8.2.0", {"start": v(120.12, 64.62) * mm, "end": v(125.05, 59.69) * mm});
            skLineSegment(sketch, "E298.8.2.2", {"start": v(120.12, 64.62) * mm, "end": v(115.2, 59.69) * mm});
            skLineSegment(sketch, "E298.8.2.3", {"start": v(115.2, 59.69) * mm, "end": v(125.05, 59.69) * mm});
            skLineSegment(sketch, "E298.8.2.4", {"start": v(115.2, 55.88) * mm, "end": v(125.05, 55.88) * mm});
            skLineSegment(sketch, "E298.8.2.5", {"start": v(120.12, 50.95) * mm, "end": v(115.2, 55.88) * mm});
            skLineSegment(sketch, "E298.8.2.7", {"start": v(120.12, 50.95) * mm, "end": v(125.05, 55.88) * mm});
            skLineSegment(sketch, "E298.8.2.8", {"start": v(122.81, 48.26) * mm, "end": v(127.74, 53.19) * mm});
            skLineSegment(sketch, "E298.8.2.9", {"start": v(127.74, 53.19) * mm, "end": v(132.67, 48.26) * mm});
            skLineSegment(sketch, "E298.8.2.10", {"start": v(122.81, 48.26) * mm, "end": v(132.67, 48.26) * mm});
            skLineSegment(sketch, "E298.8.2.11", {"start": v(122.81, 67.3) * mm, "end": v(127.74, 62.38) * mm});
            skLineSegment(sketch, "E298.8.2.12", {"start": v(122.81, 67.3) * mm, "end": v(132.67, 67.3) * mm});
            skLineSegment(sketch, "E298.8.2.13", {"start": v(127.74, 62.38) * mm, "end": v(132.67, 67.3) * mm});
            skLineSegment(sketch, "E298.9.2.0", {"start": v(135.36, 64.62) * mm, "end": v(140.29, 59.69) * mm});
            skLineSegment(sketch, "E298.9.2.2", {"start": v(135.36, 64.62) * mm, "end": v(130.43, 59.69) * mm});
            skLineSegment(sketch, "E298.9.2.3", {"start": v(130.43, 59.69) * mm, "end": v(140.29, 59.69) * mm});
            skLineSegment(sketch, "E298.9.2.4", {"start": v(130.43, 55.88) * mm, "end": v(140.29, 55.88) * mm});
            skLineSegment(sketch, "E298.9.2.5", {"start": v(135.36, 50.95) * mm, "end": v(130.43, 55.88) * mm});
            skLineSegment(sketch, "E298.9.2.7", {"start": v(135.36, 50.95) * mm, "end": v(140.29, 55.88) * mm});
            skLineSegment(sketch, "E298.9.2.8", {"start": v(138.05, 48.26) * mm, "end": v(142.98, 53.19) * mm});
            skLineSegment(sketch, "E298.9.2.9", {"start": v(142.98, 53.19) * mm, "end": v(147.9, 48.26) * mm});
            skLineSegment(sketch, "E298.9.2.10", {"start": v(138.05, 48.26) * mm, "end": v(147.9, 48.26) * mm});
            skLineSegment(sketch, "E298.9.2.11", {"start": v(138.05, 67.3) * mm, "end": v(142.98, 62.38) * mm});
            skLineSegment(sketch, "E298.9.2.12", {"start": v(138.05, 67.3) * mm, "end": v(147.9, 67.3) * mm});
            skLineSegment(sketch, "E298.9.2.13", {"start": v(142.98, 62.38) * mm, "end": v(147.9, 67.3) * mm});
            skLineSegment(sketch, "E298.10.2.0", {"start": v(150.6, 64.62) * mm, "end": v(155.53, 59.69) * mm});
            skLineSegment(sketch, "E298.10.2.2", {"start": v(150.6, 64.62) * mm, "end": v(145.67, 59.69) * mm});
            skLineSegment(sketch, "E298.10.2.3", {"start": v(145.67, 59.69) * mm, "end": v(155.53, 59.69) * mm});
            skLineSegment(sketch, "E298.10.2.4", {"start": v(145.67, 55.88) * mm, "end": v(155.53, 55.88) * mm});
            skLineSegment(sketch, "E298.10.2.5", {"start": v(150.6, 50.95) * mm, "end": v(145.67, 55.88) * mm});
            skLineSegment(sketch, "E298.10.2.7", {"start": v(150.6, 50.95) * mm, "end": v(155.53, 55.88) * mm});
            skLineSegment(sketch, "E298.10.2.8", {"start": v(153.3, 48.26) * mm, "end": v(158.22, 53.19) * mm});
            skLineSegment(sketch, "E298.10.2.11", {"start": v(153.3, 67.3) * mm, "end": v(158.22, 62.38) * mm});
            skLineSegment(sketch, "E298.10.2.12", {"start": v(153.3, 67.3) * mm, "end": v(158.22, 67.3) * mm});
            skLineSegment(sketch, "E299", {"start": v(158.22, 53.19) * mm, "end": v(158.22, 48.26) * mm});
            skLineSegment(sketch, "E300", {"start": v(158.22, 62.38) * mm, "end": v(158.22, 67.3) * mm});
            skLineSegment(sketch, "E301", {"start": v(153.3, 48.26) * mm, "end": v(158.22, 48.26) * mm});
            skLineSegment(sketch, "E302.0.2.0", {"start": v(-9.42, 62.38) * mm, "end": v(-9.42, 67.3) * mm});
            skLineSegment(sketch, "E302.0.2.1", {"start": v(-9.42, 67.3) * mm, "end": v(-4.5, 67.3) * mm});
            skLineSegment(sketch, "E302.0.2.2", {"start": v(-4.5, 67.3) * mm, "end": v(-9.42, 62.38) * mm});
            skLineSegment(sketch, "E302.0.2.3", {"start": v(-9.42, 53.19) * mm, "end": v(-9.42, 48.26) * mm});
            skLineSegment(sketch, "E302.0.2.4", {"start": v(-9.42, 53.19) * mm, "end": v(-4.5, 48.26) * mm});
            skLineSegment(sketch, "E302.0.2.5", {"start": v(-4.5, 48.26) * mm, "end": v(-9.42, 48.26) * mm});
            skLineSegment(sketch, "E303.0.1.0", {"start": v(23.75, 36.83) * mm, "end": v(33.6, 36.83) * mm});
            skLineSegment(sketch, "E303.0.1.1", {"start": v(36.3, 30.33) * mm, "end": v(41.23, 25.4) * mm});
            skLineSegment(sketch, "E303.0.1.2", {"start": v(153.3, 44.45) * mm, "end": v(158.22, 39.52) * mm});
            skLineSegment(sketch, "E303.0.1.3", {"start": v(28.68, 28.1) * mm, "end": v(33.6, 33.02) * mm});
            skLineSegment(sketch, "E303.0.1.4", {"start": v(77.1, 44.45) * mm, "end": v(86.95, 44.45) * mm});
            skLineSegment(sketch, "E303.0.1.5", {"start": v(46.61, 25.4) * mm, "end": v(56.47, 25.4) * mm});
            skLineSegment(sketch, "E303.0.1.6", {"start": v(120.12, 28.1) * mm, "end": v(125.05, 33.02) * mm});
            skLineSegment(sketch, "E303.0.1.7", {"start": v(31.37, 25.4) * mm, "end": v(36.3, 30.33) * mm});
            skLineSegment(sketch, "E303.0.1.8", {"start": v(107.57, 44.45) * mm, "end": v(117.43, 44.45) * mm});
            skLineSegment(sketch, "E303.0.1.9", {"start": v(21.06, 30.33) * mm, "end": v(25.99, 25.4) * mm});
            skLineSegment(sketch, "E303.0.1.10", {"start": v(150.6, 28.1) * mm, "end": v(155.53, 33.02) * mm});
            skLineSegment(sketch, "E303.0.1.11", {"start": v(92.33, 44.45) * mm, "end": v(97.26, 39.52) * mm});
            skLineSegment(sketch, "E303.0.1.12", {"start": v(135.36, 28.1) * mm, "end": v(140.29, 33.02) * mm});
            skLineSegment(sketch, "E303.0.1.13", {"start": v(61.85, 44.45) * mm, "end": v(71.7, 44.45) * mm});
            skLineSegment(sketch, "E303.0.1.14", {"start": v(43.92, 41.76) * mm, "end": v(48.85, 36.83) * mm});
            skLineSegment(sketch, "E303.0.1.15", {"start": v(89.64, 41.76) * mm, "end": v(84.71, 36.83) * mm});
            skLineSegment(sketch, "E303.0.1.16", {"start": v(-6.73, 36.83) * mm, "end": v(3.13, 36.83) * mm});
            skLineSegment(sketch, "E303.0.1.17", {"start": v(-6.73, 33.02) * mm, "end": v(3.13, 33.02) * mm});
            skLineSegment(sketch, "E303.0.1.18", {"start": v(16.13, 25.4) * mm, "end": v(25.99, 25.4) * mm});
            skLineSegment(sketch, "E303.0.1.19", {"start": v(5.82, 30.33) * mm, "end": v(10.75, 25.4) * mm});
            skLineSegment(sketch, "E303.0.1.20", {"start": v(104.88, 28.1) * mm, "end": v(109.8, 33.02) * mm});
            skLineSegment(sketch, "E303.0.1.21", {"start": v(16.13, 44.45) * mm, "end": v(25.99, 44.45) * mm});
            skLineSegment(sketch, "E303.0.1.22", {"start": v(104.88, 41.76) * mm, "end": v(99.95, 36.83) * mm});
            skLineSegment(sketch, "E303.0.1.23", {"start": v(150.6, 28.1) * mm, "end": v(145.67, 33.02) * mm});
            skLineSegment(sketch, "E303.0.1.24", {"start": v(46.61, 25.4) * mm, "end": v(51.54, 30.33) * mm});
            skLineSegment(sketch, "E303.0.1.25", {"start": v(28.68, 41.76) * mm, "end": v(23.75, 36.83) * mm});
            skLineSegment(sketch, "E303.0.1.26", {"start": v(43.92, 28.1) * mm, "end": v(48.85, 33.02) * mm});
            skLineSegment(sketch, "E303.0.1.27", {"start": v(115.2, 36.83) * mm, "end": v(125.05, 36.83) * mm});
            skLineSegment(sketch, "E303.0.1.28", {"start": v(127.74, 39.52) * mm, "end": v(132.67, 44.45) * mm});
            skLineSegment(sketch, "E303.0.1.29", {"start": v(89.64, 28.1) * mm, "end": v(84.71, 33.02) * mm});
            skLineSegment(sketch, "E303.0.1.30", {"start": v(120.12, 41.76) * mm, "end": v(125.05, 36.83) * mm});
            skLineSegment(sketch, "E303.0.1.31", {"start": v(31.37, 25.4) * mm, "end": v(41.23, 25.4) * mm});
            skLineSegment(sketch, "E303.0.1.32", {"start": v(61.85, 44.45) * mm, "end": v(66.78, 39.52) * mm});
            skLineSegment(sketch, "E303.0.1.33", {"start": v(130.43, 36.83) * mm, "end": v(140.29, 36.83) * mm});
            skLineSegment(sketch, "E303.0.1.34", {"start": v(43.92, 41.76) * mm, "end": v(39, 36.83) * mm});
            skLineSegment(sketch, "E303.0.1.35", {"start": v(16.13, 44.45) * mm, "end": v(21.06, 39.52) * mm});
            skLineSegment(sketch, "E303.0.1.36", {"start": v(59.16, 28.1) * mm, "end": v(54.23, 33.02) * mm});
            skLineSegment(sketch, "E303.0.1.37", {"start": v(46.61, 44.45) * mm, "end": v(56.47, 44.45) * mm});
            skLineSegment(sketch, "E303.0.1.38", {"start": v(74.4, 41.76) * mm, "end": v(69.47, 36.83) * mm});
            skLineSegment(sketch, "E303.0.1.39", {"start": v(39, 33.02) * mm, "end": v(48.85, 33.02) * mm});
            skLineSegment(sketch, "E303.0.1.40", {"start": v(84.71, 36.83) * mm, "end": v(94.57, 36.83) * mm});
            skLineSegment(sketch, "E303.0.1.41", {"start": v(150.6, 41.76) * mm, "end": v(155.53, 36.83) * mm});
            skLineSegment(sketch, "E303.0.1.42", {"start": v(130.43, 33.02) * mm, "end": v(140.29, 33.02) * mm});
            skLineSegment(sketch, "E303.0.1.43", {"start": v(104.88, 28.1) * mm, "end": v(99.95, 33.02) * mm});
            skLineSegment(sketch, "E303.0.1.44", {"start": v(122.81, 25.4) * mm, "end": v(132.67, 25.4) * mm});
            skLineSegment(sketch, "E303.0.1.45", {"start": v(92.33, 44.45) * mm, "end": v(102.19, 44.45) * mm});
            skLineSegment(sketch, "E303.0.1.46", {"start": v(97.26, 30.33) * mm, "end": v(102.19, 25.4) * mm});
            skLineSegment(sketch, "E303.0.1.47", {"start": v(69.47, 33.02) * mm, "end": v(79.33, 33.02) * mm});
            skLineSegment(sketch, "E303.0.1.48", {"start": v(135.36, 28.1) * mm, "end": v(130.43, 33.02) * mm});
            skLineSegment(sketch, "E303.0.1.49", {"start": v(138.05, 25.4) * mm, "end": v(147.9, 25.4) * mm});
            skLineSegment(sketch, "E303.0.1.50", {"start": v(150.6, 41.76) * mm, "end": v(145.67, 36.83) * mm});
            skLineSegment(sketch, "E303.0.1.51", {"start": v(0.9, 44.45) * mm, "end": v(5.82, 39.52) * mm});
            skLineSegment(sketch, "E303.0.1.52", {"start": v(138.05, 44.45) * mm, "end": v(142.98, 39.52) * mm});
            skLineSegment(sketch, "E303.0.1.53", {"start": v(120.12, 28.1) * mm, "end": v(115.2, 33.02) * mm});
            skLineSegment(sketch, "E303.0.1.54", {"start": v(54.23, 36.83) * mm, "end": v(64.09, 36.83) * mm});
            skLineSegment(sketch, "E303.0.1.55", {"start": v(74.4, 28.1) * mm, "end": v(79.33, 33.02) * mm});
            skLineSegment(sketch, "E303.0.1.56", {"start": v(99.95, 33.02) * mm, "end": v(109.8, 33.02) * mm});
            skLineSegment(sketch, "E303.0.1.57", {"start": v(142.98, 30.33) * mm, "end": v(147.9, 25.4) * mm});
            skLineSegment(sketch, "E303.0.1.58", {"start": v(43.92, 28.1) * mm, "end": v(39, 33.02) * mm});
            skLineSegment(sketch, "E303.0.1.59", {"start": v(92.33, 25.4) * mm, "end": v(102.19, 25.4) * mm});
            skLineSegment(sketch, "E303.0.1.60", {"start": v(97.26, 39.52) * mm, "end": v(102.19, 44.45) * mm});
            skLineSegment(sketch, "E303.0.1.61", {"start": v(107.57, 25.4) * mm, "end": v(117.43, 25.4) * mm});
            skLineSegment(sketch, "E303.0.1.62", {"start": v(115.2, 33.02) * mm, "end": v(125.05, 33.02) * mm});
            skLineSegment(sketch, "E303.0.1.63", {"start": v(138.05, 44.45) * mm, "end": v(147.9, 44.45) * mm});
            skLineSegment(sketch, "E303.0.1.64", {"start": v(28.68, 41.76) * mm, "end": v(33.6, 36.83) * mm});
            skLineSegment(sketch, "E303.0.1.65", {"start": v(122.81, 25.4) * mm, "end": v(127.74, 30.33) * mm});
            skLineSegment(sketch, "E303.0.1.66", {"start": v(77.1, 25.4) * mm, "end": v(82.02, 30.33) * mm});
            skLineSegment(sketch, "E303.0.1.67", {"start": v(145.67, 36.83) * mm, "end": v(155.53, 36.83) * mm});
            skLineSegment(sketch, "E303.0.1.68", {"start": v(66.78, 30.33) * mm, "end": v(71.7, 25.4) * mm});
            skLineSegment(sketch, "E303.0.1.69", {"start": v(77.1, 25.4) * mm, "end": v(86.95, 25.4) * mm});
            skLineSegment(sketch, "E303.0.1.70", {"start": v(107.57, 25.4) * mm, "end": v(112.5, 30.33) * mm});
            skLineSegment(sketch, "E303.0.1.71", {"start": v(122.81, 44.45) * mm, "end": v(127.74, 39.52) * mm});
            skLineSegment(sketch, "E303.0.1.72", {"start": v(120.12, 41.76) * mm, "end": v(115.2, 36.83) * mm});
            skLineSegment(sketch, "E303.0.1.73", {"start": v(104.88, 41.76) * mm, "end": v(109.8, 36.83) * mm});
            skLineSegment(sketch, "E303.0.1.74", {"start": v(59.16, 41.76) * mm, "end": v(64.09, 36.83) * mm});
            skLineSegment(sketch, "E303.0.1.75", {"start": v(0.9, 25.4) * mm, "end": v(10.75, 25.4) * mm});
            skLineSegment(sketch, "E303.0.1.76", {"start": v(135.36, 41.76) * mm, "end": v(130.43, 36.83) * mm});
            skLineSegment(sketch, "E303.0.1.77", {"start": v(51.54, 39.52) * mm, "end": v(56.47, 44.45) * mm});
            skLineSegment(sketch, "E303.0.1.78", {"start": v(61.85, 25.4) * mm, "end": v(71.7, 25.4) * mm});
            skLineSegment(sketch, "E303.0.1.79", {"start": v(153.3, 25.4) * mm, "end": v(158.22, 30.33) * mm});
            skLineSegment(sketch, "E303.0.1.80", {"start": v(77.1, 44.45) * mm, "end": v(82.02, 39.52) * mm});
            skLineSegment(sketch, "E303.0.1.81", {"start": v(-1.8, 28.1) * mm, "end": v(-6.73, 33.02) * mm});
            skLineSegment(sketch, "E303.0.1.82", {"start": v(0.9, 25.4) * mm, "end": v(5.82, 30.33) * mm});
            skLineSegment(sketch, "E303.0.1.83", {"start": v(107.57, 44.45) * mm, "end": v(112.5, 39.52) * mm});
            skLineSegment(sketch, "E303.0.1.84", {"start": v(31.37, 44.45) * mm, "end": v(36.3, 39.52) * mm});
            skLineSegment(sketch, "E303.0.1.85", {"start": v(145.67, 33.02) * mm, "end": v(155.53, 33.02) * mm});
            skLineSegment(sketch, "E303.0.1.86", {"start": v(99.95, 36.83) * mm, "end": v(109.8, 36.83) * mm});
            skLineSegment(sketch, "E303.0.1.87", {"start": v(69.47, 36.83) * mm, "end": v(79.33, 36.83) * mm});
            skLineSegment(sketch, "E303.0.1.88", {"start": v(13.44, 41.76) * mm, "end": v(18.37, 36.83) * mm});
            skLineSegment(sketch, "E303.0.1.89", {"start": v(51.54, 30.33) * mm, "end": v(56.47, 25.4) * mm});
            skLineSegment(sketch, "E303.0.1.90", {"start": v(0.9, 44.45) * mm, "end": v(10.75, 44.45) * mm});
            skLineSegment(sketch, "E303.0.1.91", {"start": v(127.74, 30.33) * mm, "end": v(132.67, 25.4) * mm});
            skLineSegment(sketch, "E303.0.1.92", {"start": v(61.85, 25.4) * mm, "end": v(66.78, 30.33) * mm});
            skLineSegment(sketch, "E303.0.1.93", {"start": v(89.64, 28.1) * mm, "end": v(94.57, 33.02) * mm});
            skLineSegment(sketch, "E303.0.1.94", {"start": v(142.98, 39.52) * mm, "end": v(147.9, 44.45) * mm});
            skLineSegment(sketch, "E303.0.1.95", {"start": v(16.13, 25.4) * mm, "end": v(21.06, 30.33) * mm});
            skLineSegment(sketch, "E303.0.1.96", {"start": v(-4.5, 44.45) * mm, "end": v(-9.42, 39.52) * mm});
            skLineSegment(sketch, "E303.0.1.97", {"start": v(31.37, 44.45) * mm, "end": v(41.23, 44.45) * mm});
            skLineSegment(sketch, "E303.0.1.98", {"start": v(23.75, 33.02) * mm, "end": v(33.6, 33.02) * mm});
            skLineSegment(sketch, "E303.0.1.99", {"start": v(112.5, 30.33) * mm, "end": v(117.43, 25.4) * mm});
            skLineSegment(sketch, "E303.0.1.100", {"start": v(13.44, 41.76) * mm, "end": v(8.51, 36.83) * mm});
            skLineSegment(sketch, "E303.0.1.101", {"start": v(8.51, 36.83) * mm, "end": v(18.37, 36.83) * mm});
            skLineSegment(sketch, "E303.0.1.102", {"start": v(-1.8, 28.1) * mm, "end": v(3.13, 33.02) * mm});
            skLineSegment(sketch, "E303.0.1.103", {"start": v(74.4, 41.76) * mm, "end": v(79.33, 36.83) * mm});
            skLineSegment(sketch, "E303.0.1.104", {"start": v(59.16, 28.1) * mm, "end": v(64.09, 33.02) * mm});
            skLineSegment(sketch, "E303.0.1.105", {"start": v(59.16, 41.76) * mm, "end": v(54.23, 36.83) * mm});
            skLineSegment(sketch, "E303.0.1.106", {"start": v(5.82, 39.52) * mm, "end": v(10.75, 44.45) * mm});
            skLineSegment(sketch, "E303.0.1.107", {"start": v(92.33, 25.4) * mm, "end": v(97.26, 30.33) * mm});
            skLineSegment(sketch, "E303.0.1.108", {"start": v(66.78, 39.52) * mm, "end": v(71.7, 44.45) * mm});
            skLineSegment(sketch, "E303.0.1.109", {"start": v(28.68, 28.1) * mm, "end": v(23.75, 33.02) * mm});
            skLineSegment(sketch, "E303.0.1.110", {"start": v(122.81, 44.45) * mm, "end": v(132.67, 44.45) * mm});
            skLineSegment(sketch, "E303.0.1.111", {"start": v(138.05, 25.4) * mm, "end": v(142.98, 30.33) * mm});
            skLineSegment(sketch, "E303.0.1.112", {"start": v(135.36, 41.76) * mm, "end": v(140.29, 36.83) * mm});
            skLineSegment(sketch, "E303.0.1.113", {"start": v(8.51, 33.02) * mm, "end": v(18.37, 33.02) * mm});
            skLineSegment(sketch, "E303.0.1.114", {"start": v(21.06, 39.52) * mm, "end": v(25.99, 44.45) * mm});
            skLineSegment(sketch, "E303.0.1.115", {"start": v(82.02, 30.33) * mm, "end": v(86.95, 25.4) * mm});
            skLineSegment(sketch, "E303.0.1.116", {"start": v(74.4, 28.1) * mm, "end": v(69.47, 33.02) * mm});
            skLineSegment(sketch, "E303.0.1.117", {"start": v(54.23, 33.02) * mm, "end": v(64.09, 33.02) * mm});
            skLineSegment(sketch, "E303.0.1.118", {"start": v(89.64, 41.76) * mm, "end": v(94.57, 36.83) * mm});
            skLineSegment(sketch, "E303.0.1.119", {"start": v(112.5, 39.52) * mm, "end": v(117.43, 44.45) * mm});
            skLineSegment(sketch, "E303.0.1.120", {"start": v(13.44, 28.1) * mm, "end": v(8.51, 33.02) * mm});
            skLineSegment(sketch, "E303.0.1.121", {"start": v(13.44, 28.1) * mm, "end": v(18.37, 33.02) * mm});
            skLineSegment(sketch, "E303.0.1.122", {"start": v(39, 36.83) * mm, "end": v(48.85, 36.83) * mm});
            skLineSegment(sketch, "E303.0.1.123", {"start": v(84.71, 33.02) * mm, "end": v(94.57, 33.02) * mm});
            skLineSegment(sketch, "E303.0.1.124", {"start": v(-1.8, 41.76) * mm, "end": v(3.13, 36.83) * mm});
            skLineSegment(sketch, "E303.0.1.125", {"start": v(-1.8, 41.76) * mm, "end": v(-6.73, 36.83) * mm});
            skLineSegment(sketch, "E303.0.1.126", {"start": v(82.02, 39.52) * mm, "end": v(86.95, 44.45) * mm});
            skLineSegment(sketch, "E303.0.1.127", {"start": v(46.61, 44.45) * mm, "end": v(51.54, 39.52) * mm});
            skLineSegment(sketch, "E303.0.1.128", {"start": v(36.3, 39.52) * mm, "end": v(41.23, 44.45) * mm});
            skLineSegment(sketch, "E303.0.1.129", {"start": v(-9.42, 30.33) * mm, "end": v(-4.5, 25.4) * mm});
            skLineSegment(sketch, "E303.0.1.130", {"start": v(-4.5, 25.4) * mm, "end": v(-9.42, 25.4) * mm});
            skLineSegment(sketch, "E303.0.1.131", {"start": v(158.22, 39.52) * mm, "end": v(158.22, 44.45) * mm});
            skLineSegment(sketch, "E303.0.1.132", {"start": v(158.22, 30.33) * mm, "end": v(158.22, 25.4) * mm});
            skLineSegment(sketch, "E303.0.1.133", {"start": v(153.3, 25.4) * mm, "end": v(158.22, 25.4) * mm});
            skLineSegment(sketch, "E303.0.1.134", {"start": v(-9.42, 30.33) * mm, "end": v(-9.42, 25.4) * mm});
            skLineSegment(sketch, "E303.0.1.135", {"start": v(153.3, 44.45) * mm, "end": v(158.22, 44.45) * mm});
            skLineSegment(sketch, "E303.0.1.136", {"start": v(-9.42, 44.45) * mm, "end": v(-4.5, 44.45) * mm});
            skLineSegment(sketch, "E303.0.1.137", {"start": v(-9.42, 39.52) * mm, "end": v(-9.42, 44.45) * mm});
            skLineSegment(sketch, "E303.0.2.0", {"start": v(23.75, 13.97) * mm, "end": v(33.6, 13.97) * mm});
            skLineSegment(sketch, "E303.0.2.1", {"start": v(36.3, 7.47) * mm, "end": v(41.23, 2.54) * mm});
            skLineSegment(sketch, "E303.0.2.2", {"start": v(153.3, 21.59) * mm, "end": v(158.22, 16.66) * mm});
            skLineSegment(sketch, "E303.0.2.3", {"start": v(28.68, 5.23) * mm, "end": v(33.6, 10.16) * mm});
            skLineSegment(sketch, "E303.0.2.4", {"start": v(77.1, 21.59) * mm, "end": v(86.95, 21.59) * mm});
            skLineSegment(sketch, "E303.0.2.5", {"start": v(46.61, 2.54) * mm, "end": v(56.47, 2.54) * mm});
            skLineSegment(sketch, "E303.0.2.6", {"start": v(120.12, 5.23) * mm, "end": v(125.05, 10.16) * mm});
            skLineSegment(sketch, "E303.0.2.7", {"start": v(31.37, 2.54) * mm, "end": v(36.3, 7.47) * mm});
            skLineSegment(sketch, "E303.0.2.8", {"start": v(107.57, 21.59) * mm, "end": v(117.43, 21.59) * mm});
            skLineSegment(sketch, "E303.0.2.9", {"start": v(21.06, 7.47) * mm, "end": v(25.99, 2.54) * mm});
            skLineSegment(sketch, "E303.0.2.11", {"start": v(92.33, 21.59) * mm, "end": v(97.26, 16.66) * mm});
            skLineSegment(sketch, "E303.0.2.12", {"start": v(135.36, 5.23) * mm, "end": v(140.29, 10.16) * mm});
            skLineSegment(sketch, "E303.0.2.13", {"start": v(61.85, 21.59) * mm, "end": v(71.7, 21.59) * mm});
            skLineSegment(sketch, "E303.0.2.14", {"start": v(43.92, 18.9) * mm, "end": v(48.85, 13.97) * mm});
            skLineSegment(sketch, "E303.0.2.15", {"start": v(89.64, 18.9) * mm, "end": v(84.71, 13.97) * mm});
            skLineSegment(sketch, "E303.0.2.16", {"start": v(-6.73, 13.97) * mm, "end": v(3.13, 13.97) * mm});
            skLineSegment(sketch, "E303.0.2.17", {"start": v(-6.73, 10.16) * mm, "end": v(-1.8, 10.16) * mm});
            skLineSegment(sketch, "E303.0.2.18", {"start": v(16.13, 2.54) * mm, "end": v(25.99, 2.54) * mm});
            skLineSegment(sketch, "E303.0.2.19", {"start": v(5.82, 7.47) * mm, "end": v(10.75, 2.54) * mm});
            skLineSegment(sketch, "E303.0.2.20", {"start": v(104.88, 5.23) * mm, "end": v(109.8, 10.16) * mm});
            skLineSegment(sketch, "E303.0.2.21", {"start": v(16.13, 21.59) * mm, "end": v(25.99, 21.59) * mm});
            skLineSegment(sketch, "E303.0.2.22", {"start": v(104.88, 18.9) * mm, "end": v(99.95, 13.97) * mm});
            skLineSegment(sketch, "E303.0.2.23", {"start": v(150.6, 5.23) * mm, "end": v(145.67, 10.16) * mm});
            skLineSegment(sketch, "E303.0.2.24", {"start": v(46.61, 2.54) * mm, "end": v(51.54, 7.47) * mm});
            skLineSegment(sketch, "E303.0.2.25", {"start": v(28.68, 18.9) * mm, "end": v(23.75, 13.97) * mm});
            skLineSegment(sketch, "E303.0.2.26", {"start": v(43.92, 5.23) * mm, "end": v(48.85, 10.16) * mm});
            skLineSegment(sketch, "E303.0.2.27", {"start": v(115.2, 13.97) * mm, "end": v(125.05, 13.97) * mm});
            skLineSegment(sketch, "E303.0.2.28", {"start": v(127.74, 16.66) * mm, "end": v(132.67, 21.59) * mm});
            skLineSegment(sketch, "E303.0.2.29", {"start": v(89.64, 5.23) * mm, "end": v(84.71, 10.16) * mm});
            skLineSegment(sketch, "E303.0.2.30", {"start": v(120.12, 18.9) * mm, "end": v(125.05, 13.97) * mm});
            skLineSegment(sketch, "E303.0.2.31", {"start": v(31.37, 2.54) * mm, "end": v(41.23, 2.54) * mm});
            skLineSegment(sketch, "E303.0.2.32", {"start": v(61.85, 21.59) * mm, "end": v(66.78, 16.66) * mm});
            skLineSegment(sketch, "E303.0.2.33", {"start": v(130.43, 13.97) * mm, "end": v(140.29, 13.97) * mm});
            skLineSegment(sketch, "E303.0.2.34", {"start": v(43.92, 18.9) * mm, "end": v(39, 13.97) * mm});
            skLineSegment(sketch, "E303.0.2.35", {"start": v(16.13, 21.59) * mm, "end": v(21.06, 16.66) * mm});
            skLineSegment(sketch, "E303.0.2.36", {"start": v(59.16, 5.23) * mm, "end": v(54.23, 10.16) * mm});
            skLineSegment(sketch, "E303.0.2.37", {"start": v(46.61, 21.59) * mm, "end": v(56.47, 21.59) * mm});
            skLineSegment(sketch, "E303.0.2.38", {"start": v(74.4, 18.9) * mm, "end": v(69.47, 13.97) * mm});
            skLineSegment(sketch, "E303.0.2.39", {"start": v(39, 10.16) * mm, "end": v(48.85, 10.16) * mm});
            skLineSegment(sketch, "E303.0.2.40", {"start": v(84.71, 13.97) * mm, "end": v(94.57, 13.97) * mm});
            skLineSegment(sketch, "E303.0.2.41", {"start": v(150.6, 18.9) * mm, "end": v(155.53, 13.97) * mm});
            skLineSegment(sketch, "E303.0.2.42", {"start": v(130.43, 10.16) * mm, "end": v(140.29, 10.16) * mm});
            skLineSegment(sketch, "E303.0.2.43", {"start": v(104.88, 5.23) * mm, "end": v(99.95, 10.16) * mm});
            skLineSegment(sketch, "E303.0.2.44", {"start": v(122.81, 2.54) * mm, "end": v(132.67, 2.54) * mm});
            skLineSegment(sketch, "E303.0.2.45", {"start": v(92.33, 21.59) * mm, "end": v(102.19, 21.59) * mm});
            skLineSegment(sketch, "E303.0.2.46", {"start": v(97.26, 7.47) * mm, "end": v(102.19, 2.54) * mm});
            skLineSegment(sketch, "E303.0.2.47", {"start": v(69.47, 10.16) * mm, "end": v(79.33, 10.16) * mm});
            skLineSegment(sketch, "E303.0.2.48", {"start": v(135.36, 5.23) * mm, "end": v(130.43, 10.16) * mm});
            skLineSegment(sketch, "E303.0.2.49", {"start": v(138.05, 2.54) * mm, "end": v(147.9, 2.54) * mm});
            skLineSegment(sketch, "E303.0.2.50", {"start": v(150.6, 18.9) * mm, "end": v(145.67, 13.97) * mm});
            skLineSegment(sketch, "E303.0.2.51", {"start": v(0.9, 21.59) * mm, "end": v(5.82, 16.66) * mm});
            skLineSegment(sketch, "E303.0.2.52", {"start": v(138.05, 21.59) * mm, "end": v(142.98, 16.66) * mm});
            skLineSegment(sketch, "E303.0.2.53", {"start": v(120.12, 5.23) * mm, "end": v(115.2, 10.16) * mm});
            skLineSegment(sketch, "E303.0.2.54", {"start": v(54.23, 13.97) * mm, "end": v(64.09, 13.97) * mm});
            skLineSegment(sketch, "E303.0.2.55", {"start": v(74.4, 5.23) * mm, "end": v(79.33, 10.16) * mm});
            skLineSegment(sketch, "E303.0.2.56", {"start": v(99.95, 10.16) * mm, "end": v(109.8, 10.16) * mm});
            skLineSegment(sketch, "E303.0.2.57", {"start": v(142.98, 7.47) * mm, "end": v(147.9, 2.54) * mm});
            skLineSegment(sketch, "E303.0.2.58", {"start": v(43.92, 5.23) * mm, "end": v(39, 10.16) * mm});
            skLineSegment(sketch, "E303.0.2.59", {"start": v(92.33, 2.54) * mm, "end": v(102.19, 2.54) * mm});
            skLineSegment(sketch, "E303.0.2.60", {"start": v(97.26, 16.66) * mm, "end": v(102.19, 21.59) * mm});
            skLineSegment(sketch, "E303.0.2.61", {"start": v(107.57, 2.54) * mm, "end": v(117.43, 2.54) * mm});
            skLineSegment(sketch, "E303.0.2.62", {"start": v(115.2, 10.16) * mm, "end": v(125.05, 10.16) * mm});
            skLineSegment(sketch, "E303.0.2.63", {"start": v(138.05, 21.59) * mm, "end": v(147.9, 21.59) * mm});
            skLineSegment(sketch, "E303.0.2.64", {"start": v(28.68, 18.9) * mm, "end": v(33.6, 13.97) * mm});
            skLineSegment(sketch, "E303.0.2.65", {"start": v(122.81, 2.54) * mm, "end": v(127.74, 7.47) * mm});
            skLineSegment(sketch, "E303.0.2.66", {"start": v(77.1, 2.54) * mm, "end": v(82.02, 7.47) * mm});
            skLineSegment(sketch, "E303.0.2.67", {"start": v(145.67, 13.97) * mm, "end": v(155.53, 13.97) * mm});
            skLineSegment(sketch, "E303.0.2.68", {"start": v(66.78, 7.47) * mm, "end": v(71.7, 2.54) * mm});
            skLineSegment(sketch, "E303.0.2.69", {"start": v(77.1, 2.54) * mm, "end": v(86.95, 2.54) * mm});
            skLineSegment(sketch, "E303.0.2.70", {"start": v(107.57, 2.54) * mm, "end": v(112.5, 7.47) * mm});
            skLineSegment(sketch, "E303.0.2.71", {"start": v(122.81, 21.59) * mm, "end": v(127.74, 16.66) * mm});
            skLineSegment(sketch, "E303.0.2.72", {"start": v(120.12, 18.9) * mm, "end": v(115.2, 13.97) * mm});
            skLineSegment(sketch, "E303.0.2.73", {"start": v(104.88, 18.9) * mm, "end": v(109.8, 13.97) * mm});
            skLineSegment(sketch, "E303.0.2.74", {"start": v(59.16, 18.9) * mm, "end": v(64.09, 13.97) * mm});
            skLineSegment(sketch, "E303.0.2.75", {"start": v(5.82, 2.54) * mm, "end": v(10.75, 2.54) * mm});
            skLineSegment(sketch, "E303.0.2.76", {"start": v(135.36, 18.9) * mm, "end": v(130.43, 13.97) * mm});
            skLineSegment(sketch, "E303.0.2.77", {"start": v(51.54, 16.66) * mm, "end": v(56.47, 21.59) * mm});
            skLineSegment(sketch, "E303.0.2.78", {"start": v(61.85, 2.54) * mm, "end": v(71.7, 2.54) * mm});
            skLineSegment(sketch, "E303.0.2.80", {"start": v(77.1, 21.59) * mm, "end": v(82.02, 16.66) * mm});
            skLineSegment(sketch, "E303.0.2.81", {"start": v(-1.8, 5.23) * mm, "end": v(-6.73, 10.16) * mm});
            skLineSegment(sketch, "E303.0.2.83", {"start": v(107.57, 21.59) * mm, "end": v(112.5, 16.66) * mm});
            skLineSegment(sketch, "E303.0.2.84", {"start": v(31.37, 21.59) * mm, "end": v(36.3, 16.66) * mm});
            skLineSegment(sketch, "E303.0.2.85", {"start": v(145.67, 10.16) * mm, "end": v(150.6, 10.16) * mm});
            skLineSegment(sketch, "E303.0.2.86", {"start": v(99.95, 13.97) * mm, "end": v(109.8, 13.97) * mm});
            skLineSegment(sketch, "E303.0.2.87", {"start": v(69.47, 13.97) * mm, "end": v(79.33, 13.97) * mm});
            skLineSegment(sketch, "E303.0.2.88", {"start": v(13.44, 18.9) * mm, "end": v(18.37, 13.97) * mm});
            skLineSegment(sketch, "E303.0.2.89", {"start": v(51.54, 7.47) * mm, "end": v(56.47, 2.54) * mm});
            skLineSegment(sketch, "E303.0.2.90", {"start": v(0.9, 21.59) * mm, "end": v(10.75, 21.59) * mm});
            skLineSegment(sketch, "E303.0.2.91", {"start": v(127.74, 7.47) * mm, "end": v(132.67, 2.54) * mm});
            skLineSegment(sketch, "E303.0.2.92", {"start": v(61.85, 2.54) * mm, "end": v(66.78, 7.47) * mm});
            skLineSegment(sketch, "E303.0.2.93", {"start": v(89.64, 5.23) * mm, "end": v(94.57, 10.16) * mm});
            skLineSegment(sketch, "E303.0.2.94", {"start": v(142.98, 16.66) * mm, "end": v(147.9, 21.59) * mm});
            skLineSegment(sketch, "E303.0.2.95", {"start": v(16.13, 2.54) * mm, "end": v(21.06, 7.47) * mm});
            skLineSegment(sketch, "E303.0.2.96", {"start": v(-4.5, 21.59) * mm, "end": v(-9.42, 16.66) * mm});
            skLineSegment(sketch, "E303.0.2.97", {"start": v(31.37, 21.59) * mm, "end": v(41.23, 21.59) * mm});
            skLineSegment(sketch, "E303.0.2.98", {"start": v(23.75, 10.16) * mm, "end": v(33.6, 10.16) * mm});
            skLineSegment(sketch, "E303.0.2.99", {"start": v(112.5, 7.47) * mm, "end": v(117.43, 2.54) * mm});
            skLineSegment(sketch, "E303.0.2.100", {"start": v(13.44, 18.9) * mm, "end": v(8.51, 13.97) * mm});
            skLineSegment(sketch, "E303.0.2.101", {"start": v(8.51, 13.97) * mm, "end": v(18.37, 13.97) * mm});
            skLineSegment(sketch, "E303.0.2.103", {"start": v(74.4, 18.9) * mm, "end": v(79.33, 13.97) * mm});
            skLineSegment(sketch, "E303.0.2.104", {"start": v(59.16, 5.23) * mm, "end": v(64.09, 10.16) * mm});
            skLineSegment(sketch, "E303.0.2.105", {"start": v(59.16, 18.9) * mm, "end": v(54.23, 13.97) * mm});
            skLineSegment(sketch, "E303.0.2.106", {"start": v(5.82, 16.66) * mm, "end": v(10.75, 21.59) * mm});
            skLineSegment(sketch, "E303.0.2.107", {"start": v(92.33, 2.54) * mm, "end": v(97.26, 7.47) * mm});
            skLineSegment(sketch, "E303.0.2.108", {"start": v(66.78, 16.66) * mm, "end": v(71.7, 21.59) * mm});
            skLineSegment(sketch, "E303.0.2.109", {"start": v(28.68, 5.23) * mm, "end": v(23.75, 10.16) * mm});
            skLineSegment(sketch, "E303.0.2.110", {"start": v(122.81, 21.59) * mm, "end": v(132.67, 21.59) * mm});
            skLineSegment(sketch, "E303.0.2.111", {"start": v(138.05, 2.54) * mm, "end": v(142.98, 7.47) * mm});
            skLineSegment(sketch, "E303.0.2.112", {"start": v(135.36, 18.9) * mm, "end": v(140.29, 13.97) * mm});
            skLineSegment(sketch, "E303.0.2.113", {"start": v(8.51, 10.16) * mm, "end": v(18.37, 10.16) * mm});
            skLineSegment(sketch, "E303.0.2.114", {"start": v(21.06, 16.66) * mm, "end": v(25.99, 21.59) * mm});
            skLineSegment(sketch, "E303.0.2.115", {"start": v(82.02, 7.47) * mm, "end": v(86.95, 2.54) * mm});
            skLineSegment(sketch, "E303.0.2.116", {"start": v(74.4, 5.23) * mm, "end": v(69.47, 10.16) * mm});
            skLineSegment(sketch, "E303.0.2.117", {"start": v(54.23, 10.16) * mm, "end": v(64.09, 10.16) * mm});
            skLineSegment(sketch, "E303.0.2.118", {"start": v(89.64, 18.9) * mm, "end": v(94.57, 13.97) * mm});
            skLineSegment(sketch, "E303.0.2.119", {"start": v(112.5, 16.66) * mm, "end": v(117.43, 21.59) * mm});
            skLineSegment(sketch, "E303.0.2.120", {"start": v(13.44, 5.23) * mm, "end": v(8.51, 10.16) * mm});
            skLineSegment(sketch, "E303.0.2.121", {"start": v(13.44, 5.23) * mm, "end": v(18.37, 10.16) * mm});
            skLineSegment(sketch, "E303.0.2.122", {"start": v(39, 13.97) * mm, "end": v(48.85, 13.97) * mm});
            skLineSegment(sketch, "E303.0.2.123", {"start": v(84.71, 10.16) * mm, "end": v(94.57, 10.16) * mm});
            skLineSegment(sketch, "E303.0.2.124", {"start": v(-1.8, 18.9) * mm, "end": v(3.13, 13.97) * mm});
            skLineSegment(sketch, "E303.0.2.125", {"start": v(-1.8, 18.9) * mm, "end": v(-6.73, 13.97) * mm});
            skLineSegment(sketch, "E303.0.2.126", {"start": v(82.02, 16.66) * mm, "end": v(86.95, 21.59) * mm});
            skLineSegment(sketch, "E303.0.2.127", {"start": v(46.61, 21.59) * mm, "end": v(51.54, 16.66) * mm});
            skLineSegment(sketch, "E303.0.2.128", {"start": v(36.3, 16.66) * mm, "end": v(41.23, 21.59) * mm});
            skLineSegment(sketch, "E303.0.2.129", {"start": v(-9.42, 7.47) * mm, "end": v(-4.5, 2.54) * mm});
            skLineSegment(sketch, "E303.0.2.130", {"start": v(-4.5, 2.54) * mm, "end": v(-9.42, 2.54) * mm});
            skLineSegment(sketch, "E303.0.2.131", {"start": v(158.22, 16.66) * mm, "end": v(158.22, 21.59) * mm});
            skLineSegment(sketch, "E303.0.2.134", {"start": v(-9.42, 7.47) * mm, "end": v(-9.42, 2.54) * mm});
            skLineSegment(sketch, "E303.0.2.135", {"start": v(153.3, 21.59) * mm, "end": v(158.22, 21.59) * mm});
            skLineSegment(sketch, "E303.0.2.136", {"start": v(-9.42, 21.59) * mm, "end": v(-4.5, 21.59) * mm});
            skLineSegment(sketch, "E303.0.2.137", {"start": v(-9.42, 16.66) * mm, "end": v(-9.42, 21.59) * mm});
            skLineSegment(sketch, "E303.direction1", {"start": v(-9.42, 48.26) * mm, "end": v(15.98, 48.26) * mm, "construction": true});
            skLineSegment(sketch, "E303.direction2", {"start": v(-9.42, 48.26) * mm, "end": v(-9.42, 25.4) * mm, "construction": true});
            skLineSegment(sketch, "E304", {"start": v(-1.8, 5.23) * mm, "end": v(-1.8, 10.16) * mm});
            skLineSegment(sketch, "E305", {"start": v(5.82, 7.47) * mm, "end": v(5.82, 2.54) * mm});
            skLineSegment(sketch, "E306", {"start": v(150.6, 5.23) * mm, "end": v(150.6, 10.16) * mm});
            skSolve(sketch);
        }
        {
            var Q0;
            Q0 = qSketchRegion(id + "F32", true);
            extrude(context, id + "F33", {"entities" : qUnion([Q0]), "operationType" : NewBodyOperationType.REMOVE, "oppositeDirection" : true, "depth" : 2.54 * mm, "offsetDistance" : 25.4 * mm});
        }
        {
            var Q0;
            Q0=makeQuery(id+"F2.opExtrude","CAP_FACE",FACE,{"disambiguationData":[OSD([sQuery(id+"F1.wireOp",EDGE,"E8.0"),sQuery(id+"F1.wireOp",EDGE,"E8.1"),sQuery(id+"F1.wireOp",EDGE,"E8.2"),sQuery(id+"F1.wireOp",EDGE,"E8.3"),sQuery(id+"F1.wireOp",EDGE,"E9.0"),sQuery(id+"F1.wireOp",EDGE,"E9.1"),sQuery(id+"F1.wireOp",EDGE,"E9.2"),sQuery(id+"F1.wireOp",EDGE,"E9.3")])],"isStart":false});
            cPlane(context, id + "F34", {"entities" : qUnion([Q0]), "cplaneType" : CPlaneType.OFFSET, "offset" : 7 * mm, "oppositeDirection" : true, "width" : 152.4 * mm, "height" : 152.4 * mm});
        }
        {
            var Q0;
            Q0=qCreatedBy(id+"F34.planeOp",FACE);
            var sketch = newSketch(context, id + "F35", { "sketchPlane" : qUnion([Q0])});
            skLineSegment(sketch, "E307.bottom", {"start": v(-12.7, 16.51) * mm, "end": v(170, 16.51) * mm});
            skLineSegment(sketch, "E307.top", {"start": v(-12.7, -166.2) * mm, "end": v(170, -166.2) * mm});
            skLineSegment(sketch, "E307.left", {"start": v(-12.7, 16.51) * mm, "end": v(-12.7, -166.2) * mm});
            skLineSegment(sketch, "E307.right", {"start": v(170, 16.51) * mm, "end": v(170, -166.2) * mm});
            skSolve(sketch);
        }
        {
            var Q0;
            Q0 = qSketchRegion(id + "F35", true);
            extrude(context, id + "F36", {"entities" : qUnion([Q0]), "operationType" : NewBodyOperationType.ADD, "depth" : 3.8 * mm, "offsetDistance" : 25.4 * mm});
        }
        {
            var Q0;
            Q0 = qSketchRegion(id + "F35", true);
            extrude(context, id + "F37", {"entities" : qUnion([Q0]), "operationType" : NewBodyOperationType.REMOVE, "depth" : 25.4 * mm, "offsetDistance" : 25.4 * mm, "hasDraft" : true, "draftAngle" : 45 * degree, "draftPullDirection" : true});
        }
        {
            var Q0;
            Q0=makeQuery(id+"F6.boolean.opBoolean","MERGE",FACE,{"derivedFrom":[makeQuery(id+"F2.opExtrude","SWEPT_FACE",FACE,{"disambiguationData":[OSD([sQuery(id+"F1.wireOp",EDGE,"E9.0")])]}),makeQuery(id+"F6.opExtrude","SWEPT_FACE",FACE,{"disambiguationData":[OSD([sQuery(id+"F5.wireOp",EDGE,"E60.bottom")])]})]});
            var sketch = newSketch(context, id + "F38", { "sketchPlane" : qUnion([Q0])});
            skPoint(sketch, "E308.oppositeSnap0", {"position": v(-23.01, 23.16) * mm});
            skLineSegment(sketch, "E308.bottom", {"start": v(-171.9, 86.36) * mm, "end": v(14.6, 86.36) * mm});
            skLineSegment(sketch, "E308.top", {"start": v(-171.9, 23.16) * mm, "end": v(14.6, 23.16) * mm});
            skLineSegment(sketch, "E308.left", {"start": v(-171.9, 86.36) * mm, "end": v(-171.9, 23.16) * mm});
            skLineSegment(sketch, "E308.right", {"start": v(14.6, 86.36) * mm, "end": v(14.6, 23.16) * mm});
            skSolve(sketch);
        }
        {
            var Q0;
            Q0 = qSketchRegion(id + "F38", true);
            extrude(context, id + "F39", {"entities" : qUnion([Q0]), "operationType" : NewBodyOperationType.REMOVE, "oppositeDirection" : true, "depth" : 7.37 * mm, "offsetDistance" : 25.4 * mm});
        }
        {
            var Q0;
            {var subQ2=sQuery(id+"F1.wireOp",EDGE,"E8.3");var subQ4=sQuery(id+"F38.wireOp",EDGE,"E308.top");Q0=makeQuery(id+"F39.boolean.opBoolean","COPY",FACE,{"disambiguationData":[TD([makeQuery(id+"F2.opExtrude","SWEPT_FACE",FACE,{"disambiguationData":[OSD([subQ2])]})])],"derivedFrom":makeQuery(id+"F39.opExtrude","CAP_FACE",FACE,{"disambiguationData":[OSD([sQuery(id+"F38.wireOp",EDGE,"E308.bottom"),subQ4,sQuery(id+"F38.wireOp",EDGE,"E308.left"),sQuery(id+"F38.wireOp",EDGE,"E308.right")])],"isStart":false})});}
            var sketch = newSketch(context, id + "F40", { "sketchPlane" : qUnion([Q0])});
            skLineSegment(sketch, "E309.0.0", {"start": v(-170, 83.18) * mm, "end": v(-170, 86.36) * mm});
            skLineSegment(sketch, "E309.0.1", {"start": v(-170, 86.36) * mm, "end": v(-171.9, 86.36) * mm});
            skLineSegment(sketch, "E309.0.2", {"start": v(-171.9, 86.36) * mm, "end": v(-171.9, 23.16) * mm});
            skLineSegment(sketch, "E309.0.3", {"start": v(-171.9, 23.16) * mm, "end": v(-170, 23.16) * mm});
            skLineSegment(sketch, "E309.0.4", {"start": v(-170, 23.16) * mm, "end": v(-170, 79.38) * mm});
            skLineSegment(sketch, "E309.0.5", {"start": v(-170, 79.38) * mm, "end": v(-166.2, 83.18) * mm});
            skLineSegment(sketch, "E309.0.6", {"start": v(-166.2, 83.18) * mm, "end": v(-170, 83.18) * mm});
            skLineSegment(sketch, "E310.0.0", {"start": v(12.7, 83.18) * mm, "end": v(8.9, 83.18) * mm});
            skLineSegment(sketch, "E310.0.1", {"start": v(12.7, 79.38) * mm, "end": v(8.9, 83.18) * mm});
            skLineSegment(sketch, "E310.0.2", {"start": v(12.7, 79.38) * mm, "end": v(12.7, 23.16) * mm});
            skLineSegment(sketch, "E310.0.3", {"start": v(12.7, 23.16) * mm, "end": v(14.6, 23.16) * mm});
            skLineSegment(sketch, "E310.0.4", {"start": v(14.6, 23.16) * mm, "end": v(14.6, 86.36) * mm});
            skLineSegment(sketch, "E310.0.5", {"start": v(14.6, 86.36) * mm, "end": v(12.7, 86.36) * mm});
            skLineSegment(sketch, "E310.0.6", {"start": v(12.7, 86.36) * mm, "end": v(12.7, 83.18) * mm});
            skSolve(sketch);
        }
        {
            var Q0;
            Q0 = qSketchRegion(id + "F40", true);
            extrude(context, id + "F41", {"entities" : qUnion([Q0]), "operationType" : NewBodyOperationType.REMOVE, "endBound" : BoundingType.THROUGH_ALL, "oppositeDirection" : true, "depth" : 25.4 * mm, "offsetDistance" : 25.4 * mm});
        }
        {
            var Q0;
            Q0=makeQuery(id+"F41.boolean.opBoolean","COPY",FACE,{"derivedFrom":makeQuery(id+"F41.opExtrude","SWEPT_FACE",FACE,{"disambiguationData":[OSD([sQuery(id+"F40.wireOp",EDGE,"E310.0.2")])]})});
            var sketch = newSketch(context, id + "F42", { "sketchPlane" : qUnion([Q0])});
            skLineSegment(sketch, "E311.bottom", {"start": v(168.1, 23.16) * mm, "end": v(162.38, 23.16) * mm});
            skLineSegment(sketch, "E311.top", {"start": v(168.1, 86.36) * mm, "end": v(162.38, 86.36) * mm});
            skLineSegment(sketch, "E311.left", {"start": v(168.1, 23.16) * mm, "end": v(168.1, 86.36) * mm});
            skLineSegment(sketch, "E311.right", {"start": v(162.38, 23.16) * mm, "end": v(162.38, 86.36) * mm});
            skSolve(sketch);
        }
        {
            var Q0;
            Q0 = qSketchRegion(id + "F42", true);
            extrude(context, id + "F43", {"entities" : qUnion([Q0]), "operationType" : NewBodyOperationType.REMOVE, "endBound" : BoundingType.THROUGH_ALL, "oppositeDirection" : true, "depth" : 25.4 * mm, "offsetDistance" : 25.4 * mm});
        }
        {
            var Q0;
            Q0=qCreatedBy(makeId("Top.planeOp"),FACE);
            var sketch = newSketch(context, id + "F44", { "sketchPlane" : qUnion([Q0])});
            skLineSegment(sketch, "E312", {"start": v(67.13, 18.42) * mm, "end": v(67.13, -168.1) * mm});
            skLineSegment(sketch, "E313", {"start": v(67.13, -168.1) * mm, "end": v(67.51, -168.1) * mm});
            skLineSegment(sketch, "E314", {"start": v(67.51, -168.1) * mm, "end": v(67.51, 18.42) * mm});
            skLineSegment(sketch, "E315", {"start": v(67.51, 18.42) * mm, "end": v(67.13, 18.42) * mm});
            skSolve(sketch);
        }
        {
            var Q0;
            Q0 = qSketchRegion(id + "F44", true);
            extrude(context, id + "F45", {"entities" : qUnion([Q0]), "operationType" : NewBodyOperationType.REMOVE, "endBound" : BoundingType.THROUGH_ALL, "oppositeDirection" : true, "depth" : 25.4 * mm, "offsetDistance" : 25.4 * mm, "hasSecondDirection" : true, "secondDirectionBound" : SecondDirectionBoundingType.THROUGH_ALL, "secondDirectionOppositeDirection" : false, "secondDirectionDepth" : 25.4 * mm});
        }
        {
            var Q0;
            {var subQ0=sQuery(id+"F24.wireOp",EDGE,"E155.top");Q0=makeQuery(id+"F45.boolean.opBoolean","SPLIT",FACE,{"disambiguationData":[TD([makeQuery(id+"F2.opExtrude","SWEPT_FACE",FACE,{"disambiguationData":[OSD([sQuery(id+"F1.wireOp",EDGE,"E8.1")])]})])],"derivedFrom":makeQuery(id+"F43.boolean.opBoolean","MERGE",FACE,{"derivedFrom":[makeQuery(id+"F41.boolean.opBoolean","MERGE",FACE,{"derivedFrom":[makeQuery(id+"F39.boolean.opBoolean","MERGE",FACE,{"derivedFrom":[makeQuery(id+"F25.boolean.opBoolean","COPY",FACE,{"derivedFrom":makeQuery(id+"F25.opExtrude","SWEPT_FACE",FACE,{"disambiguationData":[OSD([subQ0]),TDD([makeQuery(id+"F24.imprint","IMPRINT",EDGE,{"disambiguationData":[TD([[makeQuery(id+"F24.imprint","INTERSECT",VERTEX,{"derivedFrom":[subQ0,sQuery(id+"F24.wireOp",EDGE,"E155.left")]}),-1.0]])],"derivedFrom":subQ0})])]})}),makeQuery(id+"F25.boolean.opBoolean","COPY",FACE,{"derivedFrom":makeQuery(id+"F25.opExtrude","SWEPT_FACE",FACE,{"disambiguationData":[OSD([subQ0]),TDD([makeQuery(id+"F24.imprint","IMPRINT",EDGE,{"disambiguationData":[TD([[makeQuery(id+"F24.imprint","INTERSECT",VERTEX,{"derivedFrom":[subQ0,sQuery(id+"F24.wireOp",EDGE,"E157")]}),-1.0]])],"derivedFrom":subQ0})])]})}),makeQuery(id+"F25.boolean.opBoolean","COPY",FACE,{"derivedFrom":makeQuery(id+"F25.opExtrude","SWEPT_FACE",FACE,{"disambiguationData":[OSD([subQ0]),TDD([makeQuery(id+"F24.imprint","IMPRINT",EDGE,{"disambiguationData":[TD([[makeQuery(id+"F24.imprint","INTERSECT",VERTEX,{"derivedFrom":[subQ0,sQuery(id+"F24.wireOp",EDGE,"E158.1.0.1")]}),-1.0]])],"derivedFrom":subQ0})])]})}),makeQuery(id+"F25.boolean.opBoolean","COPY",FACE,{"derivedFrom":makeQuery(id+"F25.opExtrude","SWEPT_FACE",FACE,{"disambiguationData":[OSD([subQ0]),TDD([makeQuery(id+"F24.imprint","IMPRINT",EDGE,{"disambiguationData":[TD([[makeQuery(id+"F24.imprint","INTERSECT",VERTEX,{"derivedFrom":[subQ0,sQuery(id+"F24.wireOp",EDGE,"E158.2.0.1")]}),-1.0]])],"derivedFrom":subQ0})])]})}),makeQuery(id+"F25.boolean.opBoolean","COPY",FACE,{"derivedFrom":makeQuery(id+"F25.opExtrude","SWEPT_FACE",FACE,{"disambiguationData":[OSD([subQ0]),TDD([makeQuery(id+"F24.imprint","IMPRINT",EDGE,{"disambiguationData":[TD([[makeQuery(id+"F24.imprint","INTERSECT",VERTEX,{"derivedFrom":[subQ0,sQuery(id+"F24.wireOp",EDGE,"E158.3.0.1")]}),-1.0]])],"derivedFrom":subQ0})])]})}),makeQuery(id+"F25.boolean.opBoolean","COPY",FACE,{"derivedFrom":makeQuery(id+"F25.opExtrude","SWEPT_FACE",FACE,{"disambiguationData":[OSD([subQ0]),TDD([makeQuery(id+"F24.imprint","IMPRINT",EDGE,{"disambiguationData":[TD([[makeQuery(id+"F24.imprint","INTERSECT",VERTEX,{"derivedFrom":[subQ0,sQuery(id+"F24.wireOp",EDGE,"E158.4.0.1")]}),-1.0]])],"derivedFrom":subQ0})])]})}),makeQuery(id+"F25.boolean.opBoolean","COPY",FACE,{"derivedFrom":makeQuery(id+"F25.opExtrude","SWEPT_FACE",FACE,{"disambiguationData":[OSD([subQ0]),TDD([makeQuery(id+"F24.imprint","IMPRINT",EDGE,{"disambiguationData":[TD([[makeQuery(id+"F24.imprint","INTERSECT",VERTEX,{"derivedFrom":[subQ0,sQuery(id+"F24.wireOp",EDGE,"E158.5.0.1")]}),-1.0]])],"derivedFrom":subQ0})])]})}),makeQuery(id+"F25.boolean.opBoolean","COPY",FACE,{"derivedFrom":makeQuery(id+"F25.opExtrude","SWEPT_FACE",FACE,{"disambiguationData":[OSD([subQ0]),TDD([makeQuery(id+"F24.imprint","IMPRINT",EDGE,{"disambiguationData":[TD([[makeQuery(id+"F24.imprint","INTERSECT",VERTEX,{"derivedFrom":[subQ0,sQuery(id+"F24.wireOp",EDGE,"E158.6.0.1")]}),-1.0]])],"derivedFrom":subQ0})])]})}),makeQuery(id+"F25.boolean.opBoolean","COPY",FACE,{"derivedFrom":makeQuery(id+"F25.opExtrude","SWEPT_FACE",FACE,{"disambiguationData":[OSD([subQ0]),TDD([makeQuery(id+"F24.imprint","IMPRINT",EDGE,{"disambiguationData":[TD([[makeQuery(id+"F24.imprint","INTERSECT",VERTEX,{"derivedFrom":[subQ0,sQuery(id+"F24.wireOp",EDGE,"E158.7.0.1")]}),-1.0]])],"derivedFrom":subQ0})])]})}),makeQuery(id+"F25.boolean.opBoolean","COPY",FACE,{"derivedFrom":makeQuery(id+"F25.opExtrude","SWEPT_FACE",FACE,{"disambiguationData":[OSD([subQ0]),TDD([makeQuery(id+"F24.imprint","IMPRINT",EDGE,{"disambiguationData":[TD([[makeQuery(id+"F24.imprint","INTERSECT",VERTEX,{"derivedFrom":[subQ0,sQuery(id+"F24.wireOp",EDGE,"E158.8.0.1")]}),-1.0]])],"derivedFrom":subQ0})])]})}),makeQuery(id+"F25.boolean.opBoolean","COPY",FACE,{"derivedFrom":makeQuery(id+"F25.opExtrude","SWEPT_FACE",FACE,{"disambiguationData":[OSD([subQ0]),TDD([makeQuery(id+"F24.imprint","IMPRINT",EDGE,{"disambiguationData":[TD([[makeQuery(id+"F24.imprint","INTERSECT",VERTEX,{"derivedFrom":[subQ0,sQuery(id+"F24.wireOp",EDGE,"E158.9.0.1")]}),-1.0]])],"derivedFrom":subQ0})])]})}),makeQuery(id+"F25.boolean.opBoolean","COPY",FACE,{"derivedFrom":makeQuery(id+"F25.opExtrude","SWEPT_FACE",FACE,{"disambiguationData":[OSD([subQ0]),TDD([makeQuery(id+"F24.imprint","IMPRINT",EDGE,{"disambiguationData":[TD([[makeQuery(id+"F24.imprint","INTERSECT",VERTEX,{"derivedFrom":[subQ0,sQuery(id+"F24.wireOp",EDGE,"E158.10.0.1")]}),-1.0]])],"derivedFrom":subQ0})])]})}),makeQuery(id+"F25.boolean.opBoolean","COPY",FACE,{"derivedFrom":makeQuery(id+"F25.opExtrude","SWEPT_FACE",FACE,{"disambiguationData":[OSD([subQ0]),TDD([makeQuery(id+"F24.imprint","IMPRINT",EDGE,{"disambiguationData":[TD([[makeQuery(id+"F24.imprint","INTERSECT",VERTEX,{"derivedFrom":[subQ0,sQuery(id+"F24.wireOp",EDGE,"E155.right")]}),1.0]])],"derivedFrom":subQ0})])]})})],"fromTools":[makeQuery(id+"F39.opExtrude","SWEPT_FACE",FACE,{"disambiguationData":[OSD([sQuery(id+"F38.wireOp",EDGE,"E308.top")])]})]})],"fromTools":[makeQuery(id+"F41.opExtrude","SWEPT_FACE",FACE,{"disambiguationData":[OSD([sQuery(id+"F40.wireOp",EDGE,"E309.0.3")])]}),makeQuery(id+"F41.opExtrude","SWEPT_FACE",FACE,{"disambiguationData":[OSD([sQuery(id+"F40.wireOp",EDGE,"E310.0.3")])]})]})],"fromTools":[makeQuery(id+"F43.opExtrude","SWEPT_FACE",FACE,{"disambiguationData":[OSD([sQuery(id+"F42.wireOp",EDGE,"E311.bottom")])]})]})});}
            var sketch = newSketch(context, id + "F46", { "sketchPlane" : qUnion([Q0])});
            skLineSegment(sketch, "E316.bottom", {"start": v(67.13, -168.1) * mm, "end": v(66.37, -168.1) * mm});
            skLineSegment(sketch, "E316.top", {"start": v(67.13, -166.2) * mm, "end": v(66.37, -166.2) * mm});
            skLineSegment(sketch, "E316.left", {"start": v(67.13, -168.1) * mm, "end": v(67.13, -166.2) * mm});
            skLineSegment(sketch, "E316.right", {"start": v(66.37, -168.1) * mm, "end": v(66.37, -166.2) * mm});
            skLineSegment(sketch, "E317.0", {"start": v(67.51, -168.1) * mm, "end": v(67.51, -166.2) * mm});
            skLineSegment(sketch, "E318", {"start": v(67.51, -166.2) * mm, "end": v(68.27, -166.2) * mm});
            skLineSegment(sketch, "E319", {"start": v(68.27, -166.2) * mm, "end": v(68.27, -168.1) * mm});
            skLineSegment(sketch, "E320", {"start": v(68.27, -168.1) * mm, "end": v(67.51, -168.1) * mm});
            skSolve(sketch);
        }
        {
            var Q0;
            Q0 = qSketchRegion(id + "F46", true);
            var Q1;
            Q1=qCreatedBy(makeId("Top.planeOp"),FACE);
            extrude(context, id + "F47", {"entities" : qUnion([Q0]), "operationType" : NewBodyOperationType.ADD, "endBound" : BoundingType.UP_TO_SURFACE, "oppositeDirection" : true, "depth" : 25.4 * mm, "endBoundEntityFace" : qUnion([Q1]), "offsetDistance" : 25.4 * mm});
        }
    });
